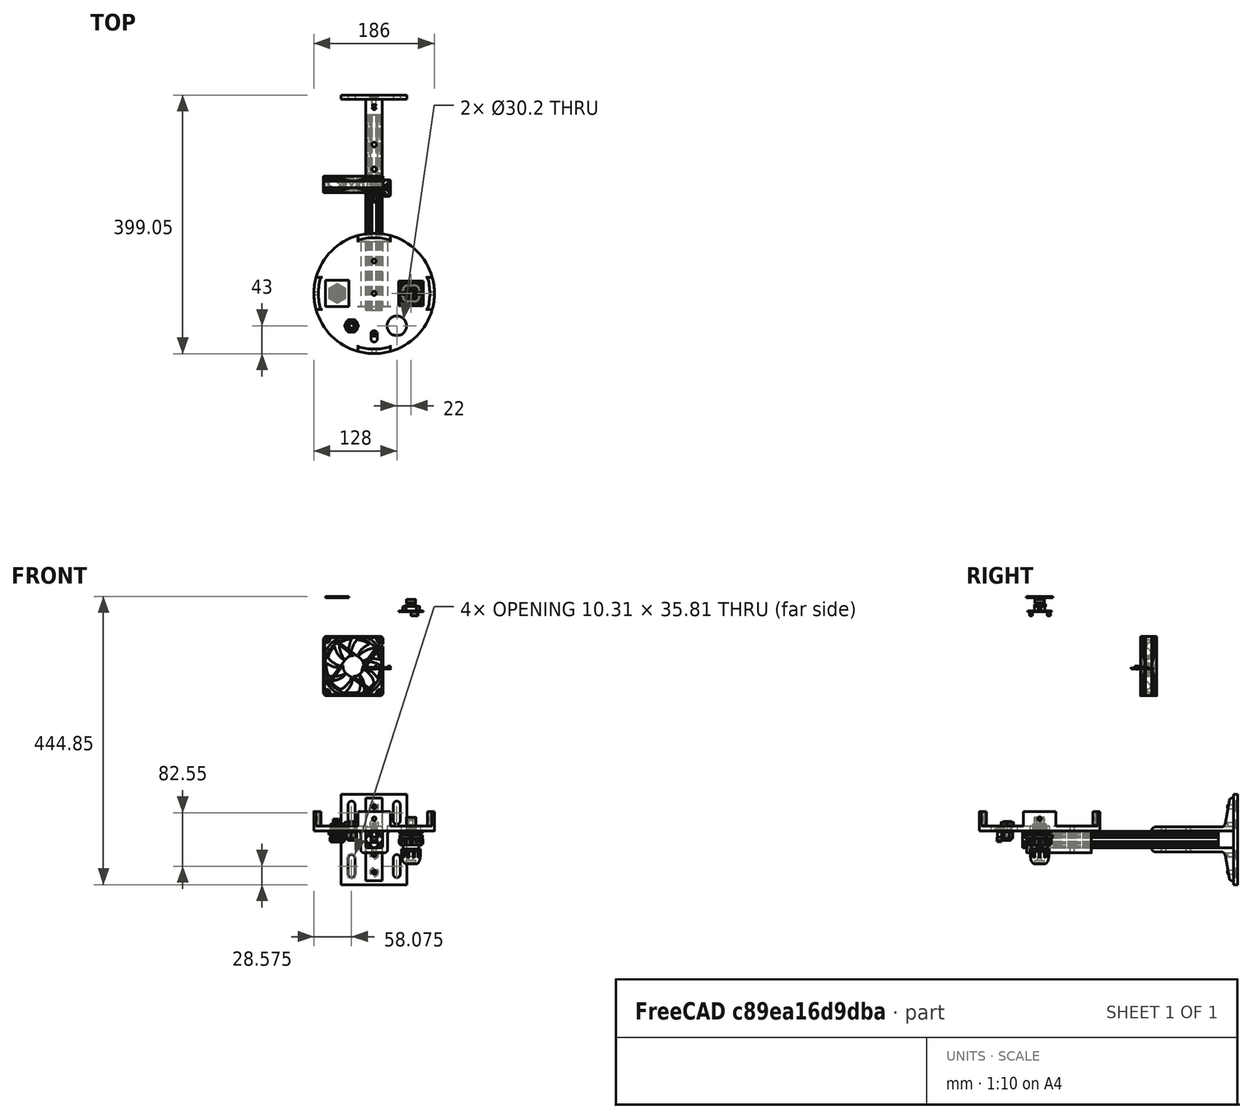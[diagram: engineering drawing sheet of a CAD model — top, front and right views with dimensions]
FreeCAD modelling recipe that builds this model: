
FCSTD DOCUMENT  (FreeCAD 0.20R29410 (Git))
Label: lightModuleV2_2023_08_31
License: All rights reserved
LicenseURL: http://en.wikipedia.org/wiki/All_rights_reserved
objects: Part::Cylinder×123, Part::Feature×114, Sketcher::SketchObject×101, Part::MultiFuse×93, Part::Cut×67, Part::Extrusion×37, Part::Loft×32, Part::Fillet×18, Part::Box×15, App::Part×14, Part::FeaturePython×10, Part::Sphere×4, Mesh::Feature×3, Part::Compound×1, Part::Cone×1, Part::Compound2×1, Part::MultiCommon×1
note: 617 computed .brp shape members not serialized (recipe doc carries the construction recipe); baked Part::Feature solids carry a one-line shape summary decoded from their .brp

FEATURE [Mesh::Feature] Odroid_H004  label="Odroid-H004"
  Placement = pos=(15,-110,-70) rot=(0.57735,-0.57735,0.57735;4.18879rad)
FEATURE [Sketcher::SketchObject] Sketch  label="top"
  FullyConstrained = true
  sketch-geometry (24):
    g0: Circle CenterX=0 CenterY=-150 CenterZ=0 NormalX=0 NormalY=0 NormalZ=1 AngleXU=0 Radius=98
    g1: Circle CenterX=-92 CenterY=-150 CenterZ=0 NormalX=0 NormalY=0 NormalZ=1 AngleXU=0 Radius=2
    g2: Circle CenterX=-57 CenterY=-115 CenterZ=0 NormalX=0 NormalY=0 NormalZ=1 AngleXU=0 Radius=2
    g3: Circle CenterX=-22 CenterY=-150 CenterZ=0 NormalX=0 NormalY=0 NormalZ=1 AngleXU=0 Radius=2
    g4: Circle CenterX=-57 CenterY=-185 CenterZ=0 NormalX=0 NormalY=0 NormalZ=1 AngleXU=0 Radius=2
    g5: Circle CenterX=0 CenterY=-172 CenterZ=0 NormalX=0 NormalY=0 NormalZ=1 AngleXU=0 Radius=2
    g6: Circle CenterX=0 CenterY=-242 CenterZ=0 NormalX=0 NormalY=0 NormalZ=1 AngleXU=0 Radius=2
    g7: Circle CenterX=-35 CenterY=-207 CenterZ=0 NormalX=0 NormalY=0 NormalZ=1 AngleXU=0 Radius=2
    g8: Circle CenterX=35 CenterY=-207 CenterZ=0 NormalX=0 NormalY=0 NormalZ=1 AngleXU=0 Radius=2
    g9: Circle CenterX=57 CenterY=-185 CenterZ=0 NormalX=0 NormalY=0 NormalZ=1 AngleXU=0 Radius=2
    g10: Circle CenterX=22 CenterY=-150 CenterZ=0 NormalX=0 NormalY=0 NormalZ=1 AngleXU=0 Radius=2
    g11: Circle CenterX=57 CenterY=-115 CenterZ=0 NormalX=0 NormalY=0 NormalZ=1 AngleXU=0 Radius=2
    g12: Circle CenterX=92 CenterY=-150 CenterZ=0 NormalX=0 NormalY=0 NormalZ=1 AngleXU=0 Radius=2
    g13: Circle CenterX=0 CenterY=-58 CenterZ=0 NormalX=0 NormalY=0 NormalZ=1 AngleXU=0 Radius=2
    g14: Circle CenterX=0 CenterY=-207 CenterZ=0 NormalX=0 NormalY=0 NormalZ=1 AngleXU=0 Radius=25
    g15: Circle CenterX=57 CenterY=-150 CenterZ=0 NormalX=0 NormalY=0 NormalZ=1 AngleXU=0 Radius=25
    g16: Circle CenterX=0 CenterY=-93 CenterZ=0 NormalX=0 NormalY=0 NormalZ=1 AngleXU=0 Radius=25
    g17: Circle CenterX=-35 CenterY=-93 CenterZ=0 NormalX=0 NormalY=0 NormalZ=1 AngleXU=0 Radius=2
    g18: Circle CenterX=35 CenterY=-93 CenterZ=0 NormalX=0 NormalY=0 NormalZ=1 AngleXU=0 Radius=2
    g19: Circle CenterX=0 CenterY=-128 CenterZ=0 NormalX=0 NormalY=0 NormalZ=1 AngleXU=0 Radius=2
    g20: LineSegment StartX=-75.25 StartY=-129.25 StartZ=0 EndX=-38.75 EndY=-129.25 EndZ=0
    g21: LineSegment StartX=-38.75 StartY=-129.25 StartZ=0 EndX=-38.75 EndY=-170.75 EndZ=0
    g22: LineSegment StartX=-38.75 StartY=-170.75 StartZ=0 EndX=-75.25 EndY=-170.75 EndZ=0
    g23: LineSegment StartX=-75.25 StartY=-170.75 StartZ=0 EndX=-75.25 EndY=-129.25 EndZ=0
  constraints (72):
    c: PointOnObject(g0,g-2)
    c: Radius(g0) = 98
    c: DistanceY(g0) = -150
    c: PointOnObject(g5,g-2)
    c: PointOnObject(g6,g-2)
    c: PointOnObject(g13,g-2)
    c: PointOnObject(g19,g-2)
    c: Equal(g6,g7)
    c: Equal(g6,g4)
    c: Equal(g6,g1)
    c: Equal(g6,g2)
    c: Equal(g6,g3)
    c: Equal(g6,g19)
    c: Equal(g6,g5)
    c: Equal(g6,g8)
    c: Equal(g6,g9)
    c: Equal(g6,g10)
    c: Equal(g6,g12)
    c: Equal(g6,g11)
    c: Equal(g6,g17)
    c: Equal(g6,g18)
    c: Equal(g6,g13)
    c: Radius(g6) = 2
    c: DistanceY(g12,g0) = 0
    c: DistanceY(g10,g0) = 0
    c: DistanceY(g0,g3) = 0
    c: DistanceY(g1,g3) = 0
    c: Equal(g15,g14)
    c: Equal(g15,g16)
    c: Radius(g15) = 25
    c: Coincident(g20,g21)
    c: Coincident(g21,g22)
    c: Coincident(g22,g23)
    c: Coincident(g23,g20)
    c: Horizontal(g20)
    c: Horizontal(g22)
    c: Vertical(g21)
    c: Vertical(g23)
    c: DistanceX(g20) = -38.75
    c: DistanceY(g0,g20) = 20.75
    c: DistanceY(g21,g0) = 20.75
    c: DistanceX(g22,g0) = 75.25
    c: DistanceX(g14,g0) = 0
    c: DistanceX(g0,g15) = 57
    c: DistanceY(g15,g0) = 0
    c: DistanceY(g0,g16) = 57
    c: DistanceX(g16,g0) = 0
    c: DistanceX(g0,g10) = 22
    c: DistanceX(g3,g0) = 22
    c: DistanceX(g1,g0) = 92
    c: DistanceX(g15,g12) = 35
    c: DistanceX(g16,g18) = 35
    c: DistanceX(g17,g16) = 35
    c: DistanceX(g7,g14) = 35
    c: DistanceX(g14,g8) = 35
    c: DistanceX(g9,g15) = 0
    c: DistanceX(g15,g11) = 0
    c: DistanceX(g2,g0) = 57
    c: DistanceY(g18,g16) = 0
    c: DistanceY(g16,g17) = 0
    c: DistanceY(g19,g16) = 35
    c: DistanceY(g16,g13) = 35
    c: DistanceY(g4,g0) = 35
    c: DistanceY(g0,g2) = 35
    c: DistanceY(g14,g5) = 35
    c: DistanceY(g6,g14) = 35
    c: DistanceY(g8,g14) = 0
    c: DistanceY(g14,g7) = 0
    c: DistanceY(g9,g15) = 35
    c: DistanceY(g15,g11) = 35
    c: DistanceX(g4,g2) = 0
    c: DistanceY(g14,g0) = 57
FEATURE [Part::Cylinder] Cylinder036
  Angle = 360
  AttacherType = Attacher::AttachEngine3D
  FirstAngle = 0
  Height = 10
  Placement = pos=(0,-21,0) rot=(0,0,1;0rad)
  Radius = 2
  SecondAngle = 0
FEATURE [Part::Cylinder] Cylinder037
  Angle = 360
  AttacherType = Attacher::AttachEngine3D
  FirstAngle = 0
  Height = 10
  Placement = pos=(20,-21,0) rot=(0,0,1;0rad)
  Radius = 2
  SecondAngle = 0
FEATURE [Part::Cylinder] Cylinder038
  Angle = 360
  AttacherType = Attacher::AttachEngine3D
  FirstAngle = 0
  Height = 10
  Placement = pos=(0,-21,0) rot=(0,0,1;0rad)
  Radius = 2
  SecondAngle = 0
FEATURE [Part::Cylinder] Cylinder039
  Angle = 360
  AttacherType = Attacher::AttachEngine3D
  FirstAngle = 0
  Height = 10
  Placement = pos=(20,-21,0) rot=(0,0,1;0rad)
  Radius = 2
  SecondAngle = 0
FEATURE [Part::Cylinder] Cylinder040  label="base002"
  Angle = 360
  AttacherType = Attacher::AttachEngine3D
  FirstAngle = 0
  Height = 5
  Placement = pos=(5,0,70) rot=(0,0,1;0rad)
  Radius = 40
  SecondAngle = 0
FEATURE [Part::Cylinder] Cylinder041  label="baseCut001"
  Angle = 360
  AttacherType = Attacher::AttachEngine3D
  FirstAngle = 0
  Height = 7
  Placement = pos=(5,0,74) rot=(0,0,1;0rad)
  Radius = 24
  SecondAngle = 0
FEATURE [Part::Cylinder] Cylinder042  label="wireCUt002"
  Angle = 360
  AttacherType = Attacher::AttachEngine3D
  FirstAngle = 0
  Height = 10
  Placement = pos=(-5,0,70) rot=(0,0,1;0rad)
  Radius = 2
  SecondAngle = 0
FEATURE [Part::Cylinder] Cylinder043  label="wireCUt003"
  Angle = 360
  AttacherType = Attacher::AttachEngine3D
  FirstAngle = 0
  Height = 10
  Placement = pos=(15,0,70) rot=(0,0,1;0rad)
  Radius = 2
  SecondAngle = 0
FEATURE [Part::Cylinder] Cylinder044  label="m3Cuts002"
  Angle = 360
  AttacherType = Attacher::AttachEngine3D
  FirstAngle = 0
  Height = 10
  Placement = pos=(5,-9,70) rot=(0,0,1;0rad)
  Radius = 1.75
  SecondAngle = 0
FEATURE [Part::Cylinder] Cylinder045  label="m3Cuts003"
  Angle = 360
  AttacherType = Attacher::AttachEngine3D
  FirstAngle = 0
  Height = 10
  Placement = pos=(5,9,70) rot=(0,0,1;0rad)
  Radius = 1.75
  SecondAngle = 0
FEATURE [Part::Cylinder] Cylinder046  label="m2HeatSetInsets004"
  Angle = 360
  AttacherType = Attacher::AttachEngine3D
  FirstAngle = 0
  Height = 10
  Placement = pos=(-30,0,65) rot=(0,0,1;0rad)
  Radius = 1.6
  SecondAngle = 0
FEATURE [Part::Cylinder] Cylinder047  label="m2HeatSetInsets005"
  Angle = 360
  AttacherType = Attacher::AttachEngine3D
  FirstAngle = 0
  Height = 10
  Placement = pos=(40,0,65) rot=(0,0,1;0rad)
  Radius = 1.6
  SecondAngle = 0
FEATURE [Part::Cylinder] Cylinder048  label="m2HeatSetInsets006"
  Angle = 360
  AttacherType = Attacher::AttachEngine3D
  FirstAngle = 0
  Height = 10
  Placement = pos=(5,35,65) rot=(0,0,1;0rad)
  Radius = 1.6
  SecondAngle = 0
FEATURE [Part::Cylinder] Cylinder049  label="m2HeatSetInsets007"
  Angle = 360
  AttacherType = Attacher::AttachEngine3D
  FirstAngle = 0
  Height = 10
  Placement = pos=(5,-35,65) rot=(0,0,1;0rad)
  Radius = 1.6
  SecondAngle = 0
FEATURE [Part::MultiFuse] Fusion014  label="m3HeatSetCuts003"
  Placement = pos=(-5,38.5,70) rot=(0,0,1;0rad)
  Shapes = -> [Cylinder037,Cylinder036]
FEATURE [Part::MultiFuse] Fusion015  label="m3HeatSetCuts004"
  Placement = pos=(-5,3.5,70) rot=(0,0,1;0rad)
  Shapes = -> [Cylinder039,Cylinder038]
FEATURE [Part::MultiFuse] Fusion016  label="m3HeatSetCuts005"
  Shapes = -> [Fusion015,Fusion014]
FEATURE [Part::MultiFuse] Fusion017  label="wireCuts001"
  Shapes = -> [Cylinder042,Cylinder043]
FEATURE [Part::MultiFuse] Fusion018  label="m3Cute001"
  Shapes = -> [Cylinder044,Cylinder045]
FEATURE [Part::MultiFuse] Fusion019  label="baseCUts001"
  Shapes = -> [Fusion016,Fusion017,Fusion018]
FEATURE [Part::MultiFuse] Fusion021
  Shapes = -> [Cylinder046,Cylinder047,Cylinder048,Cylinder049]
FEATURE [Part::Sphere] Sphere002  label="SphereBase001"
  Angle1 = 0
  Angle2 = 12
  Angle3 = 360
  AttacherType = Attacher::AttachEngine3D
  Placement = pos=(5,0,74) rot=(0,0,1;0rad)
  Radius = 29
FEATURE [Part::Cut] Cut006
  Base = -> Sphere002
  Tool = -> Cylinder041
FEATURE [Part::MultiFuse] Fusion020  label="base003"
  Shapes = -> [Cylinder040,Cut006]
FEATURE [Part::Cut] Cut007
  Base = -> Fusion020
  Tool = -> Fusion019
FEATURE [Part::Cut] Cut008  label="lightModule001"
  Base = -> Cut007
  Placement = pos=(-5,-207,0) rot=(0,1,0;0rad)
  Tool = -> Fusion021
FEATURE [Part::Box] Box005  label="as7265x"
  AttacherType = Attacher::AttachEngine3D
  Height = 2
  Length = 36
  Placement = pos=(-75,-170.5,110) rot=(0,0,1;0rad)
  Width = 41
FEATURE [Part::Cylinder] Cylinder050
  Angle = 360
  AttacherType = Attacher::AttachEngine3D
  FirstAngle = 0
  Height = 10
  Placement = pos=(0,-21,0) rot=(0,0,1;0rad)
  Radius = 2
  SecondAngle = 0
FEATURE [Part::Cylinder] Cylinder051
  Angle = 360
  AttacherType = Attacher::AttachEngine3D
  FirstAngle = 0
  Height = 10
  Placement = pos=(20,-21,0) rot=(0,0,1;0rad)
  Radius = 2
  SecondAngle = 0
FEATURE [Part::Cylinder] Cylinder052
  Angle = 360
  AttacherType = Attacher::AttachEngine3D
  FirstAngle = 0
  Height = 10
  Placement = pos=(0,-21,0) rot=(0,0,1;0rad)
  Radius = 2
  SecondAngle = 0
FEATURE [Part::Cylinder] Cylinder053
  Angle = 360
  AttacherType = Attacher::AttachEngine3D
  FirstAngle = 0
  Height = 10
  Placement = pos=(20,-21,0) rot=(0,0,1;0rad)
  Radius = 2
  SecondAngle = 0
FEATURE [Part::Cylinder] Cylinder054  label="base004"
  Angle = 360
  AttacherType = Attacher::AttachEngine3D
  FirstAngle = 0
  Height = 5
  Placement = pos=(5,0,70) rot=(0,0,1;0rad)
  Radius = 40
  SecondAngle = 0
FEATURE [Part::Cylinder] Cylinder055  label="baseCut002"
  Angle = 360
  AttacherType = Attacher::AttachEngine3D
  FirstAngle = 0
  Height = 7
  Placement = pos=(5,0,74) rot=(0,0,1;0rad)
  Radius = 24
  SecondAngle = 0
FEATURE [Part::Cylinder] Cylinder056  label="wireCUt004"
  Angle = 360
  AttacherType = Attacher::AttachEngine3D
  FirstAngle = 0
  Height = 10
  Placement = pos=(-5,0,70) rot=(0,0,1;0rad)
  Radius = 2
  SecondAngle = 0
FEATURE [Part::Cylinder] Cylinder057  label="wireCUt005"
  Angle = 360
  AttacherType = Attacher::AttachEngine3D
  FirstAngle = 0
  Height = 10
  Placement = pos=(15,0,70) rot=(0,0,1;0rad)
  Radius = 2
  SecondAngle = 0
FEATURE [Part::Cylinder] Cylinder058  label="m3Cuts004"
  Angle = 360
  AttacherType = Attacher::AttachEngine3D
  FirstAngle = 0
  Height = 10
  Placement = pos=(5,-9,70) rot=(0,0,1;0rad)
  Radius = 1.75
  SecondAngle = 0
FEATURE [Part::Cylinder] Cylinder059  label="m3Cuts005"
  Angle = 360
  AttacherType = Attacher::AttachEngine3D
  FirstAngle = 0
  Height = 10
  Placement = pos=(5,9,70) rot=(0,0,1;0rad)
  Radius = 1.75
  SecondAngle = 0
FEATURE [Part::Cylinder] Cylinder060  label="m2HeatSetInsets008"
  Angle = 360
  AttacherType = Attacher::AttachEngine3D
  FirstAngle = 0
  Height = 10
  Placement = pos=(-30,0,65) rot=(0,0,1;0rad)
  Radius = 1.6
  SecondAngle = 0
FEATURE [Part::Cylinder] Cylinder061  label="m2HeatSetInsets009"
  Angle = 360
  AttacherType = Attacher::AttachEngine3D
  FirstAngle = 0
  Height = 10
  Placement = pos=(40,0,65) rot=(0,0,1;0rad)
  Radius = 1.6
  SecondAngle = 0
FEATURE [Part::Cylinder] Cylinder062  label="m2HeatSetInsets010"
  Angle = 360
  AttacherType = Attacher::AttachEngine3D
  FirstAngle = 0
  Height = 10
  Placement = pos=(5,35,65) rot=(0,0,1;0rad)
  Radius = 1.6
  SecondAngle = 0
FEATURE [Part::Cylinder] Cylinder063  label="m2HeatSetInsets011"
  Angle = 360
  AttacherType = Attacher::AttachEngine3D
  FirstAngle = 0
  Height = 10
  Placement = pos=(5,-35,65) rot=(0,0,1;0rad)
  Radius = 1.6
  SecondAngle = 0
FEATURE [Part::MultiFuse] Fusion022  label="m3HeatSetCuts006"
  Placement = pos=(-5,38.5,70) rot=(0,0,1;0rad)
  Shapes = -> [Cylinder051,Cylinder050]
FEATURE [Part::MultiFuse] Fusion023  label="m3HeatSetCuts007"
  Placement = pos=(-5,3.5,70) rot=(0,0,1;0rad)
  Shapes = -> [Cylinder053,Cylinder052]
FEATURE [Part::MultiFuse] Fusion024  label="m3HeatSetCuts008"
  Shapes = -> [Fusion023,Fusion022]
FEATURE [Part::MultiFuse] Fusion025  label="wireCuts002"
  Shapes = -> [Cylinder056,Cylinder057]
FEATURE [Part::MultiFuse] Fusion026  label="m3Cute002"
  Shapes = -> [Cylinder058,Cylinder059]
FEATURE [Part::MultiFuse] Fusion027  label="baseCUts002"
  Shapes = -> [Fusion024,Fusion025,Fusion026]
FEATURE [Part::MultiFuse] Fusion029
  Shapes = -> [Cylinder060,Cylinder061,Cylinder062,Cylinder063]
FEATURE [Part::Sphere] Sphere003  label="SphereBase002"
  Angle1 = 0
  Angle2 = 12
  Angle3 = 360
  AttacherType = Attacher::AttachEngine3D
  Placement = pos=(5,0,74) rot=(0,0,1;0rad)
  Radius = 29
FEATURE [Part::Cut] Cut009
  Base = -> Sphere003
  Tool = -> Cylinder055
FEATURE [Part::MultiFuse] Fusion028  label="base005"
  Shapes = -> [Cylinder054,Cut009]
FEATURE [Part::Cut] Cut010
  Base = -> Fusion028
  Tool = -> Fusion027
FEATURE [Part::Cut] Cut011  label="lightModule002"
  Base = -> Cut010
  Placement = pos=(-62,-150,0) rot=(0,1,0;0rad)
  Tool = -> Fusion029
FEATURE [Part::Cylinder] Cylinder064
  Angle = 360
  AttacherType = Attacher::AttachEngine3D
  FirstAngle = 0
  Height = 10
  Placement = pos=(0,-21,0) rot=(0,0,1;0rad)
  Radius = 2
  SecondAngle = 0
FEATURE [Part::Cylinder] Cylinder065
  Angle = 360
  AttacherType = Attacher::AttachEngine3D
  FirstAngle = 0
  Height = 10
  Placement = pos=(20,-21,0) rot=(0,0,1;0rad)
  Radius = 2
  SecondAngle = 0
FEATURE [Part::Cylinder] Cylinder066
  Angle = 360
  AttacherType = Attacher::AttachEngine3D
  FirstAngle = 0
  Height = 10
  Placement = pos=(0,-21,0) rot=(0,0,1;0rad)
  Radius = 2
  SecondAngle = 0
FEATURE [Part::Cylinder] Cylinder067
  Angle = 360
  AttacherType = Attacher::AttachEngine3D
  FirstAngle = 0
  Height = 10
  Placement = pos=(20,-21,0) rot=(0,0,1;0rad)
  Radius = 2
  SecondAngle = 0
FEATURE [Part::Cylinder] Cylinder068  label="base006"
  Angle = 360
  AttacherType = Attacher::AttachEngine3D
  FirstAngle = 0
  Height = 5
  Placement = pos=(5,0,70) rot=(0,0,1;0rad)
  Radius = 40
  SecondAngle = 0
FEATURE [Part::Cylinder] Cylinder069  label="baseCut003"
  Angle = 360
  AttacherType = Attacher::AttachEngine3D
  FirstAngle = 0
  Height = 7
  Placement = pos=(5,0,74) rot=(0,0,1;0rad)
  Radius = 24
  SecondAngle = 0
FEATURE [Part::Cylinder] Cylinder070  label="wireCUt006"
  Angle = 360
  AttacherType = Attacher::AttachEngine3D
  FirstAngle = 0
  Height = 10
  Placement = pos=(-5,0,70) rot=(0,0,1;0rad)
  Radius = 2
  SecondAngle = 0
FEATURE [Part::Cylinder] Cylinder071  label="wireCUt007"
  Angle = 360
  AttacherType = Attacher::AttachEngine3D
  FirstAngle = 0
  Height = 10
  Placement = pos=(15,0,70) rot=(0,0,1;0rad)
  Radius = 2
  SecondAngle = 0
FEATURE [Part::Cylinder] Cylinder072  label="m3Cuts006"
  Angle = 360
  AttacherType = Attacher::AttachEngine3D
  FirstAngle = 0
  Height = 10
  Placement = pos=(5,-9,70) rot=(0,0,1;0rad)
  Radius = 1.75
  SecondAngle = 0
FEATURE [Part::Cylinder] Cylinder073  label="m3Cuts007"
  Angle = 360
  AttacherType = Attacher::AttachEngine3D
  FirstAngle = 0
  Height = 10
  Placement = pos=(5,9,70) rot=(0,0,1;0rad)
  Radius = 1.75
  SecondAngle = 0
FEATURE [Part::Cylinder] Cylinder074  label="m2HeatSetInsets012"
  Angle = 360
  AttacherType = Attacher::AttachEngine3D
  FirstAngle = 0
  Height = 10
  Placement = pos=(-30,0,65) rot=(0,0,1;0rad)
  Radius = 1.6
  SecondAngle = 0
FEATURE [Part::Cylinder] Cylinder075  label="m2HeatSetInsets013"
  Angle = 360
  AttacherType = Attacher::AttachEngine3D
  FirstAngle = 0
  Height = 10
  Placement = pos=(40,0,65) rot=(0,0,1;0rad)
  Radius = 1.6
  SecondAngle = 0
FEATURE [Part::Cylinder] Cylinder076  label="m2HeatSetInsets014"
  Angle = 360
  AttacherType = Attacher::AttachEngine3D
  FirstAngle = 0
  Height = 10
  Placement = pos=(5,35,65) rot=(0,0,1;0rad)
  Radius = 1.6
  SecondAngle = 0
FEATURE [Part::Cylinder] Cylinder077  label="m2HeatSetInsets015"
  Angle = 360
  AttacherType = Attacher::AttachEngine3D
  FirstAngle = 0
  Height = 10
  Placement = pos=(5,-35,65) rot=(0,0,1;0rad)
  Radius = 1.6
  SecondAngle = 0
FEATURE [Part::MultiFuse] Fusion030  label="m3HeatSetCuts009"
  Placement = pos=(-5,38.5,70) rot=(0,0,1;0rad)
  Shapes = -> [Cylinder065,Cylinder064]
FEATURE [Part::MultiFuse] Fusion031  label="m3HeatSetCuts010"
  Placement = pos=(-5,3.5,70) rot=(0,0,1;0rad)
  Shapes = -> [Cylinder067,Cylinder066]
FEATURE [Part::MultiFuse] Fusion032  label="m3HeatSetCuts011"
  Shapes = -> [Fusion031,Fusion030]
FEATURE [Part::MultiFuse] Fusion033  label="wireCuts003"
  Shapes = -> [Cylinder070,Cylinder071]
FEATURE [Part::MultiFuse] Fusion034  label="m3Cute003"
  Shapes = -> [Cylinder072,Cylinder073]
FEATURE [Part::MultiFuse] Fusion035  label="baseCUts003"
  Shapes = -> [Fusion032,Fusion033,Fusion034]
FEATURE [Part::MultiFuse] Fusion037
  Shapes = -> [Cylinder074,Cylinder075,Cylinder076,Cylinder077]
FEATURE [Part::Sphere] Sphere004  label="SphereBase003"
  Angle1 = 0
  Angle2 = 12
  Angle3 = 360
  AttacherType = Attacher::AttachEngine3D
  Placement = pos=(5,0,74) rot=(0,0,1;0rad)
  Radius = 29
FEATURE [Part::Cut] Cut012
  Base = -> Sphere004
  Tool = -> Cylinder069
FEATURE [Part::MultiFuse] Fusion036  label="base007"
  Shapes = -> [Cylinder068,Cut012]
FEATURE [Part::Cut] Cut013
  Base = -> Fusion036
  Tool = -> Fusion035
FEATURE [Part::Cut] Cut014  label="lightModule003"
  Base = -> Cut013
  Placement = pos=(52,-150,0) rot=(0,1,0;0rad)
  Tool = -> Fusion037
FEATURE [Part::Cylinder] Cylinder078
  Angle = 360
  AttacherType = Attacher::AttachEngine3D
  FirstAngle = 0
  Height = 10
  Placement = pos=(0,-21,0) rot=(0,0,1;0rad)
  Radius = 2
  SecondAngle = 0
FEATURE [Part::Cylinder] Cylinder079
  Angle = 360
  AttacherType = Attacher::AttachEngine3D
  FirstAngle = 0
  Height = 10
  Placement = pos=(20,-21,0) rot=(0,0,1;0rad)
  Radius = 2
  SecondAngle = 0
FEATURE [Part::Cylinder] Cylinder080
  Angle = 360
  AttacherType = Attacher::AttachEngine3D
  FirstAngle = 0
  Height = 10
  Placement = pos=(0,-21,0) rot=(0,0,1;0rad)
  Radius = 2
  SecondAngle = 0
FEATURE [Part::Cylinder] Cylinder081
  Angle = 360
  AttacherType = Attacher::AttachEngine3D
  FirstAngle = 0
  Height = 10
  Placement = pos=(20,-21,0) rot=(0,0,1;0rad)
  Radius = 2
  SecondAngle = 0
FEATURE [Part::Cylinder] Cylinder082  label="base008"
  Angle = 360
  AttacherType = Attacher::AttachEngine3D
  FirstAngle = 0
  Height = 5
  Placement = pos=(5,0,70) rot=(0,0,1;0rad)
  Radius = 40
  SecondAngle = 0
FEATURE [Part::Cylinder] Cylinder083  label="baseCut004"
  Angle = 360
  AttacherType = Attacher::AttachEngine3D
  FirstAngle = 0
  Height = 7
  Placement = pos=(5,0,74) rot=(0,0,1;0rad)
  Radius = 24
  SecondAngle = 0
FEATURE [Part::Cylinder] Cylinder084  label="wireCUt008"
  Angle = 360
  AttacherType = Attacher::AttachEngine3D
  FirstAngle = 0
  Height = 10
  Placement = pos=(-5,0,70) rot=(0,0,1;0rad)
  Radius = 2
  SecondAngle = 0
FEATURE [Part::Cylinder] Cylinder085  label="wireCUt009"
  Angle = 360
  AttacherType = Attacher::AttachEngine3D
  FirstAngle = 0
  Height = 10
  Placement = pos=(15,0,70) rot=(0,0,1;0rad)
  Radius = 2
  SecondAngle = 0
FEATURE [Part::Cylinder] Cylinder086  label="m3Cuts008"
  Angle = 360
  AttacherType = Attacher::AttachEngine3D
  FirstAngle = 0
  Height = 10
  Placement = pos=(5,-9,70) rot=(0,0,1;0rad)
  Radius = 1.75
  SecondAngle = 0
FEATURE [Part::Cylinder] Cylinder087  label="m3Cuts009"
  Angle = 360
  AttacherType = Attacher::AttachEngine3D
  FirstAngle = 0
  Height = 10
  Placement = pos=(5,9,70) rot=(0,0,1;0rad)
  Radius = 1.75
  SecondAngle = 0
FEATURE [Part::Cylinder] Cylinder088  label="m2HeatSetInsets016"
  Angle = 360
  AttacherType = Attacher::AttachEngine3D
  FirstAngle = 0
  Height = 10
  Placement = pos=(-30,0,65) rot=(0,0,1;0rad)
  Radius = 1.6
  SecondAngle = 0
FEATURE [Part::Cylinder] Cylinder089  label="m2HeatSetInsets017"
  Angle = 360
  AttacherType = Attacher::AttachEngine3D
  FirstAngle = 0
  Height = 10
  Placement = pos=(40,0,65) rot=(0,0,1;0rad)
  Radius = 1.6
  SecondAngle = 0
FEATURE [Part::Cylinder] Cylinder090  label="m2HeatSetInsets018"
  Angle = 360
  AttacherType = Attacher::AttachEngine3D
  FirstAngle = 0
  Height = 10
  Placement = pos=(5,35,65) rot=(0,0,1;0rad)
  Radius = 1.6
  SecondAngle = 0
FEATURE [Part::Cylinder] Cylinder091  label="m2HeatSetInsets019"
  Angle = 360
  AttacherType = Attacher::AttachEngine3D
  FirstAngle = 0
  Height = 10
  Placement = pos=(5,-35,65) rot=(0,0,1;0rad)
  Radius = 1.6
  SecondAngle = 0
FEATURE [Part::MultiFuse] Fusion038  label="m3HeatSetCuts012"
  Placement = pos=(-5,38.5,70) rot=(0,0,1;0rad)
  Shapes = -> [Cylinder079,Cylinder078]
FEATURE [Part::MultiFuse] Fusion039  label="m3HeatSetCuts013"
  Placement = pos=(-5,3.5,70) rot=(0,0,1;0rad)
  Shapes = -> [Cylinder081,Cylinder080]
FEATURE [Part::MultiFuse] Fusion040  label="m3HeatSetCuts014"
  Shapes = -> [Fusion039,Fusion038]
FEATURE [Part::MultiFuse] Fusion041  label="wireCuts004"
  Shapes = -> [Cylinder084,Cylinder085]
FEATURE [Part::MultiFuse] Fusion042  label="m3Cute004"
  Shapes = -> [Cylinder086,Cylinder087]
FEATURE [Part::MultiFuse] Fusion043  label="baseCUts004"
  Shapes = -> [Fusion040,Fusion041,Fusion042]
FEATURE [Part::MultiFuse] Fusion045
  Shapes = -> [Cylinder088,Cylinder089,Cylinder090,Cylinder091]
FEATURE [Part::Sphere] Sphere005  label="SphereBase004"
  Angle1 = 0
  Angle2 = 12
  Angle3 = 360
  AttacherType = Attacher::AttachEngine3D
  Placement = pos=(5,0,74) rot=(0,0,1;0rad)
  Radius = 29
FEATURE [Part::Cut] Cut015
  Base = -> Sphere005
  Tool = -> Cylinder083
FEATURE [Part::MultiFuse] Fusion044  label="base009"
  Shapes = -> [Cylinder082,Cut015]
FEATURE [Part::Cut] Cut016
  Base = -> Fusion044
  Tool = -> Fusion043
FEATURE [Part::Cut] Cut017  label="lightModule004"
  Base = -> Cut016
  Placement = pos=(-5,-93,0) rot=(0,1,0;0rad)
  Tool = -> Fusion045
FEATURE [Part::MultiFuse] Fusion  label="lightModules"
  Placement = pos=(0,0,30) rot=(0,0,1;0rad)
  Shapes = -> [Cut008,Cut011,Cut014,Cut017]
FEATURE [Part::Extrusion] Extrude  label="top001"
  Base = -> Sketch
  Dir = (0,0,1)
  DirMode = 2
  FaceMakerClass = Part::FaceMakerBullseye
  LengthFwd = 5
  LengthRev = 0
  Placement = pos=(0,0,100) rot=(0,0,1;0rad)
  Solid = true
  Symmetric = false
FEATURE [Part::Feature] Part__Feature  label="elpCamera"
  Placement = pos=(57,-150,90) rot=(0,0,1;0rad)
  shape: bbox 38 x 38 x 25.12 mm, 164 faces (baked)
FEATURE [Part::FeaturePython] Tube  label="tube001"  # WARN: FeaturePython — macro-defined, semantics opaque (R4)
  AttacherType = Attacher::AttachEngine3D
  Height = 20
  InnerRadius = 94
  OuterRadius = 98
  Placement = pos=(0,-150,80) rot=(0,0,1;0rad)
FEATURE [Part::Feature] Part__Feature010  label="veml6075_sensor"
  Placement = pos=(0,-92,105) rot=(0,0,1;0rad)
  shape: bbox 15.31 x 17.01 x 46.02 mm, 450 faces (baked)
FEATURE [Sketcher::SketchObject] Sketch001
  FullyConstrained = true
  Placement = pos=(0,0,105) rot=(0,0,1;0rad)
  sketch-geometry (14):
    g0: Circle CenterX=0 CenterY=-93 CenterZ=0 NormalX=0 NormalY=0 NormalZ=1 AngleXU=0 Radius=25
    g1: Circle CenterX=0 CenterY=-93 CenterZ=0 NormalX=0 NormalY=0 NormalZ=1 AngleXU=0 Radius=26.5
    g2: Circle CenterX=57 CenterY=-150 CenterZ=0 NormalX=0 NormalY=0 NormalZ=1 AngleXU=0 Radius=25
    g3: Circle CenterX=57 CenterY=-150 CenterZ=0 NormalX=0 NormalY=0 NormalZ=1 AngleXU=0 Radius=26.5
    g4: Circle CenterX=0 CenterY=-207 CenterZ=0 NormalX=0 NormalY=0 NormalZ=1 AngleXU=0 Radius=25
    g5: Circle CenterX=0 CenterY=-207 CenterZ=0 NormalX=0 NormalY=0 NormalZ=1 AngleXU=0 Radius=26.5
    g6: LineSegment StartX=-75.25 StartY=-129.25 StartZ=0 EndX=-38.75 EndY=-129.25 EndZ=0
    g7: LineSegment StartX=-38.75 StartY=-129.25 StartZ=0 EndX=-38.75 EndY=-170.75 EndZ=0
    g8: LineSegment StartX=-38.75 StartY=-170.75 StartZ=0 EndX=-75.25 EndY=-170.75 EndZ=0
    g9: LineSegment StartX=-75.25 StartY=-170.75 StartZ=0 EndX=-75.25 EndY=-129.25 EndZ=0
    g10: LineSegment StartX=-75.7 StartY=-128.8 StartZ=0 EndX=-38.3 EndY=-128.8 EndZ=0
    g11: LineSegment StartX=-38.3 StartY=-128.8 StartZ=0 EndX=-38.3 EndY=-171.2 EndZ=0
    g12: LineSegment StartX=-38.3 StartY=-171.2 StartZ=0 EndX=-75.7 EndY=-171.2 EndZ=0
    g13: LineSegment StartX=-75.7 StartY=-171.2 StartZ=0 EndX=-75.7 EndY=-128.8 EndZ=0
  constraints (39):
    c: PointOnObject(g0,g-2)
    c: Coincident(g1,g0)
    c: Coincident(g3,g2)
    c: PointOnObject(g4,g-2)
    c: Coincident(g5,g4)
    c: Coincident(g6,g7)
    c: Coincident(g7,g8)
    c: Coincident(g8,g9)
    c: Coincident(g9,g6)
    c: Horizontal(g6)
    c: Horizontal(g8)
    c: Vertical(g7)
    c: Vertical(g9)
    c: DistanceY(g0) = -93
    c: DistanceY(g2) = -150
    c: DistanceX(g2) = 57
    c: Equal(g0,g2)
    c: Equal(g0,g4)
    c: Radius(g0) = 25
    c: Equal(g3,g1)
    c: Equal(g3,g5)
    c: Radius(g3) = 26.5
    c: DistanceY(g4) = -207
    c: DistanceY(g7) = -170.75
    c: DistanceX(g7) = -38.75
    c: DistanceX(g6) = -75.25
    c: DistanceY(g6) = -129.25
    c: Coincident(g10,g11)
    c: Coincident(g11,g12)
    c: Coincident(g12,g13)
    c: Coincident(g13,g10)
    c: Horizontal(g10)
    c: Horizontal(g12)
    c: Vertical(g11)
    c: Vertical(g13)
    c: DistanceY(g11,g7) = 0.45
    c: DistanceX(g7,g11) = 0.45
    c: DistanceX(g10,g6) = 0.45
    c: DistanceY(g6,g10) = 0.45
FEATURE [Part::Extrusion] Extrude001
  Base = -> Sketch001
  Dir = (0,0,1)
  DirMode = 2
  FaceMakerClass = Part::FaceMakerBullseye
  LengthFwd = 1
  LengthRev = 0
  Solid = true
  Symmetric = false
FEATURE [Part::MultiFuse] Fusion046  label="top002"
  Shapes = -> [Extrude001,Extrude]
FEATURE [Part::Cylinder] Cylinder
  Angle = 360
  AttacherType = Attacher::AttachEngine3D
  FirstAngle = 0
  Height = 300
  Placement = pos=(0,0,90) rot=(1,0,0;1.5708rad)
  Radius = 2.2
  SecondAngle = 0
FEATURE [Part::Cylinder] Cylinder092
  Angle = 360
  AttacherType = Attacher::AttachEngine3D
  FirstAngle = 0
  Height = 300
  Placement = pos=(-150,-150,90) rot=(0.57735,0.57735,0.57735;2.0944rad)
  Radius = 2.2
  SecondAngle = 0
FEATURE [Part::MultiFuse] Fusion047  label="m4Cuts"
  Shapes = -> [Cylinder092,Cylinder]
FEATURE [Part::Fillet] Fillet  label="top003"
  Base = -> Fusion046
  Edges = 1 edges r=2: [Edge3]
FEATURE [Part::Fillet] Fillet001  label="tube"
  Base = -> Tube
  Edges = 1 edges r=2: [Edge5]
FEATURE [Part::MultiFuse] Fusion048  label="top004"
  Shapes = -> [Fillet,Fillet001]
FEATURE [Part::Cut] Cut  label="top005"
  Base = -> Fusion048
  Tool = -> Fusion047
FEATURE [Part::Cylinder] Cylinder094  label="refModules"
  Angle = 360
  AttacherType = Attacher::AttachEngine3D
  FirstAngle = 0
  Height = 75
  Placement = pos=(0,-207,37) rot=(0,0,1;0rad)
  Radius = 3.75
  SecondAngle = 0
FEATURE [Part::Cylinder] Cylinder095  label="refModulesCoverCut"
  Angle = 360
  AttacherType = Attacher::AttachEngine3D
  FirstAngle = 0
  Height = 60
  Placement = pos=(0,-207,37) rot=(0,0,1;0rad)
  Radius = 4.5
  SecondAngle = 0
FEATURE [Sketcher::SketchObject] Sketch002
  FullyConstrained = true
  sketch-geometry (16):
    g0: Circle CenterX=-67 CenterY=-167.5 CenterZ=0 NormalX=0 NormalY=0 NormalZ=1 AngleXU=0 Radius=1.625
    g1: Circle CenterX=-47 CenterY=-167.5 CenterZ=0 NormalX=0 NormalY=0 NormalZ=1 AngleXU=0 Radius=1.625
    g2: Circle CenterX=-67 CenterY=-132.5 CenterZ=0 NormalX=0 NormalY=0 NormalZ=1 AngleXU=0 Radius=1.625
    g3: Circle CenterX=-47 CenterY=-132.5 CenterZ=0 NormalX=0 NormalY=0 NormalZ=1 AngleXU=0 Radius=1.625
    g4: LineSegment StartX=-62 StartY=-129.75 StartZ=0 EndX=-72 EndY=-129.75 EndZ=0
    g5: LineSegment StartX=-52 StartY=-129.75 StartZ=0 EndX=-42 EndY=-129.75 EndZ=0
    g6: LineSegment StartX=-72 StartY=-129.75 StartZ=0 EndX=-72 EndY=-170.25 EndZ=0
    g7: LineSegment StartX=-72 StartY=-170.25 StartZ=0 EndX=-62 EndY=-170.25 EndZ=0
    g8: LineSegment StartX=-62 StartY=-170.25 StartZ=0 EndX=-62 EndY=-155 EndZ=0
    g9: LineSegment StartX=-52 StartY=-155 StartZ=0 EndX=-52 EndY=-170.25 EndZ=0
    g10: LineSegment StartX=-52 StartY=-170.25 StartZ=0 EndX=-42 EndY=-170.25 EndZ=0
    g11: LineSegment StartX=-42 StartY=-170.25 StartZ=0 EndX=-42 EndY=-129.75 EndZ=0
    g12: LineSegment StartX=-62 StartY=-155 StartZ=0 EndX=-52 EndY=-155 EndZ=0
    g13: LineSegment StartX=-62 StartY=-129.75 StartZ=0 EndX=-62 EndY=-145 EndZ=0
    g14: LineSegment StartX=-62 StartY=-145 StartZ=0 EndX=-52 EndY=-145 EndZ=0
    g15: LineSegment StartX=-52 StartY=-145 StartZ=0 EndX=-52 EndY=-129.75 EndZ=0
  constraints (48):
    c: DistanceY(g2,g3) = 0
    c: DistanceX(g0,g2) = 0
    c: DistanceX(g1,g3) = 0
    c: DistanceX(g1) = -47
    c: DistanceY(g1) = -167.5
    c: DistanceX(g0,g1) = 20
    c: Horizontal(g4)
    c: Horizontal(g5)
    c: Vertical(g6)
    c: Coincident(g7,g6)
    c: Horizontal(g7)
    c: Coincident(g8,g7)
    c: Vertical(g9)
    c: Coincident(g10,g9)
    c: Horizontal(g10)
    c: Coincident(g11,g10)
    c: Vertical(g8)
    c: DistanceX(g4,g4) = 10
    c: DistanceX(g5,g5) = 10
    c: DistanceX(g6,g7) = 10
    c: DistanceX(g9,g10) = 10
    c: Vertical(g11)
    c: DistanceY(g7,g9) = 0
    c: DistanceY(g4,g5) = 0
    c: DistanceX(g6,g0) = 5
    c: DistanceX(g9,g1) = 5
    c: DistanceY(g2,g4) = 2.75
    c: Coincident(g4,g6)
    c: Coincident(g12,g8)
    c: Horizontal(g12)
    c: Coincident(g9,g12)
    c: Coincident(g13,g4)
    c: Vertical(g13)
    c: Coincident(g14,g13)
    c: Horizontal(g14)
    c: Coincident(g15,g14)
    c: Coincident(g15,g5)
    c: Vertical(g15)
    c: Coincident(g5,g11)
    c: DistanceY(g8,g13) = 10
    c: DistanceY(g13) = -145
    c: DistanceY(g7,g0) = 2.75
    c: Equal(g1,g0)
    c: Equal(g1,g2)
    c: Equal(g1,g3)
    c: Diameter(g1) = 3.25
    c: DistanceY(g1,g0) = 0
    c: DistanceY(g2) = -132.5
FEATURE [Sketcher::SketchObject] Sketch003
  FullyConstrained = true
  sketch-geometry (6):
    g0: Circle CenterX=74 CenterY=-167 CenterZ=0 NormalX=0 NormalY=0 NormalZ=1 AngleXU=0 Radius=1.65
    g1: Circle CenterX=40 CenterY=-167 CenterZ=0 NormalX=0 NormalY=0 NormalZ=1 AngleXU=0 Radius=1.65
    g2: Circle CenterX=40 CenterY=-133 CenterZ=0 NormalX=0 NormalY=0 NormalZ=1 AngleXU=0 Radius=1.65
    g3: Circle CenterX=74 CenterY=-133 CenterZ=0 NormalX=0 NormalY=0 NormalZ=1 AngleXU=0 Radius=1.65
    g4: Circle CenterX=57 CenterY=-150 CenterZ=0 NormalX=0 NormalY=0 NormalZ=1 AngleXU=0 Radius=27.5
    g5: Circle CenterX=57 CenterY=-150 CenterZ=0 NormalX=0 NormalY=0 NormalZ=1 AngleXU=0 Radius=21
  constraints (17):
    c: Equal(g3,g0)
    c: Equal(g3,g1)
    c: Equal(g3,g2)
    c: Diameter(g3) = 3.3
    c: DistanceX(g1) = 40
    c: DistanceY(g1) = -167
    c: DistanceY(g1,g0) = 0
    c: DistanceX(g2,g1) = 0
    c: DistanceY(g1,g2) = 34
    c: DistanceY(g2,g3) = 0
    c: DistanceX(g2,g3) = 34
    c: DistanceX(g0,g3) = 0
    c: Coincident(g5,g4)
    c: DistanceX(g4) = 57
    c: DistanceY(g4) = -150
    c: Diameter(g5) = 42
    c: Diameter(g4) = 55
FEATURE [Part::Feature] Part__Feature105  label="Printed Circuit Board"
  shape: bbox 25.4 x 17.78 x 1.6 mm, 42 faces (baked)
FEATURE [Part::Feature] Part__Feature106  label="EAHC2835WD6"
  shape: bbox 3.513 x 2.813 x 0.7485 mm, 108 faces, 4 solids (baked)
FEATURE [Part::Feature] Part__Feature107  label="AS7341 v2"
  Placement = pos=(0,-0.339822,1.6) rot=(0,0,1;0rad)
  shape: bbox 2 x 3.1 x 1.1 mm, 267 faces, 26 solids (baked)
FEATURE [Part::Feature] Part__Feature108  label="CAPC-0805-T0.95-BN v1"
  Placement = pos=(-5.01759,-3.15294,1.6) rot=(0,0,1;0rad)
  shape: bbox 2.1 x 1.35 x 0.95 mm, 42 faces (baked)
FEATURE [Part::Feature] Part__Feature109  label="CAPC-0805-T0.95-BN v002"
  Placement = pos=(-5.48627,2.66154,1.6) rot=(0,0,-1;1.5708rad)
  shape: bbox 1.35 x 2.1 x 0.95 mm, 42 faces (baked)
FEATURE [Part::Feature] Part__Feature110  label="CAPC-0805-T0.95-BN v003"
  Placement = pos=(-3.43627,2.66154,1.6) rot=(0,0,-1;1.5708rad)
  shape: bbox 1.35 x 2.1 x 0.95 mm, 42 faces (baked)
FEATURE [Part::Feature] Part__Feature111  label="CAPC-0603-T0.9-BN v1"
  Placement = pos=(-1.69987,-3.28475,1.6) rot=(0,0,1;0rad)
  shape: bbox 1.7 x 0.9 x 0.9 mm, 42 faces (baked)
FEATURE [Part::Feature] Part__Feature112  label="BODY_MF06A"
  Placement = pos=(0,0,0.762) rot=(0.57735,-0.57735,-0.57735;2.0944rad)
  shape: bbox 1.601 x 2.921 x 1.016 mm, 42 faces (baked)
FEATURE [Part::Feature] Part__Feature113  label="LEAD_MF06A"
  Placement = pos=(-0.9652,-0.9525,0.1016) rot=(0.57735,-0.57735,-0.57735;2.0944rad)
  shape: bbox 0.6223 x 0.3749 x 0.8636 mm, 14 faces (baked)
FEATURE [Part::Feature] Part__Feature114  label="LEAD_MF06A001"
  Placement = pos=(-0.9652,0,0.1016) rot=(0.57735,-0.57735,-0.57735;2.0944rad)
  shape: bbox 0.6223 x 0.3749 x 0.8636 mm, 14 faces (baked)
FEATURE [Part::Feature] Part__Feature115  label="LEAD_MF06A002"
  Placement = pos=(-0.9652,0.9525,0.1016) rot=(0.57735,-0.57735,-0.57735;2.0944rad)
  shape: bbox 0.6223 x 0.3749 x 0.8636 mm, 14 faces (baked)
FEATURE [Part::Feature] Part__Feature116  label="LEAD_MF06A003"
  Placement = pos=(0.9652,-0.9525,0.1016) rot=(0.57735,0.57735,0.57735;2.0944rad)
  shape: bbox 0.6223 x 0.3749 x 0.8636 mm, 14 faces (baked)
FEATURE [Part::Feature] Part__Feature117  label="LEAD_MF06A004"
  Placement = pos=(0.9652,0,0.1016) rot=(0.57735,0.57735,0.57735;2.0944rad)
  shape: bbox 0.6223 x 0.3749 x 0.8636 mm, 14 faces (baked)
FEATURE [Part::Feature] Part__Feature118  label="LEAD_MF06A005"
  Placement = pos=(0.9652,0.9525,0.1016) rot=(0.57735,0.57735,0.57735;2.0944rad)
  shape: bbox 0.6223 x 0.3749 x 0.8636 mm, 14 faces (baked)
FEATURE [Part::Feature] Part__Feature119  label="SOT363 v2"
  Placement = pos=(4.97054,-0.645171,1.675) rot=(0,0,1;3.14159rad)
  shape: bbox 2.1 x 2 x 1.1 mm, 94 faces, 7 solids (baked)
FEATURE [Part::Feature] Part__Feature120  label="LED 0603 single color v1"
  Placement = pos=(-9.18406,3.72778,1.60762) rot=(0,0,1;1.5708rad)
  shape: bbox 1.961 x 0.7932 x 0.7145 mm, 63 faces, 5 solids (baked)
FEATURE [Part::Feature] Part__Feature121  label="RESC-0603 v1"
  Placement = pos=(4.83432,-3.67461,1.6) rot=(0,0,1;0rad)
  shape: bbox 1.7 x 0.9 x 0.55 mm, 52 faces, 3 solids (baked)
FEATURE [Part::Feature] Part__Feature122  label="RESC-0603 v002"
  Placement = pos=(-7.14949,3.61248,1.6) rot=(0,0,-1;1.5708rad)
  shape: bbox 0.9 x 1.7 x 0.55 mm, 52 faces, 3 solids (baked)
FEATURE [Part::Feature] Part__Feature123  label="YC164_RESPACK v1"
  Placement = pos=(2.99591,1.52916,1.6) rot=(0,0,1;0rad)
  shape: bbox 3.2 x 1.6 x 0.61 mm, 172 faces (baked)
FEATURE [Part::Feature] Part__Feature124  label="qwicc v2"
  Placement = pos=(-10.8364,0.0607456,1.65) rot=(0,0,-1;1.5708rad)
  shape: bbox 4.95 x 6 x 2.96 mm, 229 faces, 7 solids (baked)
FEATURE [Part::Feature] Part__Feature125  label="qwicc v003"
  Placement = pos=(10.8256,0.00556102,1.65) rot=(0,0,1;1.5708rad)
  shape: bbox 4.95 x 6 x 2.96 mm, 229 faces, 7 solids (baked)
FEATURE [App::Part] sot_23_6_v2  label="sot-23-6 v2"
  Group = -> [Part__Feature112,Part__Feature113,Part__Feature114,Part__Feature115,Part__Feature116,Part__Feature117,Part__Feature118]
  Origin = -> Origin008
  Placement = pos=(-4.47945,-0.603742,1.69152) rot=(0,0,1;0rad)
FEATURE [App::Part] Adafruit_AS7341_STEMMA_QT_v2  label="ltr390"
  Group = -> [Part__Feature105,Part__Feature106,Part__Feature107,Part__Feature108,Part__Feature109,Part__Feature110,Part__Feature111,sot_23_6_v2,Part__Feature119,Part__Feature120,Part__Feature121,Part__Feature122,Part__Feature123,Part__Feature124,Part__Feature125]
  Origin = -> Origin009
  Placement = pos=(0,-98,110) rot=(0,0,1;0rad)
FEATURE [Part::Box] Box  label="guva"
  AttacherType = Attacher::AttachEngine3D
  Height = 2
  Length = 19
  Placement = pos=(-9.5,-88,0) rot=(0,0,1;0rad)
  Width = 10
FEATURE [Part::Cylinder] Cylinder098
  Angle = 360
  AttacherType = Attacher::AttachEngine3D
  FirstAngle = 0
  Height = 10
  Placement = pos=(6.5,-83,0) rot=(0,0,1;0rad)
  Radius = 1.13
  SecondAngle = 0
FEATURE [Part::Cut] Cut018  label="guva001"
  Base = -> Box
  Placement = pos=(0,0,110) rot=(0,0,1;0rad)
  Tool = -> Cylinder098
FEATURE [Sketcher::SketchObject] Sketch004
  FullyConstrained = true
  sketch-geometry (11):
    g0: Circle CenterX=6.5 CenterY=-83 CenterZ=0 NormalX=0 NormalY=0 NormalZ=1 AngleXU=0 Radius=1.125
    g1: Circle CenterX=10.15 CenterY=-91.65 CenterZ=0 NormalX=0 NormalY=0 NormalZ=1 AngleXU=0 Radius=1.125
    g2: Circle CenterX=10.15 CenterY=-104.35 CenterZ=0 NormalX=0 NormalY=0 NormalZ=1 AngleXU=0 Radius=1.125
    g3: Circle CenterX=-10.15 CenterY=-104.35 CenterZ=0 NormalX=0 NormalY=0 NormalZ=1 AngleXU=0 Radius=1.125
    g4: Circle CenterX=-10.15 CenterY=-91.65 CenterZ=0 NormalX=0 NormalY=0 NormalZ=1 AngleXU=0 Radius=1.125
    g5: ArcOfCircle CenterX=-9.5 CenterY=-78 CenterZ=0 NormalX=0 NormalY=0 NormalZ=1 AngleXU=0 Radius=9.5 StartAngle=4.71239 EndAngle=6.28319
    g6: LineSegment StartX=-9.5 StartY=-87.5 StartZ=0 EndX=-15.15 EndY=-87.5 EndZ=0
    g7: LineSegment StartX=-15.15 StartY=-87.5 StartZ=0 EndX=-15.15 EndY=-109.35 EndZ=0
    g8: LineSegment StartX=-15.15 StartY=-109.35 StartZ=0 EndX=15.15 EndY=-109.35 EndZ=0
    g9: LineSegment StartX=15.15 StartY=-109.35 StartZ=0 EndX=15.15 EndY=-78 EndZ=0
    g10: LineSegment StartX=15.15 StartY=-78 StartZ=0 EndX=0 EndY=-78 EndZ=0
  constraints (34):
    c: DistanceX(g4,g3) = 0
    c: DistanceX(g2,g1) = 0
    c: Equal(g2,g3)
    c: Equal(g2,g4)
    c: Equal(g2,g1)
    c: Equal(g2,g0)
    c: Diameter(g2) = 2.25
    c: DistanceX(g2) = 10.15
    c: DistanceY(g2) = -104.35
    c: DistanceY(g2,g1) = 12.7
    c: DistanceY(g3,g2) = 0
    c: DistanceX(g3,g2) = 20.3
    c: DistanceY(g4,g1) = 0
    c: DistanceY(g0) = -83
    c: DistanceX(g0) = 6.5
    c: PointOnObject(g5,g-2)
    c: Coincident(g6,g5)
    c: Horizontal(g6)
    c: Coincident(g7,g6)
    c: Vertical(g7)
    c: Coincident(g8,g7)
    c: Horizontal(g8)
    c: Coincident(g9,g8)
    c: Vertical(g9)
    c: Coincident(g10,g9)
    c: Coincident(g10,g5)
    c: Horizontal(g10)
    c: DistanceY(g5) = -78
    c: DistanceY(g5,g5) = 0
    c: DistanceX(g5,g5) = 9.5
    c: DistanceX(g5,g5) = 0
    c: DistanceX(g1,g9) = 5
    c: DistanceX(g7,g3) = 5
    c: DistanceY(g7,g3) = 5
FEATURE [Part::Extrusion] Extrude002  label="as7265Holder"
  Base = -> Sketch002
  Dir = (0,0,1)
  DirMode = 2
  FaceMakerClass = Part::FaceMakerBullseye
  LengthFwd = 10
  LengthRev = 0
  Placement = pos=(0,0,100) rot=(0,0,1;0rad)
  Solid = true
  Symmetric = false
FEATURE [Part::Extrusion] Extrude003  label="cameraHolder"
  Base = -> Sketch003
  Dir = (0,0,1)
  DirMode = 2
  FaceMakerClass = Part::FaceMakerBullseye
  LengthFwd = 8.25
  LengthRev = 0
  Placement = pos=(0,0,80) rot=(0,0,1;0rad)
  Solid = true
  Symmetric = false
FEATURE [Part::Extrusion] Extrude004  label="uvHolder"
  Base = -> Sketch004
  Dir = (0,0,1)
  DirMode = 2
  FaceMakerClass = Part::FaceMakerBullseye
  LengthFwd = 10
  LengthRev = 0
  Placement = pos=(0,0,100) rot=(0,0,1;0rad)
  Solid = true
  Symmetric = false
FEATURE [Part::Feature] Part__Feature040  label="CeramicBody (1)"
  shape: bbox 1.8 x 1.23 x 1.23 mm, 10 faces (baked)
FEATURE [Part::Feature] Part__Feature104  label="ips7100"
  Placement = pos=(-24,0,222) rot=(0.999993,-0.003655,0;3.14159rad)
  shape: bbox 48.14 x 14.05 x 44.14 mm, 1935 faces (baked)
FEATURE [Part::Compound] Compound  label="ips7100s"
  Links = -> [Part__Feature104]
  Placement = pos=(24,-180,25) rot=(0,0,1;0.006109rad)
FEATURE [Part::Feature] Part__Feature126  label="scd30"
  Placement = pos=(-1e-15,-110,40) rot=(1,0,0;3.14159rad)
  shape: bbox 35.11 x 7.027 x 23.02 mm, 2292 faces, 25 solids (baked)
FEATURE [Part::Feature] Part__Feature127  label="Board"
  shape: bbox 25.4 x 25.4 x 1.57 mm, 211 faces (baked)
FEATURE [Part::Feature] Part__Feature128  label="QFN24_4MM"
  Placement = pos=(12.1412,14.4526,1.57) rot=(0,0,1;3.92699rad)
  shape: bbox 5.657 x 5.657 x 0.9 mm, 172 faces (baked)
FEATURE [Part::Feature] Part__Feature129  label="Part 5"
  shape: bbox 0.48 x 0.6603 x 0.6 mm, 14 faces (baked)
FEATURE [Part::Feature] Part__Feature130  label="Part 6"
  shape: bbox 0.48 x 0.6603 x 0.6 mm, 14 faces (baked)
FEATURE [Part::Feature] Part__Feature131  label="Part 4"
  shape: bbox 0.48 x 0.6603 x 0.6 mm, 14 faces (baked)
FEATURE [Part::Feature] Part__Feature132  label="Part 3"
  shape: bbox 0.48 x 0.6603 x 0.6 mm, 14 faces (baked)
FEATURE [Part::Feature] Part__Feature133  label="Part 010"
  shape: bbox 0.48 x 0.6603 x 0.6 mm, 14 faces (baked)
FEATURE [Part::Feature] Part__Feature134  label="Part 011"
  shape: bbox 3 x 1.4 x 1 mm, 10 faces (baked)
FEATURE [Part::Feature] Part__Feature135  label="Pin1"
  shape: bbox 0.6224 x 1.252 x 1.252 mm, 37 faces (baked)
FEATURE [Part::Feature] Part__Feature136  label="Pin2"
  shape: bbox 0.6224 x 1.252 x 1.252 mm, 37 faces (baked)
FEATURE [Part::Feature] Part__Feature137  label="CeramicBody"
  shape: bbox 1.8 x 1.23 x 1.23 mm, 10 faces (baked)
FEATURE [Part::Feature] Part__Feature138  label="0603-NO (1)"
  Placement = pos=(23.241,6.223,1.57) rot=(0,0,1;0rad)
  shape: bbox 1.7 x 0.9 x 0.55 mm, 52 faces, 3 solids (baked)
FEATURE [Part::Feature] Part__Feature139  label="0603-NO (2)"
  Placement = pos=(13.3858,8.4328,1.57) rot=(0,0,1;0rad)
  shape: bbox 1.7 x 0.9 x 0.55 mm, 52 faces, 3 solids (baked)
FEATURE [Part::Feature] Part__Feature140  label="0603-NO (3)"
  Placement = pos=(1.905,18.923,1.57) rot=(0,0,1;3.14159rad)
  shape: bbox 1.7 x 0.9 x 0.55 mm, 52 faces, 3 solids (baked)
FEATURE [Part::Feature] Part__Feature141  label="Pin1 (1)"
  shape: bbox 0.6224 x 1.252 x 1.252 mm, 37 faces (baked)
FEATURE [Part::Feature] Part__Feature142  label="Pin2 (1)"
  shape: bbox 0.6224 x 1.252 x 1.252 mm, 37 faces (baked)
FEATURE [Part::Feature] Part__Feature143  label="Pin1 (2)"
  shape: bbox 0.6224 x 1.252 x 1.252 mm, 37 faces (baked)
FEATURE [Part::Feature] Part__Feature144  label="Pin2 (2)"
  shape: bbox 0.6224 x 1.252 x 1.252 mm, 37 faces (baked)
FEATURE [Part::Feature] Part__Feature145  label="CeramicBody (2)"
  shape: bbox 1.8 x 1.23 x 1.23 mm, 10 faces (baked)
FEATURE [Part::Feature] Part__Feature146  label="CHIPLED_0603_NOOUTLINE"
  Placement = pos=(23.368,8.509,1.57) rot=(0,0,1;1.5708rad)
  shape: bbox 1.616 x 0.8 x 0.4 mm, 133 faces (baked)
FEATURE [Part::Feature] Part__Feature147  label="CHIPLED_0603_NOOUTLINE (1)"
  Placement = pos=(1.905,16.764,1.57) rot=(0,0,-1;1.5708rad)
  shape: bbox 1.616 x 0.8 x 0.4 mm, 133 faces (baked)
FEATURE [Part::Feature] Part__Feature148  label="JST_SH4"
  Placement = pos=(22.86,12.7,1.57) rot=(0,0,1;1.5708rad)
  shape: bbox 4.95 x 6 x 2.96 mm, 229 faces, 7 solids (baked)
FEATURE [Part::Feature] Part__Feature149  label="JST_SH4 (1)"
  Placement = pos=(2.54,12.7,1.57) rot=(0,0,-1;1.5708rad)
  shape: bbox 4.95 x 6 x 2.96 mm, 229 faces, 7 solids (baked)
FEATURE [Part::Feature] Part__Feature150  label="NEO3535_REVERSE"
  Placement = pos=(12.7,23.114,0) rot=(0,1,0;3.14159rad)
  shape: bbox 5.88 x 2.8 x 1.78 mm, 41 faces, 5 solids (baked)
FEATURE [Part::Feature] Part__Feature151  label="RESPACK_4X0603"
  Placement = pos=(22.86,18.415,1.57) rot=(0,0,1;3.14159rad)
  shape: bbox 3.2 x 1.6 x 0.61 mm, 172 faces (baked)
FEATURE [Part::Feature] Part__Feature152  label="SOT363"
  Placement = pos=(17.399,12.192,1.57) rot=(0,0,-1;1.5708rad)
  shape: bbox 2.208 x 2.208 x 1.121 mm, 178 faces, 4 solids (baked)
FEATURE [App::Part] _603_NO  label="0603-NO"
  Group = -> [Part__Feature135,Part__Feature136,Part__Feature137]
  Origin = -> Origin012
  Placement = pos=(16.51,8.382,1.57) rot=(0,0,1;0rad)
FEATURE [App::Part] _6700497  label="36700497"
  Group = -> [Part__Feature129,Part__Feature130,Part__Feature131,Part__Feature132,Part__Feature133,Part__Feature134]
  Origin = -> Origin010
  Placement = pos=(0,0,0) rot=(0,0,1;3.14159rad)
FEATURE [App::Part] SOT23_5  label="SOT23-5"
  Group = -> [_6700497]
  Origin = -> Origin011
  Placement = pos=(2.54,6.985,1.57) rot=(0,0,1;3.14159rad)
FEATURE [App::Part] _805_NO  label="0805-NO"
  Group = -> [Part__Feature141,Part__Feature142,Part__Feature040]
  Origin = -> Origin013
  Placement = pos=(7.874,13.589,1.57) rot=(0,0,1;1.5708rad)
FEATURE [App::Part] _805_NO__1_  label="0805-NO (1)"
  Group = -> [Part__Feature143,Part__Feature144,Part__Feature145]
  Origin = -> Origin014
  Placement = pos=(12.827,6.223,1.57) rot=(0,0,1;3.14159rad)
FEATURE [App::Part] Packages
  Group = -> [Part__Feature128,SOT23_5,_603_NO,Part__Feature138,Part__Feature139,Part__Feature140,_805_NO,_805_NO__1_,Part__Feature146,Part__Feature147,Part__Feature148,Part__Feature149,Part__Feature150,Part__Feature151,Part__Feature152]
  Origin = -> Origin015
FEATURE [App::Part] Adafruit_I2C_QT_Rotary_Encoder_v2  label="gps"
  Group = -> [Part__Feature127,Packages]
  Origin = -> Origin016
  Placement = pos=(-12.7,-163,95) rot=(0,0,1;0rad)
FEATURE [Sketcher::SketchObject] Sketch005  label="top007"
  FullyConstrained = true
  sketch-geometry (15):
    g0: Circle CenterX=0 CenterY=-150 CenterZ=0 NormalX=0 NormalY=0 NormalZ=1 AngleXU=0 Radius=85
    g1: Circle CenterX=-57 CenterY=-115 CenterZ=0 NormalX=0 NormalY=0 NormalZ=1 AngleXU=0 Radius=2.13
    g2: Circle CenterX=-22 CenterY=-150 CenterZ=0 NormalX=0 NormalY=0 NormalZ=1 AngleXU=0 Radius=4
    g3: Circle CenterX=-57 CenterY=-185 CenterZ=0 NormalX=0 NormalY=0 NormalZ=1 AngleXU=0 Radius=2.13
    g4: Circle CenterX=0 CenterY=-172 CenterZ=0 NormalX=0 NormalY=0 NormalZ=1 AngleXU=0 Radius=4
    g5: Circle CenterX=-35 CenterY=-207 CenterZ=0 NormalX=0 NormalY=0 NormalZ=1 AngleXU=0 Radius=2.13
    g6: Circle CenterX=35 CenterY=-207 CenterZ=0 NormalX=0 NormalY=0 NormalZ=1 AngleXU=0 Radius=2.13
    g7: Circle CenterX=57 CenterY=-185 CenterZ=0 NormalX=0 NormalY=0 NormalZ=1 AngleXU=0 Radius=2.13
    g8: Circle CenterX=22 CenterY=-150 CenterZ=0 NormalX=0 NormalY=0 NormalZ=1 AngleXU=0 Radius=4
    g9: Circle CenterX=57 CenterY=-115 CenterZ=0 NormalX=0 NormalY=0 NormalZ=1 AngleXU=0 Radius=2.13
    g10: Circle CenterX=0 CenterY=-207 CenterZ=0 NormalX=0 NormalY=0 NormalZ=1 AngleXU=0 Radius=4.5
    g11: Circle CenterX=57 CenterY=-150 CenterZ=0 NormalX=0 NormalY=0 NormalZ=1 AngleXU=0 Radius=21
    g12: Circle CenterX=-35 CenterY=-93 CenterZ=0 NormalX=0 NormalY=0 NormalZ=1 AngleXU=0 Radius=2.13
    g13: Circle CenterX=35 CenterY=-93 CenterZ=0 NormalX=0 NormalY=0 NormalZ=1 AngleXU=0 Radius=2.13
    g14: Circle CenterX=0 CenterY=-128 CenterZ=0 NormalX=0 NormalY=0 NormalZ=1 AngleXU=0 Radius=4
  constraints (45):
    c: Radius(g0) = 85
    c: DistanceY(g0) = -150
    c: DistanceY(g8,g0) = 0
    c: DistanceY(g0,g2) = 0
    c: Radius(g11) = 21
    c: DistanceX(g10,g0) = 0
    c: DistanceX(g0,g11) = 57
    c: DistanceY(g11,g0) = 0
    c: DistanceX(g0,g8) = 22
    c: DistanceX(g2,g0) = 22
    c: DistanceX(g5,g10) = 35
    c: DistanceX(g10,g6) = 35
    c: DistanceX(g7,g11) = 0
    c: DistanceX(g11,g9) = 0
    c: DistanceX(g1,g0) = 57
    c: DistanceY(g3,g0) = 35
    c: DistanceY(g0,g1) = 35
    c: DistanceY(g10,g4) = 35
    c: DistanceY(g6,g10) = 0
    c: DistanceY(g10,g5) = 0
    c: DistanceY(g7,g11) = 35
    c: DistanceY(g11,g9) = 35
    c: DistanceX(g3,g1) = 0
    c: DistanceY(g10,g0) = 57
    c: Diameter(g10) = 9
    c: DistanceX(g12) = -35
    c: DistanceX(g13) = 35
    c: DistanceY(g0,g14) = 22
    c: DistanceX(g0) = 0
    c: DistanceX(g4) = 0
    c: DistanceX(g14) = 0
    c: DistanceY(g0,g13) = 57
    c: DistanceY(g0,g12) = 57
    c: Equal(g5,g6)
    c: Equal(g5,g7)
    c: Equal(g5,g9)
    c: Equal(g5,g13)
    c: Equal(g5,g12)
    c: Equal(g5,g1)
    c: Equal(g5,g3)
    c: Radius(g5) = 2.13
    c: Equal(g4,g8)
    c: Equal(g4,g14)
    c: Equal(g4,g2)
    c: Diameter(g4) = 8
FEATURE [Part::Extrusion] Extrude005  label="level1"
  Base = -> Sketch005
  Dir = (0,0,1)
  DirMode = 2
  FaceMakerClass = Part::FaceMakerBullseye
  LengthFwd = 5
  LengthRev = 0
  Placement = pos=(0,0,75) rot=(0,0,1;0rad)
  Solid = true
  Symmetric = false
FEATURE [Part::Box] Box007  label="Cube001"
  AttacherType = Attacher::AttachEngine3D
  Height = 20
  Length = 30
  Placement = pos=(-72,-155,80) rot=(0,0,1;0rad)
  Width = 10
FEATURE [Part::MultiFuse] Fusion049  label="as7265Holder001"
  Shapes = -> [Box007,Extrude002]
FEATURE [Sketcher::SketchObject] Sketch006
  FullyConstrained = true
  sketch-geometry (6):
    g0: Circle CenterX=0 CenterY=-150 CenterZ=0 NormalX=0 NormalY=0 NormalZ=1 AngleXU=0 Radius=17.5
    g1: Circle CenterX=-10.15 CenterY=-140.15 CenterZ=0 NormalX=0 NormalY=0 NormalZ=1 AngleXU=0 Radius=1.65
    g2: Circle CenterX=10.15 CenterY=-140.15 CenterZ=0 NormalX=0 NormalY=0 NormalZ=1 AngleXU=0 Radius=1.65
    g3: Circle CenterX=10.15 CenterY=-160.45 CenterZ=0 NormalX=0 NormalY=0 NormalZ=1 AngleXU=0 Radius=1.65
    g4: Circle CenterX=-10.15 CenterY=-160.45 CenterZ=0 NormalX=0 NormalY=0 NormalZ=1 AngleXU=0 Radius=1.65
    g5: Circle CenterX=0 CenterY=-150 CenterZ=0 NormalX=0 NormalY=0 NormalZ=1 AngleXU=0 Radius=11
  constraints (17):
    c: DistanceY(g0) = -150
    c: DistanceX(g0) = 0
    c: Radius(g0) = 17.5
    c: Equal(g4,g3)
    c: Equal(g4,g2)
    c: Equal(g4,g1)
    c: Diameter(g4) = 3.3
    c: DistanceX(g1,g4) = 0
    c: DistanceY(g2,g1) = 0
    c: DistanceY(g3,g4) = 0
    c: DistanceX(g2,g3) = 0
    c: DistanceY(g4,g0) = 10.45
    c: DistanceY(g0,g1) = 9.85
    c: DistanceX(g3) = 10.15
    c: DistanceX(g4) = -10.15
    c: Coincident(g5,g0)
    c: Diameter(g5) = 22
FEATURE [Part::Extrusion] Extrude006  label="gpsHolder"
  Base = -> Sketch006
  Dir = (0,0,1)
  DirMode = 2
  FaceMakerClass = Part::FaceMakerBullseye
  LengthFwd = 15
  LengthRev = 0
  Placement = pos=(0,0,80) rot=(0,0,1;0rad)
  Solid = true
  Symmetric = false
FEATURE [Part::Box] Box008  label="Cube"
  AttacherType = Attacher::AttachEngine3D
  Height = 25
  Length = 10
  Placement = pos=(-5,-109.35,75) rot=(0,0,1;0rad)
  Width = 20
FEATURE [Part::MultiFuse] Fusion050  label="uvHolder001"
  Shapes = -> [Box008,Extrude004]
FEATURE [Part::Cylinder] Cylinder099  label="refModuleHold001"
  Angle = 360
  AttacherType = Attacher::AttachEngine3D
  FirstAngle = 0
  Height = 32
  Placement = pos=(0,-207,80) rot=(0,0,1;0rad)
  Radius = 12
  SecondAngle = 0
FEATURE [Part::MultiFuse] Fusion051  label="refModule"
  Shapes = -> [Cylinder095,Cylinder094]
FEATURE [Part::Cylinder] Cylinder100  label="refModules001"
  Angle = 360
  AttacherType = Attacher::AttachEngine3D
  FirstAngle = 0
  Height = 75
  Placement = pos=(0,-207,37) rot=(0,0,1;0rad)
  Radius = 3.75
  SecondAngle = 0
FEATURE [Part::Cylinder] Cylinder101  label="refModulesCoverCut002"
  Angle = 360
  AttacherType = Attacher::AttachEngine3D
  FirstAngle = 0
  Height = 60
  Placement = pos=(0,-207,37) rot=(0,0,1;0rad)
  Radius = 4.5
  SecondAngle = 0
FEATURE [Part::MultiFuse] Fusion052  label="refModule001Cut"
  Shapes = -> [Cylinder101,Cylinder100]
FEATURE [Part::Cut] Cut019  label="refModuleHold002"
  Base = -> Cylinder099
  Tool = -> Fusion052
FEATURE [Sketcher::SketchObject] Sketch007
  FullyConstrained = true
  Placement = pos=(0,0,0) rot=(1,0,0;1.5708rad)
  sketch-geometry (1):
    g0: Circle CenterX=0 CenterY=102.5 CenterZ=0 NormalX=0 NormalY=0 NormalZ=1 AngleXU=0 Radius=2
  constraints (3):
    c: PointOnObject(g0,g-2)
    c: DistanceY(g0) = 102.5
    c: Diameter(g0) = 4
FEATURE [Part::Extrusion] Extrude007  label="m3HeatSetInsertCut"
  Base = -> Sketch007
  Dir = (0,-1,-3e-16)
  DirMode = 2
  FaceMakerClass = Part::FaceMakerBullseye
  LengthFwd = 50
  LengthRev = 0
  Placement = pos=(0,-183.25,0) rot=(0,0,1;0rad)
  Solid = true
  Symmetric = false
FEATURE [Part::Cut] Cut020  label="refSensorHoldLev1"
  Base = -> Cut019
  Tool = -> Extrude007
FEATURE [Part::MultiFuse] Fusion053  label="level1SensorHolds"
  Shapes = -> [Fusion050,Cut020,Extrude006,Fusion049,Extrude003]
FEATURE [Part::MultiFuse] Fusion054  label="level001x"
  Shapes = -> [Fusion053,Extrude005]
FEATURE [Part::Feature] Part__Feature153  label="Printed Circuit Board001"
  shape: bbox 25.4 x 17.78 x 1.6 mm, 42 faces (baked)
FEATURE [Part::Feature] Part__Feature154  label="EAHC2835WD007"
  shape: bbox 3.513 x 2.813 x 0.7485 mm, 108 faces, 4 solids (baked)
FEATURE [Part::Feature] Part__Feature155  label="AS7341 v003"
  Placement = pos=(0,-0.339822,1.6) rot=(0,0,1;0rad)
  shape: bbox 2 x 3.1 x 1.1 mm, 267 faces, 26 solids (baked)
FEATURE [Part::Feature] Part__Feature156  label="CAPC-0805-T0.95-BN v004"
  Placement = pos=(-5.01759,-3.15294,1.6) rot=(0,0,1;0rad)
  shape: bbox 2.1 x 1.35 x 0.95 mm, 42 faces (baked)
FEATURE [Part::Feature] Part__Feature157  label="CAPC-0805-T0.95-BN v005"
  Placement = pos=(-5.48627,2.66154,1.6) rot=(0,0,-1;1.5708rad)
  shape: bbox 1.35 x 2.1 x 0.95 mm, 42 faces (baked)
FEATURE [Part::Feature] Part__Feature158  label="CAPC-0805-T0.95-BN v006"
  Placement = pos=(-3.43627,2.66154,1.6) rot=(0,0,-1;1.5708rad)
  shape: bbox 1.35 x 2.1 x 0.95 mm, 42 faces (baked)
FEATURE [Part::Feature] Part__Feature159  label="CAPC-0603-T0.9-BN v002"
  Placement = pos=(-1.69987,-3.28475,1.6) rot=(0,0,1;0rad)
  shape: bbox 1.7 x 0.9 x 0.9 mm, 42 faces (baked)
FEATURE [Part::Feature] Part__Feature160  label="BODY_MF06A001"
  Placement = pos=(0,0,0.762) rot=(0.57735,-0.57735,-0.57735;2.0944rad)
  shape: bbox 1.601 x 2.921 x 1.016 mm, 42 faces (baked)
FEATURE [Part::Feature] Part__Feature161  label="LEAD_MF06A006"
  Placement = pos=(-0.9652,-0.9525,0.1016) rot=(0.57735,-0.57735,-0.57735;2.0944rad)
  shape: bbox 0.6223 x 0.3749 x 0.8636 mm, 14 faces (baked)
FEATURE [Part::Feature] Part__Feature162  label="LEAD_MF06A007"
  Placement = pos=(-0.9652,0,0.1016) rot=(0.57735,-0.57735,-0.57735;2.0944rad)
  shape: bbox 0.6223 x 0.3749 x 0.8636 mm, 14 faces (baked)
FEATURE [Part::Feature] Part__Feature163  label="LEAD_MF06A008"
  Placement = pos=(-0.9652,0.9525,0.1016) rot=(0.57735,-0.57735,-0.57735;2.0944rad)
  shape: bbox 0.6223 x 0.3749 x 0.8636 mm, 14 faces (baked)
FEATURE [Part::Feature] Part__Feature164  label="LEAD_MF06A009"
  Placement = pos=(0.9652,-0.9525,0.1016) rot=(0.57735,0.57735,0.57735;2.0944rad)
  shape: bbox 0.6223 x 0.3749 x 0.8636 mm, 14 faces (baked)
FEATURE [Part::Feature] Part__Feature165  label="LEAD_MF06A010"
  Placement = pos=(0.9652,0,0.1016) rot=(0.57735,0.57735,0.57735;2.0944rad)
  shape: bbox 0.6223 x 0.3749 x 0.8636 mm, 14 faces (baked)
FEATURE [Part::Feature] Part__Feature166  label="LEAD_MF06A011"
  Placement = pos=(0.9652,0.9525,0.1016) rot=(0.57735,0.57735,0.57735;2.0944rad)
  shape: bbox 0.6223 x 0.3749 x 0.8636 mm, 14 faces (baked)
FEATURE [Part::Feature] Part__Feature167  label="SOT363 v003"
  Placement = pos=(4.97054,-0.645171,1.675) rot=(0,0,1;3.14159rad)
  shape: bbox 2.1 x 2 x 1.1 mm, 94 faces, 7 solids (baked)
FEATURE [Part::Feature] Part__Feature168  label="LED 0603 single color v002"
  Placement = pos=(-9.18406,3.72778,1.60762) rot=(0,0,1;1.5708rad)
  shape: bbox 1.961 x 0.7932 x 0.7145 mm, 63 faces, 5 solids (baked)
FEATURE [Part::Feature] Part__Feature169  label="RESC-0603 v003"
  Placement = pos=(4.83432,-3.67461,1.6) rot=(0,0,1;0rad)
  shape: bbox 1.7 x 0.9 x 0.55 mm, 52 faces, 3 solids (baked)
FEATURE [Part::Feature] Part__Feature170  label="RESC-0603 v004"
  Placement = pos=(-7.14949,3.61248,1.6) rot=(0,0,-1;1.5708rad)
  shape: bbox 0.9 x 1.7 x 0.55 mm, 52 faces, 3 solids (baked)
FEATURE [Part::Feature] Part__Feature171  label="YC164_RESPACK v002"
  Placement = pos=(2.99591,1.52916,1.6) rot=(0,0,1;0rad)
  shape: bbox 3.2 x 1.6 x 0.61 mm, 172 faces (baked)
FEATURE [Part::Feature] Part__Feature172  label="qwicc v004"
  Placement = pos=(-10.8364,0.0607456,1.65) rot=(0,0,-1;1.5708rad)
  shape: bbox 4.95 x 6 x 2.96 mm, 229 faces, 7 solids (baked)
FEATURE [Part::Feature] Part__Feature173  label="qwicc v005"
  Placement = pos=(10.8256,0.00556102,1.65) rot=(0,0,1;1.5708rad)
  shape: bbox 4.95 x 6 x 2.96 mm, 229 faces, 7 solids (baked)
FEATURE [App::Part] sot_23_6_v003  label="sot-23-6 v003"
  Group = -> [Part__Feature160,Part__Feature161,Part__Feature162,Part__Feature163,Part__Feature164,Part__Feature165,Part__Feature166]
  Origin = -> Origin017
  Placement = pos=(-4.47945,-0.603742,1.69152) rot=(0,0,1;0rad)
FEATURE [App::Part] Adafruit_AS7341_STEMMA_QT_v003  label="bme280"
  Group = -> [Part__Feature153,Part__Feature154,Part__Feature155,Part__Feature156,Part__Feature157,Part__Feature158,Part__Feature159,sot_23_6_v003,Part__Feature167,Part__Feature168,Part__Feature169,Part__Feature170,Part__Feature171,Part__Feature172,Part__Feature173]
  Origin = -> Origin018
  Placement = pos=(30,-149.75,45) rot=(0.57735,-0.57735,0.57735;4.18879rad)
FEATURE [Part::Cone] Cone
  Angle = 360
  AttacherType = Attacher::AttachEngine3D
  Height = 1.5
  Placement = pos=(0,0,25.5) rot=(0,0,1;0rad)
  Radius1 = 4
  Radius2 = 3.5
FEATURE [Part::Cylinder] Cylinder020
  Angle = 360
  AttacherType = Attacher::AttachEngine3D
  FirstAngle = 0
  Height = 22
  Placement = pos=(0,0,5) rot=(0,0,1;0rad)
  Radius = 3.2
  SecondAngle = 0
FEATURE [Part::Cylinder] Cylinder021
  Angle = 360
  AttacherType = Attacher::AttachEngine3D
  FirstAngle = 0
  Height = 2
  Placement = pos=(0,0,5) rot=(0,0,1;0rad)
  Radius = 3.55
  SecondAngle = 0
FEATURE [Part::Cylinder] Cylinder022
  Angle = 360
  AttacherType = Attacher::AttachEngine3D
  FirstAngle = 0
  Height = 1
  Placement = pos=(0,0,11) rot=(0,0,1;0rad)
  Radius = 3.55
  SecondAngle = 0
FEATURE [Part::Cylinder] Cylinder023
  Angle = 360
  AttacherType = Attacher::AttachEngine3D
  FirstAngle = 0
  Height = 8
  Placement = pos=(0,0,12) rot=(0,0,1;0rad)
  Radius = 3.25
  SecondAngle = 0
FEATURE [Part::Cylinder] Cylinder024
  Angle = 360
  AttacherType = Attacher::AttachEngine3D
  FirstAngle = 0
  Height = 5.5
  Placement = pos=(0,0,20) rot=(0,0,1;0rad)
  Radius = 4
  SecondAngle = 0
FEATURE [Part::Cylinder] Cylinder025
  Angle = 360
  AttacherType = Attacher::AttachEngine3D
  FirstAngle = 0
  Height = 2
  Placement = pos=(0,0,3) rot=(0,0,1;0rad)
  Radius = 1
  SecondAngle = 0
FEATURE [Part::MultiFuse] Fusion002
  Shapes = -> [Cone,Cylinder020,Cylinder021,Cylinder022,Cylinder023,Cylinder024]
FEATURE [Part::MultiFuse] Fusion055  label="mic"
  Placement = pos=(0,-212,-239.2) rot=(0,1,0;3.14159rad)
  Shapes = -> [Cylinder025,Fusion002]
FEATURE [Part::Feature] Part__Feature174  label="Printed Circuit Board002"
  shape: bbox 25.4 x 17.78 x 1.6 mm, 42 faces (baked)
FEATURE [Part::Feature] Part__Feature175  label="EAHC2835WD008"
  shape: bbox 3.513 x 2.813 x 0.7485 mm, 108 faces, 4 solids (baked)
FEATURE [Part::Feature] Part__Feature176  label="AS7341 v004"
  Placement = pos=(0,-0.339822,1.6) rot=(0,0,1;0rad)
  shape: bbox 2 x 3.1 x 1.1 mm, 267 faces, 26 solids (baked)
FEATURE [Part::Feature] Part__Feature177  label="CAPC-0805-T0.95-BN v007"
  Placement = pos=(-5.01759,-3.15294,1.6) rot=(0,0,1;0rad)
  shape: bbox 2.1 x 1.35 x 0.95 mm, 42 faces (baked)
FEATURE [Part::Feature] Part__Feature178  label="CAPC-0805-T0.95-BN v008"
  Placement = pos=(-5.48627,2.66154,1.6) rot=(0,0,-1;1.5708rad)
  shape: bbox 1.35 x 2.1 x 0.95 mm, 42 faces (baked)
FEATURE [Part::Feature] Part__Feature179  label="CAPC-0805-T0.95-BN v009"
  Placement = pos=(-3.43627,2.66154,1.6) rot=(0,0,-1;1.5708rad)
  shape: bbox 1.35 x 2.1 x 0.95 mm, 42 faces (baked)
FEATURE [Part::Feature] Part__Feature180  label="CAPC-0603-T0.9-BN v003"
  Placement = pos=(-1.69987,-3.28475,1.6) rot=(0,0,1;0rad)
  shape: bbox 1.7 x 0.9 x 0.9 mm, 42 faces (baked)
FEATURE [Part::Feature] Part__Feature181  label="BODY_MF06A002"
  Placement = pos=(0,0,0.762) rot=(0.57735,-0.57735,-0.57735;2.0944rad)
  shape: bbox 1.601 x 2.921 x 1.016 mm, 42 faces (baked)
FEATURE [Part::Feature] Part__Feature182  label="LEAD_MF06A012"
  Placement = pos=(-0.9652,-0.9525,0.1016) rot=(0.57735,-0.57735,-0.57735;2.0944rad)
  shape: bbox 0.6223 x 0.3749 x 0.8636 mm, 14 faces (baked)
FEATURE [Part::Feature] Part__Feature183  label="LEAD_MF06A013"
  Placement = pos=(-0.9652,0,0.1016) rot=(0.57735,-0.57735,-0.57735;2.0944rad)
  shape: bbox 0.6223 x 0.3749 x 0.8636 mm, 14 faces (baked)
FEATURE [Part::Feature] Part__Feature184  label="LEAD_MF06A014"
  Placement = pos=(-0.9652,0.9525,0.1016) rot=(0.57735,-0.57735,-0.57735;2.0944rad)
  shape: bbox 0.6223 x 0.3749 x 0.8636 mm, 14 faces (baked)
FEATURE [Part::Feature] Part__Feature185  label="LEAD_MF06A015"
  Placement = pos=(0.9652,-0.9525,0.1016) rot=(0.57735,0.57735,0.57735;2.0944rad)
  shape: bbox 0.6223 x 0.3749 x 0.8636 mm, 14 faces (baked)
FEATURE [Part::Feature] Part__Feature186  label="LEAD_MF06A016"
  Placement = pos=(0.9652,0,0.1016) rot=(0.57735,0.57735,0.57735;2.0944rad)
  shape: bbox 0.6223 x 0.3749 x 0.8636 mm, 14 faces (baked)
FEATURE [Part::Feature] Part__Feature187  label="LEAD_MF06A017"
  Placement = pos=(0.9652,0.9525,0.1016) rot=(0.57735,0.57735,0.57735;2.0944rad)
  shape: bbox 0.6223 x 0.3749 x 0.8636 mm, 14 faces (baked)
FEATURE [Part::Feature] Part__Feature188  label="SOT363 v004"
  Placement = pos=(4.97054,-0.645171,1.675) rot=(0,0,1;3.14159rad)
  shape: bbox 2.1 x 2 x 1.1 mm, 94 faces, 7 solids (baked)
FEATURE [Part::Feature] Part__Feature189  label="LED 0603 single color v003"
  Placement = pos=(-9.18406,3.72778,1.60762) rot=(0,0,1;1.5708rad)
  shape: bbox 1.961 x 0.7932 x 0.7145 mm, 63 faces, 5 solids (baked)
FEATURE [Part::Feature] Part__Feature190  label="RESC-0603 v005"
  Placement = pos=(4.83432,-3.67461,1.6) rot=(0,0,1;0rad)
  shape: bbox 1.7 x 0.9 x 0.55 mm, 52 faces, 3 solids (baked)
FEATURE [Part::Feature] Part__Feature191  label="RESC-0603 v006"
  Placement = pos=(-7.14949,3.61248,1.6) rot=(0,0,-1;1.5708rad)
  shape: bbox 0.9 x 1.7 x 0.55 mm, 52 faces, 3 solids (baked)
FEATURE [Part::Feature] Part__Feature192  label="YC164_RESPACK v003"
  Placement = pos=(2.99591,1.52916,1.6) rot=(0,0,1;0rad)
  shape: bbox 3.2 x 1.6 x 0.61 mm, 172 faces (baked)
FEATURE [Part::Feature] Part__Feature193  label="qwicc v006"
  Placement = pos=(-10.8364,0.0607456,1.65) rot=(0,0,-1;1.5708rad)
  shape: bbox 4.95 x 6 x 2.96 mm, 229 faces, 7 solids (baked)
FEATURE [Part::Feature] Part__Feature194  label="qwicc v007"
  Placement = pos=(10.8256,0.00556102,1.65) rot=(0,0,1;1.5708rad)
  shape: bbox 4.95 x 6 x 2.96 mm, 229 faces, 7 solids (baked)
FEATURE [App::Part] sot_23_6_v004  label="sot-23-6 v004"
  Group = -> [Part__Feature181,Part__Feature182,Part__Feature183,Part__Feature184,Part__Feature185,Part__Feature186,Part__Feature187]
  Origin = -> Origin019
  Placement = pos=(-4.47945,-0.603742,1.69152) rot=(0,0,1;0rad)
FEATURE [App::Part] Adafruit_AS7341_STEMMA_QT_v004  label="bme281"
  Group = -> [Part__Feature174,Part__Feature175,Part__Feature176,Part__Feature177,Part__Feature178,Part__Feature179,Part__Feature180,sot_23_6_v004,Part__Feature188,Part__Feature189,Part__Feature190,Part__Feature191,Part__Feature192,Part__Feature193,Part__Feature194]
  Origin = -> Origin020
  Placement = pos=(-30,-149.75,45) rot=(-0.57735,-0.57735,0.57735;2.0944rad)
FEATURE [Sketcher::SketchObject] Sketch008  label="top008"
  FullyConstrained = true
  sketch-geometry (15):
    g0: Circle CenterX=0 CenterY=-150 CenterZ=0 NormalX=0 NormalY=0 NormalZ=1 AngleXU=0 Radius=85
    g1: Circle CenterX=-57 CenterY=-115 CenterZ=0 NormalX=0 NormalY=0 NormalZ=1 AngleXU=0 Radius=2.125
    g2: Circle CenterX=-22 CenterY=-150 CenterZ=0 NormalX=0 NormalY=0 NormalZ=1 AngleXU=0 Radius=4
    g3: Circle CenterX=-57 CenterY=-185 CenterZ=0 NormalX=0 NormalY=0 NormalZ=1 AngleXU=0 Radius=2.125
    g4: Circle CenterX=0 CenterY=-172 CenterZ=0 NormalX=0 NormalY=0 NormalZ=1 AngleXU=0 Radius=4
    g5: Circle CenterX=-35 CenterY=-207 CenterZ=0 NormalX=0 NormalY=0 NormalZ=1 AngleXU=0 Radius=2.125
    g6: Circle CenterX=35 CenterY=-207 CenterZ=0 NormalX=0 NormalY=0 NormalZ=1 AngleXU=0 Radius=2.125
    g7: Circle CenterX=57 CenterY=-185 CenterZ=0 NormalX=0 NormalY=0 NormalZ=1 AngleXU=0 Radius=2.125
    g8: Circle CenterX=22 CenterY=-150 CenterZ=0 NormalX=0 NormalY=0 NormalZ=1 AngleXU=0 Radius=4
    g9: Circle CenterX=57 CenterY=-115 CenterZ=0 NormalX=0 NormalY=0 NormalZ=1 AngleXU=0 Radius=2.125
    g10: Circle CenterX=0 CenterY=-207 CenterZ=0 NormalX=0 NormalY=0 NormalZ=1 AngleXU=0 Radius=4.5
    g11: Circle CenterX=57 CenterY=-150 CenterZ=0 NormalX=0 NormalY=0 NormalZ=1 AngleXU=0 Radius=21
    g12: Circle CenterX=-35 CenterY=-93 CenterZ=0 NormalX=0 NormalY=0 NormalZ=1 AngleXU=0 Radius=2.125
    g13: Circle CenterX=35 CenterY=-93 CenterZ=0 NormalX=0 NormalY=0 NormalZ=1 AngleXU=0 Radius=2.125
    g14: Circle CenterX=0 CenterY=-128 CenterZ=0 NormalX=0 NormalY=0 NormalZ=1 AngleXU=0 Radius=4
  constraints (45):
    c: PointOnObject(g0,g-2)
    c: Radius(g0) = 85
    c: DistanceY(g0) = -150
    c: PointOnObject(g4,g-2)
    c: PointOnObject(g14,g-2)
    c: DistanceY(g8,g0) = 0
    c: DistanceY(g0,g2) = 0
    c: Radius(g11) = 21
    c: DistanceX(g10,g0) = 0
    c: DistanceX(g0,g11) = 57
    c: DistanceY(g11,g0) = 0
    c: DistanceX(g0,g8) = 22
    c: DistanceX(g2,g0) = 22
    c: DistanceX(g5,g10) = 35
    c: DistanceX(g10,g6) = 35
    c: DistanceX(g7,g11) = 0
    c: DistanceX(g11,g9) = 0
    c: DistanceX(g1,g0) = 57
    c: DistanceY(g3,g0) = 35
    c: DistanceY(g0,g1) = 35
    c: DistanceY(g10,g4) = 35
    c: DistanceY(g6,g10) = 0
    c: DistanceY(g10,g5) = 0
    c: DistanceY(g7,g11) = 35
    c: DistanceY(g11,g9) = 35
    c: DistanceX(g3,g1) = 0
    c: DistanceY(g10,g0) = 57
    c: Diameter(g10) = 9
    c: DistanceX(g12,g0) = 35
    c: DistanceY(g0,g13) = 57
    c: DistanceX(g0,g13) = 35
    c: Equal(g1,g12)
    c: Equal(g1,g13)
    c: Equal(g1,g9)
    c: Equal(g1,g7)
    c: Equal(g1,g6)
    c: Equal(g1,g5)
    c: Equal(g1,g3)
    c: Diameter(g1) = 4.25
    c: Equal(g4,g8)
    c: Equal(g4,g14)
    c: Equal(g4,g2)
    c: Diameter(g4) = 8
    c: DistanceY(g0,g14) = 22
    c: DistanceY(g0,g12) = 57
FEATURE [Part::Extrusion] Extrude008  label="level002"
  Base = -> Sketch008
  Dir = (0,0,1)
  DirMode = 2
  FaceMakerClass = Part::FaceMakerBullseye
  LengthFwd = 5
  LengthRev = 0
  Placement = pos=(0,0,15) rot=(0,0,1;0rad)
  Solid = true
  Symmetric = false
FEATURE [Part::Box] Box009  label="Cube002"
  AttacherType = Attacher::AttachEngine3D
  Height = 15
  Length = 10
  Placement = pos=(-25,-180,20) rot=(0,0,1;0rad)
  Width = 10
FEATURE [Part::Box] Box010  label="Cube003"
  AttacherType = Attacher::AttachEngine3D
  Height = 50
  Length = 10
  Placement = pos=(15,-180,20) rot=(0,0,1;0rad)
  Width = 10
FEATURE [Part::Box] Box011  label="Cube004"
  AttacherType = Attacher::AttachEngine3D
  Height = 35
  Length = 10
  Placement = pos=(20,-165,20) rot=(0,0,1;0rad)
  Width = 10
FEATURE [Part::Box] Box012  label="Cube005"
  AttacherType = Attacher::AttachEngine3D
  Height = 35
  Length = 10
  Placement = pos=(-30,-165,20) rot=(0,0,1;0rad)
  Width = 10
FEATURE [Part::Box] Box013  label="Cube006"
  AttacherType = Attacher::AttachEngine3D
  Height = 35
  Length = 10
  Placement = pos=(-30,-145,20) rot=(0,0,1;0rad)
  Width = 10
FEATURE [Part::Box] Box014  label="Cube007"
  AttacherType = Attacher::AttachEngine3D
  Height = 35
  Length = 10
  Placement = pos=(20,-145,20) rot=(0,0,1;0rad)
  Width = 10
FEATURE [Part::Box] Box015  label="Cube008"
  AttacherType = Attacher::AttachEngine3D
  Height = 35
  Length = 10
  Placement = pos=(-20,-130,20) rot=(0,0,1;0rad)
  Width = 10
FEATURE [Part::Box] Box016  label="Cube009"
  AttacherType = Attacher::AttachEngine3D
  Height = 17.5
  Length = 10
  Placement = pos=(12.5,-130,20) rot=(0,0,1;0rad)
  Width = 10
FEATURE [Part::MultiFuse] Fusion056  label="airSensorHolds"
  Shapes = -> [Box016,Box009,Box010,Box011,Box012,Box013,Box014,Box015]
FEATURE [Part::Cylinder] Cylinder102  label="m2Cuts"
  Angle = 360
  AttacherType = Attacher::AttachEngine3D
  FirstAngle = 0
  Height = 10
  Placement = pos=(-20.4,-170,28.6) rot=(1,0,0;1.5708rad)
  Radius = 1.13
  SecondAngle = 0
FEATURE [Part::Cylinder] Cylinder103  label="m2Cuts001"
  Angle = 360
  AttacherType = Attacher::AttachEngine3D
  FirstAngle = 0
  Height = 10
  Placement = pos=(20.4,-170,65.4) rot=(1,0,0;1.5708rad)
  Radius = 1.13
  SecondAngle = 0
FEATURE [Part::Cylinder] Cylinder104  label="m2Cuts002"
  Angle = 360
  AttacherType = Attacher::AttachEngine3D
  FirstAngle = 0
  Height = 10
  Placement = pos=(17.45,-120,33.2) rot=(1,0,0;1.5708rad)
  Radius = 1.13
  SecondAngle = 0
FEATURE [Part::Cylinder] Cylinder105  label="m2Cuts003"
  Angle = 360
  AttacherType = Attacher::AttachEngine3D
  FirstAngle = 0
  Height = 10
  Placement = pos=(-14.55,-120,49.4) rot=(1,0,0;1.5708rad)
  Radius = 1.1
  SecondAngle = 0
FEATURE [Part::Cylinder] Cylinder106  label="m2Cuts004"
  Angle = 360
  AttacherType = Attacher::AttachEngine3D
  FirstAngle = 0
  Height = 60
  Placement = pos=(-30,-159.9,38.65) rot=(0.57735,0.57735,0.57735;2.0944rad)
  Radius = 1.13
  SecondAngle = 0
FEATURE [Part::Cylinder] Cylinder107  label="m2Cuts005"
  Angle = 360
  AttacherType = Attacher::AttachEngine3D
  FirstAngle = 0
  Height = 60
  Placement = pos=(-30,-139.6,38.65) rot=(0.57735,0.57735,0.57735;2.0944rad)
  Radius = 1.13
  SecondAngle = 0
FEATURE [Part::Cylinder] Cylinder108  label="m2Cuts006"
  Angle = 360
  AttacherType = Attacher::AttachEngine3D
  FirstAngle = 0
  Height = 60
  Placement = pos=(-30,-159.9,51.35) rot=(0.57735,0.57735,0.57735;2.0944rad)
  Radius = 1.13
  SecondAngle = 0
FEATURE [Part::Cylinder] Cylinder109  label="m2Cuts007"
  Angle = 360
  AttacherType = Attacher::AttachEngine3D
  FirstAngle = 0
  Height = 60
  Placement = pos=(-30,-139.6,51.35) rot=(0.57735,0.57735,0.57735;2.0944rad)
  Radius = 1.13
  SecondAngle = 0
FEATURE [Part::MultiFuse] Fusion057  label="m2Cuts008"
  Shapes = -> [Cylinder109,Cylinder102,Cylinder103,Cylinder104,Cylinder105,Cylinder106,Cylinder107,Cylinder108]
FEATURE [Part::Cut] Cut021  label="airSesnorHolds"
  Base = -> Fusion056
  Tool = -> Fusion057
FEATURE [Sketcher::SketchObject] Sketch028
  FullyConstrained = true
  sketch-geometry (16):
    g0: ArcOfCircle CenterX=0 CenterY=-150 CenterZ=0 NormalX=0 NormalY=0 NormalZ=1 AngleXU=0 Radius=85 StartAngle=2.84306 EndAngle=3.44012
    g1: ArcOfCircle CenterX=0 CenterY=-150 CenterZ=0 NormalX=0 NormalY=0 NormalZ=1 AngleXU=0 Radius=85 StartAngle=1.27226 EndAngle=1.86933
    g2: ArcOfCircle CenterX=0 CenterY=-150 CenterZ=0 NormalX=0 NormalY=0 NormalZ=1 AngleXU=0 Radius=85 StartAngle=5.98465 EndAngle=6.58172
    g3: ArcOfCircle CenterX=0 CenterY=-150 CenterZ=0 NormalX=0 NormalY=0 NormalZ=1 AngleXU=0 Radius=85 StartAngle=4.41386 EndAngle=5.01092
    g4: ArcOfCircle CenterX=0 CenterY=-150 CenterZ=0 NormalX=0 NormalY=0 NormalZ=1 AngleXU=0 Radius=79 StartAngle=1.24881 EndAngle=1.89279
    g5: ArcOfCircle CenterX=0 CenterY=-150 CenterZ=0 NormalX=0 NormalY=0 NormalZ=1 AngleXU=0 Radius=79 StartAngle=5.96119 EndAngle=6.60518
    g6: ArcOfCircle CenterX=0 CenterY=-150 CenterZ=0 NormalX=0 NormalY=0 NormalZ=1 AngleXU=0 Radius=79 StartAngle=2.8196 EndAngle=3.46358
    g7: ArcOfCircle CenterX=0 CenterY=-150 CenterZ=0 NormalX=0 NormalY=0 NormalZ=1 AngleXU=0 Radius=79 StartAngle=4.3904 EndAngle=5.03438
    g8: LineSegment StartX=25 StartY=-68.7596 StartZ=0 EndX=25 EndY=-75.06 EndZ=0
    g9: LineSegment StartX=-25 StartY=-68.7596 StartZ=0 EndX=-25 EndY=-75.06 EndZ=0
    g10: LineSegment StartX=-81.2404 StartY=-125 StartZ=0 EndX=-74.94 EndY=-125 EndZ=0
    g11: LineSegment StartX=-81.2404 StartY=-175 StartZ=0 EndX=-74.94 EndY=-175 EndZ=0
    g12: LineSegment StartX=-25 StartY=-231.24 StartZ=0 EndX=-25 EndY=-224.94 EndZ=0
    g13: LineSegment StartX=25 StartY=-231.24 StartZ=0 EndX=25 EndY=-224.94 EndZ=0
    g14: LineSegment StartX=81.2404 StartY=-175 StartZ=0 EndX=74.94 EndY=-175 EndZ=0
    g15: LineSegment StartX=81.2404 StartY=-125 StartZ=0 EndX=74.94 EndY=-125 EndZ=0
  constraints (49):
    c: PointOnObject(g0,g-2)
    c: Coincident(g1,g0)
    c: Coincident(g2,g0)
    c: Coincident(g3,g0)
    c: DistanceY(g0) = -150
    c: Coincident(g4,g0)
    c: Coincident(g5,g0)
    c: Coincident(g6,g0)
    c: Coincident(g7,g0)
    c: DistanceX(g4,g0) = 25
    c: DistanceX(g1,g4) = 0
    c: DistanceX(g0,g4) = 25
    c: DistanceX(g4,g1) = 0
    c: DistanceY(g0,g5) = 25
    c: DistanceY(g5,g2) = 0
    c: DistanceY(g2,g0) = 25
    c: DistanceY(g2,g5) = 0
    c: DistanceY(g6,g0) = 25
    c: DistanceY(g0,g6) = 0
    c: DistanceY(g0,g6) = 25
    c: DistanceY(g6,g0) = 0
    c: Equal(g1,g2)
    c: Equal(g1,g3)
    c: Equal(g1,g0)
    c: Radius(g1) = 85  'outer'
    c: Equal(g6,g4)
    c: Equal(g6,g5)
    c: Equal(g6,g7)
    c: Radius(g6) = 79
    c: DistanceX(g0,g7) = 25
    c: DistanceX(g7,g3) = 0
    c: DistanceX(g3) = -25
    c: DistanceX(g3,g7) = 0
    c: Coincident(g8,g1)
    c: Coincident(g8,g4)
    c: Coincident(g9,g1)
    c: Coincident(g9,g4)
    c: Coincident(g10,g0)
    c: Coincident(g10,g6)
    c: Coincident(g11,g0)
    c: Coincident(g11,g6)
    c: Coincident(g12,g3)
    c: Coincident(g12,g7)
    c: Coincident(g13,g3)
    c: Coincident(g13,g7)
    c: Coincident(g14,g2)
    c: Coincident(g14,g5)
    c: Coincident(g15,g2)
    c: Coincident(g15,g5)
FEATURE [Part::Extrusion] Extrude010  label="srsHolds"
  Base = -> Sketch028
  Dir = (0,0,1)
  DirMode = 2
  FaceMakerClass = Part::FaceMakerBullseye
  LengthFwd = 20
  LengthRev = 0
  Placement = pos=(0,0,75) rot=(0,0,1;0rad)
  Solid = true
  Symmetric = false
FEATURE [Part::MultiFuse] Fusion063  label="level2"
  Shapes = -> [Cut021,Extrude008]
FEATURE [Sketcher::SketchObject] Sketch030  label="top011"
  FullyConstrained = true
  sketch-geometry (10):
    g0: Circle CenterX=-57 CenterY=-115 CenterZ=0 NormalX=0 NormalY=0 NormalZ=1 AngleXU=0 Radius=2.125
    g1: Circle CenterX=-57 CenterY=-185 CenterZ=0 NormalX=0 NormalY=0 NormalZ=1 AngleXU=0 Radius=2.125
    g2: Circle CenterX=-35 CenterY=-207 CenterZ=0 NormalX=0 NormalY=0 NormalZ=1 AngleXU=0 Radius=2.125
    g3: Circle CenterX=-35 CenterY=-93 CenterZ=0 NormalX=0 NormalY=0 NormalZ=1 AngleXU=0 Radius=2.125
    g4: Circle CenterX=-4.2 CenterY=-109.55 CenterZ=0 NormalX=0 NormalY=0 NormalZ=1 AngleXU=0 Radius=1.5
    g5: Circle CenterX=-58.33 CenterY=-148.9 CenterZ=0 NormalX=0 NormalY=0 NormalZ=1 AngleXU=0 Radius=1.5
    g6: Circle CenterX=-4.2 CenterY=-180.9 CenterZ=0 NormalX=0 NormalY=0 NormalZ=1 AngleXU=0 Radius=1.5
    g7: Circle CenterX=0 CenterY=-150 CenterZ=0 NormalX=0 NormalY=0 NormalZ=1 AngleXU=0 Radius=92.5
    g8: ArcOfCircle CenterX=0 CenterY=-150 CenterZ=0 NormalX=0 NormalY=0 NormalZ=1 AngleXU=0 Radius=78 StartAngle=4.71239 EndAngle=7.85398
    g9: LineSegment StartX=2.39e-14 StartY=-72 StartZ=0 EndX=-1.43e-14 EndY=-228 EndZ=0
  constraints (30):
    c: DistanceX(g1,g0) = 0
    c: Equal(g0,g3)
    c: Equal(g0,g2)
    c: Equal(g0,g1)
    c: Diameter(g0) = 4.25
    c: DistanceY(g6) = -180.9
    c: DistanceX(g4,g6) = 0
    c: DistanceY(g6,g4) = 71.35
    c: DistanceX(g5,g6) = 54.13
    c: DistanceY(g6,g5) = 32
    c: Equal(g5,g6)
    c: Equal(g5,g4)
    c: Diameter(g5) = 3
    c: PointOnObject(g7,g-2)
    c: Diameter(g7) = 185
    c: DistanceY(g7) = -150
    c: DistanceX(g1,g7) = 57
    c: DistanceY(g1,g7) = 35
    c: DistanceY(g7,g0) = 35
    c: DistanceX(g3,g7) = 35
    c: DistanceY(g7,g3) = 57
    c: DistanceX(g4) = -4.2
    c: Coincident(g8,g7)
    c: PointOnObject(g8,g-2)
    c: DistanceX(g7,g8) = 0
    c: Coincident(g9,g8)
    c: Coincident(g9,g8)
    c: Diameter(g8) = 156
    c: DistanceX(g2) = -35
    c: DistanceY(g2,g7) = 57
FEATURE [Part::Extrusion] Extrude012  label="level003"
  Base = -> Sketch030
  Dir = (0,0,1)
  DirMode = 2
  FaceMakerClass = Part::FaceMakerBullseye
  LengthFwd = 5
  LengthRev = 0
  Placement = pos=(0,0,-60) rot=(0,0,1;0rad)
  Solid = true
  Symmetric = false
FEATURE [Part::Feature] Part__Feature195  label="srsRefLightModuke"
  Placement = pos=(-15,-170,-30) rot=(0.57735,-0.57735,0.57735;4.18879rad)
  shape: bbox 63.5 x 88.9 x 31.45 mm, 876 faces (baked)
FEATURE [Part::Cylinder] Cylinder114
  Angle = 270
  AttacherType = Attacher::AttachEngine3D
  FirstAngle = 0
  Height = 30
  Placement = pos=(0,-150,0) rot=(0,0,1;1.5708rad)
  Radius = 82
  SecondAngle = 0
FEATURE [Part::Cylinder] Cylinder115
  Angle = 270
  AttacherType = Attacher::AttachEngine3D
  FirstAngle = 0
  Height = 30
  Placement = pos=(0,-150,0) rot=(0,0,1;1.5708rad)
  Radius = 78
  SecondAngle = 0
FEATURE [Part::Cut] Cut028
  Base = -> Cylinder114
  Placement = pos=(0,0,-55) rot=(0,0,1;0rad)
  Tool = -> Cylinder115
FEATURE [Part::FeaturePython] Tube002  label="tube3to2"  # WARN: FeaturePython — macro-defined, semantics opaque (R4)
  AttacherType = Attacher::AttachEngine3D
  Height = 80
  InnerRadius = 94
  OuterRadius = 98
  Placement = pos=(0,-150,-60) rot=(0,0,1;0rad)
FEATURE [Part::MultiFuse] Fusion067  label="level3"
  Shapes = -> [Extrude012,Cut028]
FEATURE [Part::Cylinder] Cylinder121
  Angle = 360
  AttacherType = Attacher::AttachEngine3D
  FirstAngle = 0
  Height = 300
  Placement = pos=(0,0,90) rot=(1,0,0;1.5708rad)
  Radius = 2.8
  SecondAngle = 0
FEATURE [Part::Cylinder] Cylinder122
  Angle = 360
  AttacherType = Attacher::AttachEngine3D
  FirstAngle = 0
  Height = 300
  Placement = pos=(-150,-150,90) rot=(0.57735,0.57735,0.57735;2.0944rad)
  Radius = 2.8
  SecondAngle = 0
FEATURE [Part::MultiFuse] Fusion068  label="m4Cuts002"
  Shapes = -> [Cylinder122,Cylinder121]
FEATURE [Part::Cut] Cut032  label="srsHold"
  Base = -> Extrude010
  Tool = -> Fusion068
FEATURE [Part::MultiFuse] Fusion069  label="level001"
  Shapes = -> [Cut032,Fusion054]
FEATURE [Sketcher::SketchObject] Sketch032
  FullyConstrained = true
  sketch-geometry (16):
    g0: ArcOfCircle CenterX=0 CenterY=-150 CenterZ=0 NormalX=0 NormalY=0 NormalZ=1 AngleXU=0 Radius=92.5 StartAngle=3.68087 EndAngle=4.17311
    g1: ArcOfCircle CenterX=0 CenterY=-150 CenterZ=0 NormalX=0 NormalY=0 NormalZ=1 AngleXU=0 Radius=92.5 StartAngle=2.11007 EndAngle=2.60232
    g2: ArcOfCircle CenterX=0 CenterY=-150 CenterZ=0 NormalX=0 NormalY=0 NormalZ=1 AngleXU=0 Radius=92.5 StartAngle=0.539274 EndAngle=1.03152
    g3: ArcOfCircle CenterX=0 CenterY=-150 CenterZ=0 NormalX=0 NormalY=0 NormalZ=1 AngleXU=0 Radius=92.5 StartAngle=5.25166 EndAngle=5.74391
    g4: ArcOfCircle CenterX=0 CenterY=-150 CenterZ=0 NormalX=0 NormalY=0 NormalZ=1 AngleXU=0 Radius=85 StartAngle=2.1287 EndAngle=2.58369
    g5: ArcOfCircle CenterX=0 CenterY=-150 CenterZ=0 NormalX=0 NormalY=0 NormalZ=1 AngleXU=0 Radius=85 StartAngle=0.557907 EndAngle=1.01289
    g6: ArcOfCircle CenterX=0 CenterY=-150 CenterZ=0 NormalX=0 NormalY=0 NormalZ=1 AngleXU=0 Radius=85 StartAngle=3.6995 EndAngle=4.15448
    g7: ArcOfCircle CenterX=0 CenterY=-150 CenterZ=0 NormalX=0 NormalY=0 NormalZ=1 AngleXU=0 Radius=85 StartAngle=5.2703 EndAngle=5.72528
    g8: LineSegment StartX=-47.5 StartY=-70.6275 StartZ=0 EndX=-45 EndY=-77.889 EndZ=0
    g9: LineSegment StartX=-79.3725 StartY=-102.5 StartZ=0 EndX=-72.111 EndY=-105 EndZ=0
    g10: LineSegment StartX=-79.3725 StartY=-197.5 StartZ=0 EndX=-72.111 EndY=-195 EndZ=0
    g11: LineSegment StartX=-47.5 StartY=-229.373 StartZ=0 EndX=-45 EndY=-222.111 EndZ=0
    g12: LineSegment StartX=47.5 StartY=-229.373 StartZ=0 EndX=45 EndY=-222.111 EndZ=0
    g13: LineSegment StartX=79.3725 StartY=-102.5 StartZ=0 EndX=72.111 EndY=-105 EndZ=0
    g14: LineSegment StartX=47.5 StartY=-70.6275 StartZ=0 EndX=45 EndY=-77.889 EndZ=0
    g15: LineSegment StartX=72.111 StartY=-195 StartZ=0 EndX=79.3725 EndY=-197.5 EndZ=0
  constraints (49):
    c: Coincident(g1,g0)
    c: Coincident(g2,g0)
    c: DistanceY(g0) = -150
    c: Coincident(g4,g0)
    c: Coincident(g5,g0)
    c: Coincident(g6,g0)
    c: Coincident(g8,g1)
    c: Coincident(g8,g4)
    c: Coincident(g9,g1)
    c: Coincident(g10,g0)
    c: Coincident(g10,g6)
    c: Coincident(g11,g0)
    c: Coincident(g11,g6)
    c: Coincident(g12,g7)
    c: Coincident(g13,g2)
    c: Coincident(g13,g5)
    c: Coincident(g14,g2)
    c: Coincident(g14,g5)
    c: Coincident(g3,g12)
    c: Coincident(g9,g4)
    c: Coincident(g3,g15)
    c: Coincident(g15,g7)
    c: Coincident(g3,g0)
    c: Coincident(g7,g0)
    c: Equal(g7,g6)
    c: Equal(g7,g4)
    c: Equal(g7,g5)
    c: Diameter(g7) = 170
    c: DistanceX(g0) = 0
    c: Equal(g3,g0)
    c: Equal(g3,g2)
    c: Equal(g3,g1)
    c: Diameter(g3) = 185
    c: DistanceY(g0,g4) = 45
    c: DistanceX(g4,g0) = 45
    c: DistanceX(g4,g6) = 0
    c: DistanceX(g6,g4) = 0
    c: DistanceY(g5,g4) = 0
    c: DistanceY(g5,g4) = 0
    c: DistanceX(g7,g5) = 0
    c: DistanceY(g6,g7) = 0
    c: DistanceY(g5,g2) = 2.5
    c: DistanceX(g5,g2) = 2.5
    c: DistanceY(g1,g2) = 0
    c: DistanceY(g2,g1) = 0
    c: DistanceX(g1,g0) = 0
    c: DistanceX(g0,g1) = 0
    c: DistanceX(g2,g3) = 0
    c: DistanceY(g3,g0) = 0
FEATURE [Part::Extrusion] Extrude014
  Base = -> Sketch032
  Dir = (0,0,1)
  DirMode = 2
  FaceMakerClass = Part::FaceMakerBullseye
  LengthFwd = 20
  LengthRev = 0
  Solid = true
  Symmetric = false
FEATURE [Part::MultiFuse] Fusion070  label="level02"
  Shapes = -> [Fusion063,Extrude014]
FEATURE [Part::Cylinder] Cylinder127
  Angle = 360
  AttacherType = Attacher::AttachEngine3D
  FirstAngle = 0
  Height = 300
  Placement = pos=(0,0,90) rot=(1,0,0;1.5708rad)
  Radius = 2.8
  SecondAngle = 0
FEATURE [Part::Cylinder] Cylinder128
  Angle = 360
  AttacherType = Attacher::AttachEngine3D
  FirstAngle = 0
  Height = 300
  Placement = pos=(-150,-150,90) rot=(0.57735,0.57735,0.57735;2.0944rad)
  Radius = 2.8
  SecondAngle = 0
FEATURE [Part::Cylinder] Cylinder129
  Angle = 360
  AttacherType = Attacher::AttachEngine3D
  FirstAngle = 0
  Height = 300
  Placement = pos=(106.066,-43.934,90) rot=(0.862856,-0.357407,-0.357407;1.71777rad)
  Radius = 2.8
  SecondAngle = 0
FEATURE [Part::Cylinder] Cylinder130
  Angle = 360
  AttacherType = Attacher::AttachEngine3D
  FirstAngle = 0
  Height = 300
  Placement = pos=(-106.066,-43.934,90) rot=(0.862856,0.357407,0.357407;1.71777rad)
  Radius = 2.8
  SecondAngle = 0
FEATURE [Part::MultiFuse] Fusion074  label="m4Cuts006"
  Placement = pos=(0,0,-82) rot=(0,0,1;0rad)
  Shapes = -> [Cylinder128,Cylinder127]
FEATURE [Part::MultiFuse] Fusion075  label="m4Cuts007"
  Placement = pos=(0,0,-82) rot=(0,0,1;0rad)
  Shapes = -> [Cylinder129,Cylinder130]
FEATURE [Part::MultiFuse] Fusion076  label="m4Cuts008"
  Shapes = -> [Fusion074,Fusion075]
FEATURE [Part::Cut] Cut034  label="level002s"
  Base = -> Fusion070
  Tool = -> Fusion076
FEATURE [Part::Feature] Part__Feature197  label="CUI_VGS-75C-15"
  Placement = pos=(-32,-169,-130) rot=(0.57735,-0.57735,-0.57735;4.18879rad)
  shape: bbox 30.06 x 99.03 x 97.03 mm, 2447 faces, 17 solids (baked)
FEATURE [Part::Feature] Part__Feature198  label="F9 body"
  Placement = pos=(-78.1983,5.70939,50.7544) rot=(0,0,1;0rad)
  shape: bbox 118.8 x 26.53 x 118.8 mm, 173 faces (baked)
FEATURE [Part::Feature] Part__Feature199  label="F9 fan"
  Placement = pos=(-74.2115,10.4094,-44.9134) rot=(0,-1,0;1.65409rad)
  shape: bbox 98.04 x 20 x 97.21 mm, 60 faces (baked)
FEATURE [App::Part] F9  label="fan"
  Group = -> [Part__Feature198,Part__Feature199]
  Origin = -> Origin
  Placement = pos=(32.25,-101,-138.5) rot=(0,0,1;0rad)
FEATURE [Sketcher::SketchObject] Sketch033  label="top012"
  FullyConstrained = true
  sketch-geometry (6):
    g0: Circle CenterX=0 CenterY=-150 CenterZ=0 NormalX=0 NormalY=0 NormalZ=1 AngleXU=0 Radius=93
    g1: Circle CenterX=-57 CenterY=-150 CenterZ=0 NormalX=0 NormalY=0 NormalZ=1 AngleXU=0 Radius=21
    g2: Circle CenterX=-41.75 CenterY=-126 CenterZ=0 NormalX=0 NormalY=0 NormalZ=1 AngleXU=0 Radius=2
    g3: Circle CenterX=-30.75 CenterY=-129.1 CenterZ=0 NormalX=0 NormalY=0 NormalZ=1 AngleXU=0 Radius=1.625
    g4: Circle CenterX=-30.75 CenterY=-203.5 CenterZ=0 NormalX=0 NormalY=0 NormalZ=1 AngleXU=0 Radius=1.625
    g5: Circle CenterX=57 CenterY=-150 CenterZ=0 NormalX=0 NormalY=0 NormalZ=1 AngleXU=0 Radius=21
  constraints (18):
    c: PointOnObject(g0,g-2)
    c: Radius(g0) = 93
    c: DistanceY(g0) = -150
    c: Radius(g1) = 21
    c: DistanceX(g0,g1) = -57
    c: DistanceY(g1,g0) = 0
    c: DistanceY(g1,g5) = 0
    c: DistanceX(g0,g5) = 57
    c: Radius(g5) = 21
    c: DistanceY(g4,g0) = 53.5
    c: Equal(g3,g4)
    c: Radius(g3) = 1.625
    c: DistanceX(g2,g4) = 11
    c: DistanceY(g4,g2) = 77.5
    c: Radius(g2) = 2
    c: DistanceX(g4,g0) = 30.75
    c: DistanceX(g4,g3) = 0
    c: DistanceY(g4,g3) = 74.4
FEATURE [Sketcher::SketchObject] Sketch034
  FullyConstrained = true
  Placement = pos=(0,0,0) rot=(1,0,0;1.5708rad)
  sketch-geometry (12):
    g0: LineSegment StartX=-51 StartY=-85 StartZ=0 EndX=-31 EndY=-85 EndZ=0
    g1: LineSegment StartX=-31 StartY=-85 StartZ=0 EndX=-31 EndY=-180 EndZ=0
    g2: LineSegment StartX=-31 StartY=-180 StartZ=0 EndX=-51 EndY=-180 EndZ=0
    g3: LineSegment StartX=-51 StartY=-180 StartZ=0 EndX=-51 EndY=-85 EndZ=0
    g4: LineSegment StartX=31 StartY=-180 StartZ=0 EndX=51 EndY=-180 EndZ=0
    g5: LineSegment StartX=51 StartY=-180 StartZ=0 EndX=51 EndY=-85 EndZ=0
    g6: LineSegment StartX=51 StartY=-85 StartZ=0 EndX=31 EndY=-85 EndZ=0
    g7: LineSegment StartX=31 StartY=-85 StartZ=0 EndX=31 EndY=-180 EndZ=0
    g8: Circle CenterX=-41 CenterY=-92.75 CenterZ=0 NormalX=0 NormalY=0 NormalZ=1 AngleXU=0 Radius=2.8
    g9: Circle CenterX=41 CenterY=-92.75 CenterZ=0 NormalX=0 NormalY=0 NormalZ=1 AngleXU=0 Radius=2.8
    g10: Circle CenterX=41 CenterY=-174.75 CenterZ=0 NormalX=0 NormalY=0 NormalZ=1 AngleXU=0 Radius=2.8
    g11: Circle CenterX=-41 CenterY=-174.75 CenterZ=0 NormalX=0 NormalY=0 NormalZ=1 AngleXU=0 Radius=2.8
  constraints (36):
    c: Coincident(g0,g1)
    c: Coincident(g1,g2)
    c: Coincident(g2,g3)
    c: Coincident(g3,g0)
    c: Horizontal(g0)
    c: Horizontal(g2)
    c: Vertical(g1)
    c: Vertical(g3)
    c: DistanceX(g2,g1) = 20
    c: DistanceY(g2) = -180
    c: DistanceX(g1) = -31
    c: DistanceY(g2,g0) = 95
    c: Coincident(g4,g5)
    c: Coincident(g5,g6)
    c: Coincident(g6,g7)
    c: Coincident(g7,g4)
    c: Horizontal(g4)
    c: Horizontal(g6)
    c: Vertical(g5)
    c: Vertical(g7)
    c: DistanceY(g4,g1) = 0
    c: DistanceX(g4) = 31
    c: DistanceX(g4,g4) = 20
    c: DistanceY(g6,g0) = 0
    c: Equal(g9,g8)
    c: Equal(g9,g11)
    c: Equal(g9,g10)
    c: Radius(g9) = 2.8
    c: DistanceY(g11) = -174.75
    c: DistanceY(g10,g11) = 0
    c: DistanceX(g11) = -41
    c: DistanceX(g10) = 41
    c: DistanceX(g8,g11) = 0
    c: DistanceX(g9,g10) = 0
    c: DistanceY(g11,g8) = 82
    c: DistanceY(g9,g8) = 0
FEATURE [Part::Extrusion] Extrude015  label="level4"
  Base = -> Sketch033
  Dir = (0,0,1)
  DirMode = 2
  FaceMakerClass = Part::FaceMakerBullseye
  LengthFwd = 5
  LengthRev = 0
  Placement = pos=(0,0,-185) rot=(0,0,1;0rad)
  Solid = true
  Symmetric = false
FEATURE [Part::Extrusion] Extrude016  label="fanHolder"
  Base = -> Sketch034
  Dir = (0,-1,-3e-16)
  DirMode = 2
  FaceMakerClass = Part::FaceMakerBullseye
  LengthFwd = 10
  LengthRev = 0
  Placement = pos=(0,-98,0) rot=(0,0,1;0rad)
  Solid = true
  Symmetric = false
FEATURE [Sketcher::SketchObject] Sketch035
  FullyConstrained = true
  Placement = pos=(0,0,0) rot=(0.57735,0.57735,0.57735;2.0944rad)
  sketch-geometry (15):
    g0: LineSegment StartX=-222 StartY=-80 StartZ=0 EndX=-210 EndY=-80 EndZ=0
    g1: LineSegment StartX=-108 StartY=-180 StartZ=0 EndX=-222 EndY=-180 EndZ=0
    g2: LineSegment StartX=-222 StartY=-180 StartZ=0 EndX=-222 EndY=-80 EndZ=0
    g3: LineSegment StartX=-120 StartY=-80 StartZ=0 EndX=-108 EndY=-80 EndZ=0
    g4: LineSegment StartX=-108 StartY=-80 StartZ=0 EndX=-108 EndY=-180 EndZ=0
    g5: Circle CenterX=-216 CenterY=-94.75 CenterZ=0 NormalX=0 NormalY=0 NormalZ=1 AngleXU=0 Radius=2
    g6: Circle CenterX=-113.8 CenterY=-87.8 CenterZ=0 NormalX=0 NormalY=0 NormalZ=1 AngleXU=0 Radius=2
    g7: Circle CenterX=-113.8 CenterY=-176.2 CenterZ=0 NormalX=0 NormalY=0 NormalZ=1 AngleXU=0 Radius=2
    g8: Circle CenterX=-216 CenterY=-176.2 CenterZ=0 NormalX=0 NormalY=0 NormalZ=1 AngleXU=0 Radius=2
    g9: LineSegment StartX=-210 StartY=-80 StartZ=0 EndX=-210 EndY=-120 EndZ=0
    g10: LineSegment StartX=-210 StartY=-120 StartZ=0 EndX=-120 EndY=-120 EndZ=0
    g11: LineSegment StartX=-120 StartY=-120 StartZ=0 EndX=-120 EndY=-80 EndZ=0
    g12: Circle CenterX=-155.2 CenterY=-125.25 CenterZ=0 NormalX=0 NormalY=0 NormalZ=1 AngleXU=0 Radius=1.625
    g13: Circle CenterX=-140 CenterY=-134.25 CenterZ=0 NormalX=0 NormalY=0 NormalZ=1 AngleXU=0 Radius=1.625
    g14: Circle CenterX=-195 CenterY=-134.25 CenterZ=0 NormalX=0 NormalY=0 NormalZ=1 AngleXU=0 Radius=1.625
  constraints (45):
    c: Coincident(g1,g2)
    c: Coincident(g2,g0)
    c: Horizontal(g0)
    c: Horizontal(g1)
    c: Vertical(g2)
    c: Coincident(g3,g4)
    c: Horizontal(g3)
    c: Vertical(g4)
    c: DistanceY(g1) = -180
    c: DistanceY(g1,g0) = 100
    c: Coincident(g9,g0)
    c: Vertical(g9)
    c: Coincident(g10,g9)
    c: Horizontal(g10)
    c: Coincident(g11,g10)
    c: Coincident(g11,g3)
    c: DistanceX(g1) = -222
    c: DistanceX(g1,g4) = 114
    c: DistanceY(g1,g8) = 3.8
    c: DistanceY(g7,g8) = 0
    c: Vertical(g11)
    c: DistanceX(g0,g0) = 12
    c: DistanceX(g3,g3) = 12
    c: DistanceY(g0,g3) = 0
    c: DistanceY(g4,g10) = 60
    c: DistanceY(g1,g14) = 45.75
    c: DistanceY(g13,g14) = 0
    c: DistanceX(g14,g13) = 55
    c: DistanceY(g13,g12) = 9
    c: DistanceX(g12,g13) = 15.2
    c: Equal(g13,g12)
    c: Equal(g13,g14)
    c: Radius(g13) = 1.625
    c: DistanceX(g13) = -140
    c: Equal(g6,g7)
    c: Equal(g6,g8)
    c: Equal(g6,g5)
    c: Radius(g6) = 2
    c: DistanceX(g1,g8) = 6
    c: DistanceX(g8,g7) = 102.2
    c: DistanceX(g6,g7) = 0
    c: DistanceX(g5,g8) = 0
    c: DistanceY(g8,g5) = 81.45
    c: DistanceY(g7,g6) = 88.4
    c: Coincident(g1,g4)
FEATURE [Part::Extrusion] Extrude017  label="powerSBCHolder"
  Base = -> Sketch035
  Dir = (1,0,0)
  DirMode = 2
  FaceMakerClass = Part::FaceMakerBullseye
  LengthFwd = 10
  LengthRev = 0
  Placement = pos=(-15,0,0) rot=(0,0,1;0rad)
  Solid = true
  Symmetric = false
FEATURE [Part::MultiFuse] Fusion077  label="level004"
  Shapes = -> [Extrude015,Extrude016,Extrude017]
FEATURE [Part::Feature] Part__Feature028  label="DCP-RJ6ST-F"
  Placement = pos=(57,-150,-250) rot=(0,1,0;3.14159rad)
  shape: bbox 40.26 x 40.33 x 38.85 mm, 485 faces, 2 solids (baked)
FEATURE [Part::Feature] Part__Feature027  label="DCC-RJ6ST-310"
  Placement = pos=(57,-150,-259) rot=(0,0,1;0rad)
  shape: bbox 40.36 x 68.07 x 51.72 mm, 441 faces (baked)
FEATURE [Part::Feature] Part__Feature022  label="3136N138_T-Slotted Framing"
  Placement = pos=(0,200.3,0) rot=(0,0,1;0rad)
  shape: bbox 101.6 x 133.4 x 139.7 mm, 136 faces (baked)
FEATURE [Part::Feature] Part__Feature023  label="47065T801_T-Slotted Framing"
  Placement = pos=(0,300.5,0) rot=(-1,0,0;1.5708rad)
  shape: bbox 25.4 x 152.4 x 25.4 mm, 108 faces (baked)
FEATURE [Part::Feature] Part__Feature024  label="47065T801_T-Slotted Framing001"
  Placement = pos=(0,450,0) rot=(-1,0,0;1.5708rad)
  shape: bbox 25.4 x 152.4 x 25.4 mm, 108 faces (baked)
FEATURE [Part::MultiFuse] Fusion079  label="framingSupport"
  Placement = pos=(0,350,-263) rot=(0,0,1;3.14159rad)
  Shapes = -> [Part__Feature024,Part__Feature022,Part__Feature023]
FEATURE [Sketcher::SketchObject] Sketch037  label="top013"
  FullyConstrained = true
  sketch-geometry (9):
    g0: Circle CenterX=0 CenterY=-150 CenterZ=0 NormalX=0 NormalY=0 NormalZ=1 AngleXU=0 Radius=93
    g1: Circle CenterX=-57 CenterY=-150 CenterZ=0 NormalX=0 NormalY=0 NormalZ=1 AngleXU=0 Radius=11
    g2: Circle CenterX=57 CenterY=-150 CenterZ=0 NormalX=0 NormalY=0 NormalZ=1 AngleXU=0 Radius=15.1
    g3: Circle CenterX=35 CenterY=-200 CenterZ=0 NormalX=0 NormalY=0 NormalZ=1 AngleXU=0 Radius=15.1
    g4: Circle CenterX=-35 CenterY=-200 CenterZ=0 NormalX=0 NormalY=0 NormalZ=1 AngleXU=0 Radius=6.4
    g5: ArcOfCircle CenterX=0 CenterY=-220 CenterZ=0 NormalX=0 NormalY=0 NormalZ=1 AngleXU=0 Radius=5 StartAngle=2.26529 EndAngle=7.15948
    g6: ArcOfCircle CenterX=0 CenterY=-212.5 CenterZ=0 NormalX=0 NormalY=0 NormalZ=1 AngleXU=0 Radius=3.2 StartAngle=3e-15 EndAngle=3.14159
    g7: LineSegment StartX=-3.2 StartY=-212.5 StartZ=0 EndX=-3.2 EndY=-216.158 EndZ=0
    g8: LineSegment StartX=3.2 StartY=-216.158 StartZ=0 EndX=3.2 EndY=-212.5 EndZ=0
  constraints (29):
    c: PointOnObject(g0,g-2)
    c: Radius(g0) = 93
    c: DistanceY(g0) = -150
    c: Radius(g1) = 11
    c: DistanceX(g0,g1) = -57
    c: DistanceY(g1,g0) = 0
    c: DistanceY(g1,g2) = 0
    c: DistanceX(g0,g2) = 57
    c: DistanceX(g3) = 35
    c: DistanceY(g3,g0) = 50
    c: DistanceY(g3,g4) = 0
    c: DistanceX(g4,g0) = 35
    c: Radius(g4) = 6.4
    c: Equal(g2,g3)
    c: Radius(g2) = 15.1
    c: PointOnObject(g5,g-2)
    c: PointOnObject(g6,g-2)
    c: DistanceY(g5,g0) = 70
    c: DistanceX(g5,g6) = 0
    c: DistanceX(g6,g5) = 0
    c: Coincident(g7,g6)
    c: Coincident(g7,g5)
    c: Coincident(g8,g5)
    c: Coincident(g8,g6)
    c: DistanceX(g5,g5) = 6.4
    c: DistanceY(g5,g6) = 7.5
    c: DistanceY(g6,g6) = 0
    c: DistanceY(g6,g6) = 0
    c: Radius(g5) = 5
FEATURE [Part::Extrusion] Extrude019  label="level005"
  Base = -> Sketch037
  Dir = (0,0,1)
  DirMode = 2
  FaceMakerClass = Part::FaceMakerBullseye
  LengthFwd = 8
  LengthRev = 0
  Placement = pos=(0,0,-250) rot=(0,0,1;0rad)
  Solid = true
  Symmetric = false
FEATURE [Part::Feature] Feature001  label="PG7"
  Placement = pos=(-35,-200,-248) rot=(0,0,1;0rad)
  shape: bbox 21.32 x 20.97 x 29.79 mm, 246 faces, 3 solids (baked)
FEATURE [Part::Feature] Shell029
  shape: bbox 36.98 x 21.68 x 36.68 mm, 152 faces, 0 solids (baked)
FEATURE [Part::Feature] Shell030
  shape: bbox 22.66 x 11.43 x 22.66 mm, 6 faces, 0 solids (baked)
FEATURE [Part::Feature] Shell031
  shape: bbox 0.3612 x 0.889 x 0.6255 mm, 1 faces, 0 solids (baked)
FEATURE [Part::Feature] Shell032
  shape: bbox 35.58 x 29.16 x 35.58 mm, 49 faces, 0 solids (baked)
FEATURE [Part::Feature] Shell033
  shape: bbox 24.46 x 14.2 x 24.46 mm, 102 faces, 0 solids (baked)
FEATURE [Part::Feature] Shell034
  shape: bbox 0.3892 x 1.194 x 0.6742 mm, 1 faces, 0 solids (baked)
FEATURE [Part::Feature] Shell035
  shape: bbox 0.2703 x 0.381 x 0.4682 mm, 1 faces, 0 solids (baked)
FEATURE [Part::Feature] Shell036
  shape: bbox 0.2577 x 0.3048 x 0.4459 mm, 1 faces, 0 solids (baked)
FEATURE [Part::Feature] Shell037
  shape: bbox 36.98 x 18.12 x 36.6 mm, 205 faces, 0 solids (baked)
FEATURE [Part::Compound2] Compound003  label="M3222GBH_SW0002"
  Links = -> [Shell037,Shell029,Shell030,Shell033,Shell032,Shell036,Shell034,Shell031,Shell035]
  Placement = pos=(35,-200,-250) rot=(1,0,0;4.71239rad)
FEATURE [Part::Feature] Part__Feature200  label="powerInsert"
  Placement = pos=(-57,-150,-267) rot=(1,0,0;1.5708rad)
  shape: bbox 29.63 x 29.64 x 35.77 mm, 59 faces (baked)
FEATURE [Sketcher::SketchObject] Sketch038
  FullyConstrained = true
  sketch-geometry (4):
    g0: ArcOfCircle CenterX=0 CenterY=-220 CenterZ=0 NormalX=0 NormalY=0 NormalZ=1 AngleXU=0 Radius=5 StartAngle=3.14159 EndAngle=6.28319
    g1: ArcOfCircle CenterX=-1.2e-15 CenterY=-212.5 CenterZ=0 NormalX=0 NormalY=0 NormalZ=1 AngleXU=0 Radius=5 StartAngle=1.419e-13 EndAngle=3.14159
    g2: LineSegment StartX=5 StartY=-220 StartZ=0 EndX=5 EndY=-212.5 EndZ=0
    g3: LineSegment StartX=-5 StartY=-212.5 StartZ=0 EndX=-5 EndY=-220 EndZ=0
  constraints (10):
    c: Tangent(g0,g2) = -1.5708
    c: Tangent(g2,g1) = -1.5708
    c: Tangent(g1,g3) = -1.5708
    c: Tangent(g3,g0) = -1.5708
    c: Equal(g0,g1)
    c: Vertical(g2)
    c: DistanceX(g0) = 0
    c: DistanceY(g0) = -220
    c: Radius(g0) = 5
    c: DistanceY(g0,g1) = 7.5
FEATURE [Part::Extrusion] Extrude020  label="micCutLevel5"
  Base = -> Sketch038
  Dir = (0,0,1)
  DirMode = 2
  FaceMakerClass = Part::FaceMakerBullseye
  LengthFwd = 10
  LengthRev = 0
  Placement = pos=(0,0,-246.5) rot=(0,0,1;0rad)
  Solid = true
  Symmetric = false
FEATURE [Sketcher::SketchObject] Sketch039
  FullyConstrained = true
  sketch-geometry (16):
    g0: ArcOfCircle CenterX=0 CenterY=-150 CenterZ=0 NormalX=0 NormalY=0 NormalZ=1 AngleXU=0 Radius=93 StartAngle=2.86943 EndAngle=3.41376
    g1: ArcOfCircle CenterX=0 CenterY=-150 CenterZ=0 NormalX=0 NormalY=0 NormalZ=1 AngleXU=0 Radius=93 StartAngle=1.29863 EndAngle=1.84296
    g2: ArcOfCircle CenterX=0 CenterY=-150 CenterZ=0 NormalX=0 NormalY=0 NormalZ=1 AngleXU=0 Radius=93 StartAngle=6.01102 EndAngle=6.55535
    g3: ArcOfCircle CenterX=0 CenterY=-150 CenterZ=0 NormalX=0 NormalY=0 NormalZ=1 AngleXU=0 Radius=93 StartAngle=4.44022 EndAngle=4.98455
    g4: ArcOfCircle CenterX=0 CenterY=-150 CenterZ=0 NormalX=0 NormalY=0 NormalZ=1 AngleXU=0 Radius=86 StartAngle=1.27584 EndAngle=1.86575
    g5: ArcOfCircle CenterX=0 CenterY=-150 CenterZ=0 NormalX=0 NormalY=0 NormalZ=1 AngleXU=0 Radius=86 StartAngle=5.98823 EndAngle=6.57814
    g6: ArcOfCircle CenterX=0 CenterY=-150 CenterZ=0 NormalX=0 NormalY=0 NormalZ=1 AngleXU=0 Radius=86 StartAngle=2.84664 EndAngle=3.43655
    g7: ArcOfCircle CenterX=0 CenterY=-150 CenterZ=0 NormalX=0 NormalY=0 NormalZ=1 AngleXU=0 Radius=86 StartAngle=4.41743 EndAngle=5.00734
    g8: LineSegment StartX=25 StartY=-60.4232 StartZ=0 EndX=25 EndY=-67.7139 EndZ=0
    g9: LineSegment StartX=-25 StartY=-60.4232 StartZ=0 EndX=-25 EndY=-67.7139 EndZ=0
    g10: LineSegment StartX=-89.5768 StartY=-125 StartZ=0 EndX=-82.2861 EndY=-125 EndZ=0
    g11: LineSegment StartX=-89.5768 StartY=-175 StartZ=0 EndX=-82.2861 EndY=-175 EndZ=0
    g12: LineSegment StartX=-25 StartY=-239.577 StartZ=0 EndX=-25 EndY=-232.286 EndZ=0
    g13: LineSegment StartX=25 StartY=-239.577 StartZ=0 EndX=25 EndY=-232.286 EndZ=0
    g14: LineSegment StartX=89.5768 StartY=-175 StartZ=0 EndX=82.2861 EndY=-175 EndZ=0
    g15: LineSegment StartX=89.5768 StartY=-125 StartZ=0 EndX=82.2861 EndY=-125 EndZ=0
  constraints (49):
    c: PointOnObject(g0,g-2)
    c: Coincident(g1,g0)
    c: Coincident(g2,g0)
    c: Coincident(g3,g0)
    c: DistanceY(g0) = -150
    c: Coincident(g4,g0)
    c: Coincident(g5,g0)
    c: Coincident(g6,g0)
    c: Coincident(g7,g0)
    c: DistanceX(g4,g0) = 25
    c: DistanceX(g1,g4) = 0
    c: DistanceX(g0,g4) = 25
    c: DistanceX(g4,g1) = 0
    c: DistanceY(g0,g5) = 25
    c: DistanceY(g5,g2) = 0
    c: DistanceY(g2,g0) = 25
    c: DistanceY(g2,g5) = 0
    c: DistanceY(g6,g0) = 25
    c: DistanceY(g0,g6) = 0
    c: DistanceY(g0,g6) = 25
    c: DistanceY(g6,g0) = 0
    c: Equal(g1,g2)
    c: Equal(g1,g3)
    c: Equal(g1,g0)
    c: Radius(g1) = 93
    c: Equal(g6,g4)
    c: Equal(g6,g5)
    c: Equal(g6,g7)
    c: Radius(g6) = 86
    c: DistanceX(g0,g7) = 25
    c: DistanceX(g7,g3) = 0
    c: DistanceX(g3) = -25
    c: DistanceX(g3,g7) = 0
    c: Coincident(g8,g1)
    c: Coincident(g8,g4)
    c: Coincident(g9,g1)
    c: Coincident(g9,g4)
    c: Coincident(g10,g0)
    c: Coincident(g10,g6)
    c: Coincident(g11,g0)
    c: Coincident(g11,g6)
    c: Coincident(g12,g3)
    c: Coincident(g12,g7)
    c: Coincident(g13,g3)
    c: Coincident(g13,g7)
    c: Coincident(g14,g2)
    c: Coincident(g14,g5)
    c: Coincident(g15,g2)
    c: Coincident(g15,g5)
FEATURE [Part::Extrusion] Extrude021  label="srsHolds002"
  Base = -> Sketch039
  Dir = (0,0,1)
  DirMode = 2
  FaceMakerClass = Part::FaceMakerBullseye
  LengthFwd = 30
  LengthRev = 0
  Placement = pos=(0,0,-185) rot=(0,0,1;0rad)
  Solid = true
  Symmetric = false
FEATURE [Part::FeaturePython] Tube003  # WARN: FeaturePython — macro-defined, semantics opaque (R4)
  AttacherType = Attacher::AttachEngine3D
  Height = 125
  InnerRadius = 94
  OuterRadius = 98
  Placement = pos=(0,-150,-185) rot=(0,0,1;0rad)
FEATURE [Sketcher::SketchObject] Sketch040  label="top014"
  FullyConstrained = true
  sketch-geometry (2):
    g0: Circle CenterX=0 CenterY=-150 CenterZ=0 NormalX=0 NormalY=0 NormalZ=1 AngleXU=0 Radius=98
    g1: Circle CenterX=0 CenterY=-150 CenterZ=0 NormalX=0 NormalY=0 NormalZ=1 AngleXU=0 Radius=78
  constraints (5):
    c: PointOnObject(g0,g-2)
    c: Diameter(g0) = 196
    c: DistanceY(g0) = -150
    c: Coincident(g1,g0)
    c: Radius(g1) = 78
FEATURE [Part::Extrusion] Extrude022  label="TupeConnectLevel3"
  Base = -> Sketch040
  Dir = (0,0,1)
  DirMode = 2
  FaceMakerClass = Part::FaceMakerBullseye
  LengthFwd = 5
  LengthRev = 0
  Placement = pos=(0,0,-65) rot=(0,0,1;0rad)
  Solid = true
  Symmetric = false
FEATURE [Part::MultiFuse] Fusion080  label="tube4to3"
  Shapes = -> [Extrude022,Tube003]
FEATURE [Part::MultiFuse] Fusion081  label="level04"
  Shapes = -> [Fusion077,Extrude021]
FEATURE [Sketcher::SketchObject] Sketch041
  FullyConstrained = true
  sketch-geometry (16):
    g0: ArcOfCircle CenterX=0 CenterY=-150 CenterZ=0 NormalX=0 NormalY=0 NormalZ=1 AngleXU=0 Radius=93 StartAngle=2.86943 EndAngle=3.41376
    g1: ArcOfCircle CenterX=0 CenterY=-150 CenterZ=0 NormalX=0 NormalY=0 NormalZ=1 AngleXU=0 Radius=93 StartAngle=1.29863 EndAngle=1.84296
    g2: ArcOfCircle CenterX=0 CenterY=-150 CenterZ=0 NormalX=0 NormalY=0 NormalZ=1 AngleXU=0 Radius=93 StartAngle=6.01102 EndAngle=6.55535
    g3: ArcOfCircle CenterX=0 CenterY=-150 CenterZ=0 NormalX=0 NormalY=0 NormalZ=1 AngleXU=0 Radius=93 StartAngle=4.44022 EndAngle=4.98455
    g4: ArcOfCircle CenterX=0 CenterY=-150 CenterZ=0 NormalX=0 NormalY=0 NormalZ=1 AngleXU=0 Radius=86 StartAngle=1.27584 EndAngle=1.86575
    g5: ArcOfCircle CenterX=0 CenterY=-150 CenterZ=0 NormalX=0 NormalY=0 NormalZ=1 AngleXU=0 Radius=86 StartAngle=5.98823 EndAngle=6.57814
    g6: ArcOfCircle CenterX=0 CenterY=-150 CenterZ=0 NormalX=0 NormalY=0 NormalZ=1 AngleXU=0 Radius=86 StartAngle=2.84664 EndAngle=3.43655
    g7: ArcOfCircle CenterX=0 CenterY=-150 CenterZ=0 NormalX=0 NormalY=0 NormalZ=1 AngleXU=0 Radius=86 StartAngle=4.41743 EndAngle=5.00734
    g8: LineSegment StartX=25 StartY=-60.4232 StartZ=0 EndX=25 EndY=-67.7139 EndZ=0
    g9: LineSegment StartX=-25 StartY=-60.4232 StartZ=0 EndX=-25 EndY=-67.7139 EndZ=0
    g10: LineSegment StartX=-89.5768 StartY=-125 StartZ=0 EndX=-82.2861 EndY=-125 EndZ=0
    g11: LineSegment StartX=-89.5768 StartY=-175 StartZ=0 EndX=-82.2861 EndY=-175 EndZ=0
    g12: LineSegment StartX=-25 StartY=-239.577 StartZ=0 EndX=-25 EndY=-232.286 EndZ=0
    g13: LineSegment StartX=25 StartY=-239.577 StartZ=0 EndX=25 EndY=-232.286 EndZ=0
    g14: LineSegment StartX=89.5768 StartY=-175 StartZ=0 EndX=82.2861 EndY=-175 EndZ=0
    g15: LineSegment StartX=89.5768 StartY=-125 StartZ=0 EndX=82.2861 EndY=-125 EndZ=0
  constraints (49):
    c: PointOnObject(g0,g-2)
    c: Coincident(g1,g0)
    c: Coincident(g2,g0)
    c: Coincident(g3,g0)
    c: DistanceY(g0) = -150
    c: Coincident(g4,g0)
    c: Coincident(g5,g0)
    c: Coincident(g6,g0)
    c: Coincident(g7,g0)
    c: DistanceX(g4,g0) = 25
    c: DistanceX(g1,g4) = 0
    c: DistanceX(g0,g4) = 25
    c: DistanceX(g4,g1) = 0
    c: DistanceY(g0,g5) = 25
    c: DistanceY(g5,g2) = 0
    c: DistanceY(g2,g0) = 25
    c: DistanceY(g2,g5) = 0
    c: DistanceY(g6,g0) = 25
    c: DistanceY(g0,g6) = 0
    c: DistanceY(g0,g6) = 25
    c: DistanceY(g6,g0) = 0
    c: Equal(g1,g2)
    c: Equal(g1,g3)
    c: Equal(g1,g0)
    c: Radius(g1) = 93
    c: Equal(g6,g4)
    c: Equal(g6,g5)
    c: Equal(g6,g7)
    c: Radius(g6) = 86
    c: DistanceX(g0,g7) = 25
    c: DistanceX(g7,g3) = 0
    c: DistanceX(g3) = -25
    c: DistanceX(g3,g7) = 0
    c: Coincident(g8,g1)
    c: Coincident(g8,g4)
    c: Coincident(g9,g1)
    c: Coincident(g9,g4)
    c: Coincident(g10,g0)
    c: Coincident(g10,g6)
    c: Coincident(g11,g0)
    c: Coincident(g11,g6)
    c: Coincident(g12,g3)
    c: Coincident(g12,g7)
    c: Coincident(g13,g3)
    c: Coincident(g13,g7)
    c: Coincident(g14,g2)
    c: Coincident(g14,g5)
    c: Coincident(g15,g2)
    c: Coincident(g15,g5)
FEATURE [Part::Extrusion] Extrude023  label="srsHoldsLevel5"
  Base = -> Sketch041
  Dir = (0,0,1)
  DirMode = 2
  FaceMakerClass = Part::FaceMakerBullseye
  LengthFwd = 30
  LengthRev = 0
  Placement = pos=(0,0,-250) rot=(0,0,1;0rad)
  Solid = true
  Symmetric = false
FEATURE [Sketcher::SketchObject] Sketch042  label="top015"
  FullyConstrained = true
  sketch-geometry (2):
    g0: Circle CenterX=0 CenterY=-150 CenterZ=0 NormalX=0 NormalY=0 NormalZ=1 AngleXU=0 Radius=98
    g1: Circle CenterX=0 CenterY=-150 CenterZ=0 NormalX=0 NormalY=0 NormalZ=1 AngleXU=0 Radius=76
  constraints (5):
    c: PointOnObject(g0,g-2)
    c: Diameter(g0) = 196
    c: DistanceY(g0) = -150
    c: Coincident(g1,g0)
    c: Radius(g1) = 76
FEATURE [Part::Extrusion] Extrude024  label="TupeConnectLevel004"
  Base = -> Sketch042
  Dir = (0,0,1)
  DirMode = 2
  FaceMakerClass = Part::FaceMakerBullseye
  LengthFwd = 5
  LengthRev = 0
  Placement = pos=(0,0,-65) rot=(0,0,1;0rad)
  Solid = true
  Symmetric = false
FEATURE [Part::FeaturePython] Tube004  # WARN: FeaturePython — macro-defined, semantics opaque (R4)
  AttacherType = Attacher::AttachEngine3D
  Height = 65
  InnerRadius = 94
  OuterRadius = 98
  Placement = pos=(0,-150,-125) rot=(0,0,1;0rad)
FEATURE [Part::MultiFuse] Fusion082  label="tube5to004"
  Placement = pos=(0,0,-125) rot=(0,0,1;0rad)
  Shapes = -> [Extrude024,Tube004]
FEATURE [Part::MultiFuse] Fusion083  label="level5"
  Shapes = -> [Extrude019,Extrude023]
FEATURE [Part::Cylinder] Cylinder131
  Angle = 360
  AttacherType = Attacher::AttachEngine3D
  FirstAngle = 0
  Height = 300
  Placement = pos=(0,0,90) rot=(1,0,0;1.5708rad)
  Radius = 2.13
  SecondAngle = 0
FEATURE [Part::Cylinder] Cylinder132
  Angle = 360
  AttacherType = Attacher::AttachEngine3D
  FirstAngle = 0
  Height = 300
  Placement = pos=(-150,-150,90) rot=(0.57735,0.57735,0.57735;2.0944rad)
  Radius = 2.13
  SecondAngle = 0
FEATURE [Part::MultiFuse] Fusion084  label="m4Cuts009"
  Placement = pos=(0,0,-321) rot=(0,0,1;0rad)
  Shapes = -> [Cylinder132,Cylinder131]
FEATURE [Part::Cylinder] Cylinder133
  Angle = 360
  AttacherType = Attacher::AttachEngine3D
  FirstAngle = 0
  Height = 300
  Placement = pos=(0,0,90) rot=(1,0,0;1.5708rad)
  Radius = 2.8
  SecondAngle = 0
FEATURE [Part::Cylinder] Cylinder134
  Angle = 360
  AttacherType = Attacher::AttachEngine3D
  FirstAngle = 0
  Height = 300
  Placement = pos=(-150,-150,90) rot=(0.57735,0.57735,0.57735;2.0944rad)
  Radius = 2.8
  SecondAngle = 0
FEATURE [Part::MultiFuse] Fusion085  label="m4HeatSetCuts001"
  Placement = pos=(0,0,-321) rot=(0,0,1;0rad)
  Shapes = -> [Cylinder134,Cylinder133]
FEATURE [Sketcher::SketchObject] Sketch043
  FullyConstrained = true
  sketch-geometry (4):
    g0: Circle CenterX=0 CenterY=-68 CenterZ=0 NormalX=0 NormalY=0 NormalZ=1 AngleXU=0 Radius=2.125
    g1: Circle CenterX=82 CenterY=-150 CenterZ=0 NormalX=0 NormalY=0 NormalZ=1 AngleXU=0 Radius=2.125
    g2: Circle CenterX=0 CenterY=-232 CenterZ=0 NormalX=0 NormalY=0 NormalZ=1 AngleXU=0 Radius=2.125
    g3: Circle CenterX=-82 CenterY=-150 CenterZ=0 NormalX=0 NormalY=0 NormalZ=1 AngleXU=0 Radius=2.125
  constraints (12):
    c: PointOnObject(g0,g-2)
    c: DistanceY(g1) = -150
    c: DistanceY(g1,g3) = 0
    c: DistanceX(g2) = 0
    c: DistanceX(g1) = 82
    c: Equal(g1,g0)
    c: Equal(g1,g3)
    c: Equal(g1,g2)
    c: Diameter(g1) = 4.25
    c: DistanceX(g3) = -82
    c: DistanceY(g3,g0) = 82
    c: DistanceY(g2,g3) = 82
FEATURE [Part::Extrusion] Extrude025  label="m4VerCuts"
  Base = -> Sketch043
  Dir = (0,0,1)
  DirMode = 2
  FaceMakerClass = Part::FaceMakerBullseye
  LengthFwd = 20
  LengthRev = 0
  Placement = pos=(0,0,-194.5) rot=(0,0,1;0rad)
  Solid = true
  Symmetric = false
FEATURE [Sketcher::SketchObject] Sketch044
  FullyConstrained = true
  sketch-geometry (4):
    g0: Circle CenterX=0 CenterY=-68 CenterZ=0 NormalX=0 NormalY=0 NormalZ=1 AngleXU=0 Radius=2.8
    g1: Circle CenterX=82 CenterY=-150 CenterZ=0 NormalX=0 NormalY=0 NormalZ=1 AngleXU=0 Radius=2.8
    g2: Circle CenterX=0 CenterY=-232 CenterZ=0 NormalX=0 NormalY=0 NormalZ=1 AngleXU=0 Radius=2.8
    g3: Circle CenterX=-82 CenterY=-150 CenterZ=0 NormalX=0 NormalY=0 NormalZ=1 AngleXU=0 Radius=2.8
  constraints (12):
    c: PointOnObject(g0,g-2)
    c: DistanceY(g1) = -150
    c: DistanceY(g1,g3) = 0
    c: DistanceX(g2) = 0
    c: DistanceX(g1) = 82
    c: Equal(g1,g0)
    c: Equal(g1,g3)
    c: Equal(g1,g2)
    c: Diameter(g1) = 5.6
    c: DistanceX(g3) = -82
    c: DistanceY(g3,g0) = 82
    c: DistanceY(g2,g3) = 82
FEATURE [Part::Extrusion] Extrude026  label="m4HeatSetVerCuts001"
  Base = -> Sketch044
  Dir = (0,0,1)
  DirMode = 2
  FaceMakerClass = Part::FaceMakerBullseye
  LengthFwd = 20
  LengthRev = 0
  Placement = pos=(0,0,-193) rot=(0,0,1;0rad)
  Solid = true
  Symmetric = false
FEATURE [Part::Cut] Cut035  label="level05s"
  Base = -> Fusion083
  Tool = -> Fusion085
FEATURE [Part::Cut] Cut036  label="tube4to5"
  Base = -> Fusion082
  Tool = -> Fusion084
FEATURE [Part::Cut] Cut037  label="level4s"
  Base = -> Fusion081
  Tool = -> Extrude025
FEATURE [Part::Cut] Cut038  label="tube4to5s"
  Base = -> Cut036
  Tool = -> Extrude026
FEATURE [Part::Cylinder] Cylinder135
  Angle = 360
  AttacherType = Attacher::AttachEngine3D
  FirstAngle = 0
  Height = 300
  Placement = pos=(0,0,90) rot=(1,0,0;1.5708rad)
  Radius = 2.8
  SecondAngle = 0
FEATURE [Part::Cylinder] Cylinder136
  Angle = 360
  AttacherType = Attacher::AttachEngine3D
  FirstAngle = 0
  Height = 300
  Placement = pos=(-150,-150,90) rot=(0.57735,0.57735,0.57735;2.0944rad)
  Radius = 2.8
  SecondAngle = 0
FEATURE [Part::MultiFuse] Fusion086  label="m4HeatSetCuts002"
  Placement = pos=(0,0,-257) rot=(0,0,1;0rad)
  Shapes = -> [Cylinder136,Cylinder135]
FEATURE [Part::Cut] Cut039  label="level4s001"
  Base = -> Cut037
  Tool = -> Fusion086
FEATURE [Part::Cylinder] Cylinder137
  Angle = 360
  AttacherType = Attacher::AttachEngine3D
  FirstAngle = 0
  Height = 300
  Placement = pos=(0,0,90) rot=(1,0,0;1.5708rad)
  Radius = 2.13
  SecondAngle = 0
FEATURE [Part::Cylinder] Cylinder138
  Angle = 360
  AttacherType = Attacher::AttachEngine3D
  FirstAngle = 0
  Height = 300
  Placement = pos=(-150,-150,90) rot=(0.57735,0.57735,0.57735;2.0944rad)
  Radius = 2.13
  SecondAngle = 0
FEATURE [Part::MultiFuse] Fusion087  label="m4Cuts010"
  Placement = pos=(0,0,-257) rot=(0,0,1;0rad)
  Shapes = -> [Cylinder138,Cylinder137]
FEATURE [Part::Cut] Cut040  label="level3to4Tube"
  Base = -> Fusion080
  Tool = -> Fusion087
FEATURE [Part::Cut] Cut041  label="level5s"
  Base = -> Cut035
  Tool = -> Extrude020
FEATURE [Sketcher::SketchObject] Sketch046
  FullyConstrained = true
  sketch-geometry (4):
    g0: Circle CenterX=0 CenterY=-63 CenterZ=0 NormalX=0 NormalY=0 NormalZ=1 AngleXU=0 Radius=2.8
    g1: Circle CenterX=87 CenterY=-150 CenterZ=0 NormalX=0 NormalY=0 NormalZ=1 AngleXU=0 Radius=2.8
    g2: Circle CenterX=0 CenterY=-237 CenterZ=0 NormalX=0 NormalY=0 NormalZ=1 AngleXU=0 Radius=2.8
    g3: Circle CenterX=-87 CenterY=-150 CenterZ=0 NormalX=0 NormalY=0 NormalZ=1 AngleXU=0 Radius=2.8
  constraints (12):
    c: PointOnObject(g0,g-2)
    c: DistanceY(g1) = -150
    c: DistanceY(g1,g3) = 0
    c: DistanceX(g2) = 0
    c: DistanceX(g1) = 87
    c: Equal(g1,g0)
    c: Equal(g1,g3)
    c: Equal(g1,g2)
    c: Diameter(g1) = 5.6
    c: DistanceX(g3) = -87
    c: DistanceY(g3,g0) = 87
    c: DistanceY(g2,g3) = 87
FEATURE [Part::Extrusion] Extrude028  label="m4HeatSetVerCuts003"
  Base = -> Sketch046
  Dir = (0,0,1)
  DirMode = 2
  FaceMakerClass = Part::FaceMakerBullseye
  LengthFwd = 20
  LengthRev = 0
  Placement = pos=(0,0,-69.5) rot=(0,0,1;0rad)
  Solid = true
  Symmetric = false
FEATURE [Sketcher::SketchObject] Sketch047
  FullyConstrained = true
  sketch-geometry (4):
    g0: Circle CenterX=0 CenterY=-63 CenterZ=0 NormalX=0 NormalY=0 NormalZ=1 AngleXU=0 Radius=2.125
    g1: Circle CenterX=87 CenterY=-150 CenterZ=0 NormalX=0 NormalY=0 NormalZ=1 AngleXU=0 Radius=2.125
    g2: Circle CenterX=0 CenterY=-237 CenterZ=0 NormalX=0 NormalY=0 NormalZ=1 AngleXU=0 Radius=2.125
    g3: Circle CenterX=-87 CenterY=-150 CenterZ=0 NormalX=0 NormalY=0 NormalZ=1 AngleXU=0 Radius=2.125
  constraints (12):
    c: PointOnObject(g0,g-2)
    c: DistanceY(g1) = -150
    c: DistanceY(g1,g3) = 0
    c: DistanceX(g2) = 0
    c: DistanceX(g1) = 87
    c: Equal(g1,g0)
    c: Equal(g1,g3)
    c: Equal(g1,g2)
    c: Diameter(g1) = 4.25
    c: DistanceX(g3) = -87
    c: DistanceY(g3,g0) = 87
    c: DistanceY(g2,g3) = 87
FEATURE [Part::Extrusion] Extrude029  label="m4VerCuts001"
  Base = -> Sketch047
  Dir = (0,0,1)
  DirMode = 2
  FaceMakerClass = Part::FaceMakerBullseye
  LengthFwd = 20
  LengthRev = 0
  Placement = pos=(0,0,-65.5) rot=(0,0,1;0rad)
  Solid = true
  Symmetric = false
FEATURE [Part::Cut] Cut042  label="tube3to4s"
  Base = -> Cut040
  Tool = -> Extrude028
FEATURE [Part::Cut] Cut043  label="level03"
  Base = -> Fusion067
  Tool = -> Extrude029
FEATURE [Part::Cylinder] Cylinder139
  Angle = 360
  AttacherType = Attacher::AttachEngine3D
  FirstAngle = 0
  Height = 300
  Placement = pos=(0,0,90) rot=(1,0,0;1.5708rad)
  Radius = 2.13
  SecondAngle = 0
FEATURE [Part::Cylinder] Cylinder140
  Angle = 360
  AttacherType = Attacher::AttachEngine3D
  FirstAngle = 0
  Height = 300
  Placement = pos=(-150,-150,90) rot=(0.57735,0.57735,0.57735;2.0944rad)
  Radius = 2.13
  SecondAngle = 0
FEATURE [Part::MultiFuse] Fusion088  label="m4Cuts011"
  Placement = pos=(0,0,-130) rot=(0,0,1;0rad)
  Shapes = -> [Cylinder140,Cylinder139]
FEATURE [Part::Cut] Cut044  label="tube3to2s"
  Base = -> Tube002
  Tool = -> Fusion088
FEATURE [Part::Cylinder] Cylinder141
  Angle = 360
  AttacherType = Attacher::AttachEngine3D
  FirstAngle = 0
  Height = 300
  Placement = pos=(0,0,90) rot=(1,0,0;1.5708rad)
  Radius = 2.8
  SecondAngle = 0
FEATURE [Part::Cylinder] Cylinder142
  Angle = 360
  AttacherType = Attacher::AttachEngine3D
  FirstAngle = 0
  Height = 300
  Placement = pos=(-150,-150,90) rot=(0.57735,0.57735,0.57735;2.0944rad)
  Radius = 2.8
  SecondAngle = 0
FEATURE [Part::MultiFuse] Fusion089  label="m4HeatSetCuts003"
  Placement = pos=(0,0,-130) rot=(0,0,1;0rad)
  Shapes = -> [Cylinder142,Cylinder141]
FEATURE [Part::Cylinder] Cylinder143  label="heatSetHolds"
  Angle = 360
  AttacherType = Attacher::AttachEngine3D
  FirstAngle = 0
  Height = 10
  Placement = pos=(0,-78,-40) rot=(-1,0,0;1.5708rad)
  Radius = 8
  SecondAngle = 0
FEATURE [Part::Cylinder] Cylinder144  label="heatSetHolds001"
  Angle = 360
  AttacherType = Attacher::AttachEngine3D
  FirstAngle = 0
  Height = 10
  Placement = pos=(0,-221,-40) rot=(0,0.707107,-0.707107;3.14159rad)
  Radius = 8
  SecondAngle = 0
FEATURE [Part::Cylinder] Cylinder145  label="heatSetHolds002"
  Angle = 360
  AttacherType = Attacher::AttachEngine3D
  FirstAngle = 0
  Height = 10
  Placement = pos=(72,-150,-40) rot=(0.57735,-0.57735,0.57735;4.18879rad)
  Radius = 8
  SecondAngle = 0
FEATURE [Part::Cylinder] Cylinder146  label="heatSetHolds003"
  Angle = 360
  AttacherType = Attacher::AttachEngine3D
  FirstAngle = 0
  Height = 10
  Placement = pos=(-72,-150,-40) rot=(0.57735,0.57735,-0.57735;4.18879rad)
  Radius = 8
  SecondAngle = 0
FEATURE [Part::MultiFuse] Fusion090  label="m4HeatSetHolds"
  Shapes = -> [Cylinder143,Cylinder144,Cylinder145,Cylinder146]
FEATURE [Part::MultiFuse] Fusion091  label="level003s"
  Shapes = -> [Cut043,Fusion090]
FEATURE [Part::Cut] Cut045  label="level3s"
  Base = -> Fusion091
  Tool = -> Fusion089
FEATURE [Part::Cylinder] Cylinder147
  Angle = 360
  AttacherType = Attacher::AttachEngine3D
  FirstAngle = 0
  Height = 300
  Placement = pos=(0,0,90) rot=(1,0,0;1.5708rad)
  Radius = 2.13
  SecondAngle = 0
FEATURE [Part::Cylinder] Cylinder148
  Angle = 360
  AttacherType = Attacher::AttachEngine3D
  FirstAngle = 0
  Height = 300
  Placement = pos=(-150,-150,90) rot=(0.57735,0.57735,0.57735;2.0944rad)
  Radius = 2.13
  SecondAngle = 0
FEATURE [Part::Cylinder] Cylinder149
  Angle = 360
  AttacherType = Attacher::AttachEngine3D
  FirstAngle = 0
  Height = 300
  Placement = pos=(106.066,-43.934,90) rot=(0.862856,-0.357407,-0.357407;1.71777rad)
  Radius = 2.13
  SecondAngle = 0
FEATURE [Part::Cylinder] Cylinder150
  Angle = 360
  AttacherType = Attacher::AttachEngine3D
  FirstAngle = 0
  Height = 300
  Placement = pos=(-106.066,-43.934,90) rot=(0.862856,0.357407,0.357407;1.71777rad)
  Radius = 2.13
  SecondAngle = 0
FEATURE [Part::MultiFuse] Fusion092  label="m4Cuts012"
  Placement = pos=(0,0,-82) rot=(0,0,1;0rad)
  Shapes = -> [Cylinder148,Cylinder147]
FEATURE [Part::MultiFuse] Fusion093  label="m4Cuts013"
  Placement = pos=(0,0,-82) rot=(0,0,1;0rad)
  Shapes = -> [Cylinder149,Cylinder150]
FEATURE [Part::MultiFuse] Fusion094  label="m4Cuts014"
  Shapes = -> [Fusion092,Fusion093]
FEATURE [Part::Cut] Cut046  label="tubeLevel3to2s"
  Base = -> Cut044
  Tool = -> Fusion094
FEATURE [Part::Fillet] Fillet002  label="level4to5s"
  Base = -> Cut038
  Edges = 3 edges r=3: [Edge3,Edge7,Edge32]
FEATURE [Part::FeaturePython] Tube005  # WARN: FeaturePython — macro-defined, semantics opaque (R4)
  AttacherType = Attacher::AttachEngine3D
  Height = 3
  InnerRadius = 95
  OuterRadius = 98
  Placement = pos=(0,-150,-188) rot=(0,0,1;0rad)
FEATURE [Part::Cylinder] Cylinder151
  Angle = 360
  AttacherType = Attacher::AttachEngine3D
  FirstAngle = 0
  Height = 300
  Placement = pos=(0,0,90) rot=(1,0,0;1.5708rad)
  Radius = 2.13
  SecondAngle = 0
FEATURE [Part::Cylinder] Cylinder152
  Angle = 360
  AttacherType = Attacher::AttachEngine3D
  FirstAngle = 0
  Height = 300
  Placement = pos=(-150,-150,90) rot=(0.57735,0.57735,0.57735;2.0944rad)
  Radius = 2.13
  SecondAngle = 0
FEATURE [Part::MultiFuse] Fusion096  label="m4Cuts015"
  Placement = pos=(0,0,-321) rot=(0,0,1;0rad)
  Shapes = -> [Cylinder152,Cylinder151]
FEATURE [Sketcher::SketchObject] Sketch048  label="top016"
  FullyConstrained = true
  sketch-geometry (2):
    g0: Circle CenterX=0 CenterY=-150 CenterZ=0 NormalX=0 NormalY=0 NormalZ=1 AngleXU=0 Radius=98
    g1: Circle CenterX=0 CenterY=-150 CenterZ=0 NormalX=0 NormalY=0 NormalZ=1 AngleXU=0 Radius=76
  constraints (5):
    c: PointOnObject(g0,g-2)
    c: Diameter(g0) = 196
    c: DistanceY(g0) = -150
    c: Coincident(g1,g0)
    c: Radius(g1) = 76
FEATURE [Part::Extrusion] Extrude030  label="TupeConnectLevel005"
  Base = -> Sketch048
  Dir = (0,0,1)
  DirMode = 2
  FaceMakerClass = Part::FaceMakerBullseye
  LengthFwd = 5
  LengthRev = 0
  Placement = pos=(0,0,-65) rot=(0,0,1;0rad)
  Solid = true
  Symmetric = false
FEATURE [Sketcher::SketchObject] Sketch049
  FullyConstrained = true
  sketch-geometry (4):
    g0: Circle CenterX=0 CenterY=-68 CenterZ=0 NormalX=0 NormalY=0 NormalZ=1 AngleXU=0 Radius=2.8
    g1: Circle CenterX=82 CenterY=-150 CenterZ=0 NormalX=0 NormalY=0 NormalZ=1 AngleXU=0 Radius=2.8
    g2: Circle CenterX=0 CenterY=-232 CenterZ=0 NormalX=0 NormalY=0 NormalZ=1 AngleXU=0 Radius=2.8
    g3: Circle CenterX=-82 CenterY=-150 CenterZ=0 NormalX=0 NormalY=0 NormalZ=1 AngleXU=0 Radius=2.8
  constraints (12):
    c: PointOnObject(g0,g-2)
    c: DistanceY(g1) = -150
    c: DistanceY(g1,g3) = 0
    c: DistanceX(g2) = 0
    c: DistanceX(g1) = 82
    c: Equal(g1,g0)
    c: Equal(g1,g3)
    c: Equal(g1,g2)
    c: Diameter(g1) = 5.6
    c: DistanceX(g3) = -82
    c: DistanceY(g3,g0) = 82
    c: DistanceY(g2,g3) = 82
FEATURE [Part::Extrusion] Extrude031  label="m4HeatSetVerCuts004"
  Base = -> Sketch049
  Dir = (0,0,1)
  DirMode = 2
  FaceMakerClass = Part::FaceMakerBullseye
  LengthFwd = 20
  LengthRev = 0
  Placement = pos=(0,0,-193) rot=(0,0,1;0rad)
  Solid = true
  Symmetric = false
FEATURE [Part::FeaturePython] Tube006  # WARN: FeaturePython — macro-defined, semantics opaque (R4)
  AttacherType = Attacher::AttachEngine3D
  Height = 65
  InnerRadius = 94
  OuterRadius = 98
  Placement = pos=(0,-150,-125) rot=(0,0,1;0rad)
FEATURE [Part::MultiFuse] Fusion095  label="tube5to005"
  Placement = pos=(0,0,-125) rot=(0,0,1;0rad)
  Shapes = -> [Extrude030,Tube006]
FEATURE [Part::Cut] Cut047  label="tube4to006"
  Base = -> Fusion095
  Tool = -> Fusion096
FEATURE [Part::Cut] Cut048  label="tube4to5s001"
  Base = -> Cut047
  Tool = -> Extrude031
FEATURE [Part::Fillet] Fillet003  label="level5s002"
  Base = -> Cut048
  Edges = 3 edges r=3: [Edge3,Edge7,Edge32]
FEATURE [Part::Cut] Cut049  label="cutAddOn"
  Base = -> Tube005
  Placement = pos=(0,0,0.25) rot=(0,0,1;0rad)
  Tool = -> Fillet003
FEATURE [Part::MultiFuse] Fusion097  label="tube4to3S"
  Shapes = -> [Cut042,Cut049]
FEATURE [Part::Fillet] Fillet004  label="tube4to3s"
  Base = -> Fusion097
  Edges = 1 edges r=3: [Edge3]
FEATURE [Part::Cylinder] Cylinder153
  Angle = 360
  AttacherType = Attacher::AttachEngine3D
  FirstAngle = 0
  Height = 300
  Placement = pos=(0,0,90) rot=(1,0,0;1.5708rad)
  Radius = 2.13
  SecondAngle = 0
FEATURE [Part::Cylinder] Cylinder154
  Angle = 360
  AttacherType = Attacher::AttachEngine3D
  FirstAngle = 0
  Height = 300
  Placement = pos=(-150,-150,90) rot=(0.57735,0.57735,0.57735;2.0944rad)
  Radius = 2.13
  SecondAngle = 0
FEATURE [Part::MultiFuse] Fusion099  label="m4Cuts016"
  Placement = pos=(0,0,-321) rot=(0,0,1;0rad)
  Shapes = -> [Cylinder154,Cylinder153]
FEATURE [Sketcher::SketchObject] Sketch050  label="top017"
  FullyConstrained = true
  sketch-geometry (2):
    g0: Circle CenterX=0 CenterY=-150 CenterZ=0 NormalX=0 NormalY=0 NormalZ=1 AngleXU=0 Radius=98
    g1: Circle CenterX=0 CenterY=-150 CenterZ=0 NormalX=0 NormalY=0 NormalZ=1 AngleXU=0 Radius=76
  constraints (5):
    c: PointOnObject(g0,g-2)
    c: Diameter(g0) = 196
    c: DistanceY(g0) = -150
    c: Coincident(g1,g0)
    c: Radius(g1) = 76
FEATURE [Part::Extrusion] Extrude032  label="TupeConnectLevel006"
  Base = -> Sketch050
  Dir = (0,0,1)
  DirMode = 2
  FaceMakerClass = Part::FaceMakerBullseye
  LengthFwd = 5
  LengthRev = 0
  Placement = pos=(0,0,-65) rot=(0,0,1;0rad)
  Solid = true
  Symmetric = false
FEATURE [Sketcher::SketchObject] Sketch051
  FullyConstrained = true
  sketch-geometry (4):
    g0: Circle CenterX=0 CenterY=-68 CenterZ=0 NormalX=0 NormalY=0 NormalZ=1 AngleXU=0 Radius=2.8
    g1: Circle CenterX=82 CenterY=-150 CenterZ=0 NormalX=0 NormalY=0 NormalZ=1 AngleXU=0 Radius=2.8
    g2: Circle CenterX=0 CenterY=-232 CenterZ=0 NormalX=0 NormalY=0 NormalZ=1 AngleXU=0 Radius=2.8
    g3: Circle CenterX=-82 CenterY=-150 CenterZ=0 NormalX=0 NormalY=0 NormalZ=1 AngleXU=0 Radius=2.8
  constraints (12):
    c: PointOnObject(g0,g-2)
    c: DistanceY(g1) = -150
    c: DistanceY(g1,g3) = 0
    c: DistanceX(g2) = 0
    c: DistanceX(g1) = 82
    c: Equal(g1,g0)
    c: Equal(g1,g3)
    c: Equal(g1,g2)
    c: Diameter(g1) = 5.6
    c: DistanceX(g3) = -82
    c: DistanceY(g3,g0) = 82
    c: DistanceY(g2,g3) = 82
FEATURE [Part::Extrusion] Extrude033  label="m4HeatSetVerCuts005"
  Base = -> Sketch051
  Dir = (0,0,1)
  DirMode = 2
  FaceMakerClass = Part::FaceMakerBullseye
  LengthFwd = 20
  LengthRev = 0
  Placement = pos=(0,0,-193) rot=(0,0,1;0rad)
  Solid = true
  Symmetric = false
FEATURE [Part::FeaturePython] Tube007  # WARN: FeaturePython — macro-defined, semantics opaque (R4)
  AttacherType = Attacher::AttachEngine3D
  Height = 3
  InnerRadius = 95
  OuterRadius = 98
  Placement = pos=(0,-150,-188) rot=(0,0,1;0rad)
FEATURE [Part::FeaturePython] Tube008  # WARN: FeaturePython — macro-defined, semantics opaque (R4)
  AttacherType = Attacher::AttachEngine3D
  Height = 65
  InnerRadius = 94
  OuterRadius = 98
  Placement = pos=(0,-150,-125) rot=(0,0,1;0rad)
FEATURE [Part::MultiFuse] Fusion098  label="tube5to006"
  Placement = pos=(0,0,-125) rot=(0,0,1;0rad)
  Shapes = -> [Extrude032,Tube008]
FEATURE [Part::Cut] Cut050  label="tube4to007"
  Base = -> Fusion098
  Tool = -> Fusion099
FEATURE [Part::Cut] Cut051  label="tube4to5s002"
  Base = -> Cut050
  Tool = -> Extrude033
FEATURE [Part::Fillet] Fillet005  label="level5s003"
  Base = -> Cut051
  Edges = 3 edges r=3: [Edge3,Edge7,Edge32]
FEATURE [Part::Cut] Cut052  label="cutAddOn001"
  Base = -> Tube007
  Placement = pos=(0,0,125.25) rot=(0,0,1;0rad)
  Tool = -> Fillet005
FEATURE [Part::MultiFuse] Fusion100  label="level3to2"
  Shapes = -> [Cut046,Cut052]
FEATURE [Part::Fillet] Fillet006  label="level003to2s"
  Base = -> Fusion100
  Edges = 1 edges r=3: [Edge5]
FEATURE [Sketcher::SketchObject] Sketch054
  FullyConstrained = true
  Placement = pos=(0,0,0) rot=(1,0,0;1.5708rad)
  sketch-geometry (8):
    g0: LineSegment StartX=-20.75 StartY=-250 StartZ=0 EndX=-12.75 EndY=-250 EndZ=0
    g1: LineSegment StartX=-12.75 StartY=-250 StartZ=0 EndX=-12.75 EndY=-275.75 EndZ=0
    g2: LineSegment StartX=-12.75 StartY=-275.75 StartZ=0 EndX=12.75 EndY=-275.75 EndZ=0
    g3: LineSegment StartX=12.75 StartY=-275.75 StartZ=0 EndX=12.75 EndY=-250 EndZ=0
    g4: LineSegment StartX=12.75 StartY=-250 StartZ=0 EndX=20.75 EndY=-250 EndZ=0
    g5: LineSegment StartX=20.75 StartY=-250 StartZ=0 EndX=20.75 EndY=-283.75 EndZ=0
    g6: LineSegment StartX=20.75 StartY=-283.75 StartZ=0 EndX=-20.75 EndY=-283.75 EndZ=0
    g7: LineSegment StartX=-20.75 StartY=-283.75 StartZ=0 EndX=-20.75 EndY=-250 EndZ=0
  constraints (24):
    c: Horizontal(g0)
    c: Vertical(g1)
    c: Coincident(g2,g1)
    c: Horizontal(g2)
    c: Vertical(g3)
    c: Coincident(g4,g3)
    c: Horizontal(g4)
    c: Coincident(g5,g4)
    c: Vertical(g5)
    c: Coincident(g6,g5)
    c: Horizontal(g6)
    c: Coincident(g7,g6)
    c: Coincident(g7,g0)
    c: Vertical(g7)
    c: Coincident(g0,g1)
    c: DistanceY(g0) = -250
    c: DistanceX(g0) = -12.75
    c: DistanceX(g3) = 12.75
    c: DistanceY(g1) = -275.75
    c: Coincident(g3,g2)
    c: DistanceY(g3,g0) = 0
    c: DistanceX(g0,g0) = 8
    c: DistanceX(g3,g4) = 8
    c: DistanceY(g5,g2) = 8
FEATURE [Part::Extrusion] Extrude036
  Base = -> Sketch054
  Dir = (0,-1,-3e-16)
  DirMode = 2
  FaceMakerClass = Part::FaceMakerBullseye
  LengthFwd = 100
  LengthRev = 0
  Placement = pos=(0,-70,0) rot=(0,0,1;0rad)
  Solid = true
  Symmetric = false
FEATURE [Part::Fillet] Fillet008
  Base = -> Extrude036
  Edges = 2 edges r=5: [Edge17,Edge20]
FEATURE [Part::Fillet] Fillet009  label="framingSupportsHolders"
  Base = -> Fillet008
  Edges = 2 edges r=2: [Edge26,Edge28]
FEATURE [Part::MultiFuse] Fusion104
  Shapes = -> [Fillet009,Cut041]
FEATURE [Part::Fillet] Fillet010  label="level5s005"
  Base = -> Fusion104
  Edges = 2 edges r=5: [Edge40,Edge46]
FEATURE [Mesh::Feature] tinker
  Placement = pos=(3,-245,-135) rot=(1,0,0;1.5708rad)
FEATURE [Sketcher::SketchObject] Sketch055
  FullyConstrained = false
  Placement = pos=(0,0,0) rot=(1,0,0;1.5708rad)
  sketch-geometry (884):
    g0: LineSegment StartX=35.7189 StartY=14.4677 StartZ=0 EndX=35.5415 EndY=14.2824 EndZ=0
    g1: LineSegment StartX=35.5415 StartY=14.2079 StartZ=0 EndX=35.4533 EndY=14.1342 EndZ=0
    g2: LineSegment StartX=35.4533 StartY=14.1342 StartZ=0 EndX=35.4583 EndY=14.0618 EndZ=0
    g3: LineSegment StartX=35.4583 StartY=14.0618 StartZ=0 EndX=35.3195 EndY=13.9216 EndZ=0
    g4: LineSegment StartX=35.3195 StartY=13.9216 StartZ=0 EndX=35.3195 EndY=13.853 EndZ=0
    g5: LineSegment StartX=35.3195 StartY=13.853 StartZ=0 EndX=35.248 EndY=13.7975 EndZ=0
    g6: LineSegment StartX=35.248 StartY=13.7975 StartZ=0 EndX=35.248 EndY=13.6573 EndZ=0
    g7: LineSegment StartX=35.248 StartY=13.6573 StartZ=0 EndX=35.1825 EndY=13.5912 EndZ=0
    g8: LineSegment StartX=35.1825 StartY=13.5912 StartZ=0 EndX=35.1825 EndY=13.2647 EndZ=0
    g9: LineSegment StartX=35.1825 StartY=13.2647 StartZ=0 EndX=35.0994 EndY=13.159 EndZ=0
    g10: LineSegment StartX=35.0994 StartY=13.159 StartZ=0 EndX=35.0994 EndY=13.0459 EndZ=0
    g11: LineSegment StartX=35.0994 StartY=13.0459 StartZ=0 EndX=35.0336 EndY=12.9565 EndZ=0
    g12: LineSegment StartX=35.0336 StartY=12.9565 StartZ=0 EndX=35.0336 EndY=12.3489 EndZ=0
    g13: LineSegment StartX=35.0336 StartY=12.3489 StartZ=0 EndX=35.1008 EndY=12.3489 EndZ=0
    g14: LineSegment StartX=35.1008 StartY=12.3489 StartZ=0 EndX=35.1008 EndY=12.2102 EndZ=0
    g15: LineSegment StartX=35.1008 StartY=12.2102 StartZ=0 EndX=35.1709 EndY=12.2072 EndZ=0
    g16: LineSegment StartX=35.1709 StartY=12.2072 StartZ=0 EndX=35.1709 EndY=11.9948 EndZ=0
    g17: LineSegment StartX=35.1709 StartY=11.9948 StartZ=0 EndX=35.2359 EndY=11.9948 EndZ=0
    g18: LineSegment StartX=35.2359 StartY=11.9948 StartZ=0 EndX=35.2359 EndY=11.9181 EndZ=0
    g19: LineSegment StartX=35.2359 StartY=11.9181 StartZ=0 EndX=35.3001 EndY=11.9181 EndZ=0
    g20: LineSegment StartX=35.3001 StartY=11.9181 StartZ=0 EndX=35.3001 EndY=11.8402 EndZ=0
    g21: LineSegment StartX=35.3001 StartY=11.8402 StartZ=0 EndX=35.3675 EndY=11.8402 EndZ=0
    g22: LineSegment StartX=35.3675 StartY=11.8402 StartZ=0 EndX=35.3675 EndY=11.2433 EndZ=0
    g23: LineSegment StartX=35.3675 StartY=11.2433 StartZ=0 EndX=35.435 EndY=11.2433 EndZ=0
    g24: LineSegment StartX=35.435 StartY=11.2433 StartZ=0 EndX=35.435 EndY=11.1727 EndZ=0
    g25: LineSegment StartX=35.435 StartY=11.1727 StartZ=0 EndX=35.5098 EndY=11.1727 EndZ=0
    g26: LineSegment StartX=35.5098 StartY=11.1727 StartZ=0 EndX=35.5098 EndY=11.1026 EndZ=0
    g27: LineSegment StartX=35.5098 StartY=11.1026 StartZ=0 EndX=35.6558 EndY=11.1026 EndZ=0
    g28: LineSegment StartX=35.6558 StartY=11.1026 StartZ=0 EndX=35.6558 EndY=11.0252 EndZ=0
    g29: LineSegment StartX=35.6558 StartY=11.0252 StartZ=0 EndX=35.7128 EndY=11.0252 EndZ=0
    g30: LineSegment StartX=35.7128 StartY=11.0252 StartZ=0 EndX=35.7128 EndY=10.7682 EndZ=0
    g31: LineSegment StartX=35.7128 StartY=10.7682 StartZ=0 EndX=35.7756 EndY=10.7681 EndZ=0
    g32: LineSegment StartX=35.7756 StartY=10.7681 StartZ=0 EndX=35.7756 EndY=10.5644 EndZ=0
    g33: LineSegment StartX=35.7756 StartY=10.5644 StartZ=0 EndX=35.846 EndY=10.5644 EndZ=0
    g34: LineSegment StartX=35.846 StartY=10.5644 StartZ=0 EndX=35.846 EndY=10.4767 EndZ=0
    g35: LineSegment StartX=35.846 StartY=10.4767 StartZ=0 EndX=35.988 EndY=10.4767 EndZ=0
    g36: LineSegment StartX=35.988 StartY=10.4767 StartZ=0 EndX=35.988 EndY=10.4228 EndZ=0
    g37: LineSegment StartX=35.988 StartY=10.4228 StartZ=0 EndX=36.1201 EndY=10.4228 EndZ=0
    g38: LineSegment StartX=36.1201 StartY=10.4228 StartZ=0 EndX=36.1201 EndY=10.2907 EndZ=0
    g39: LineSegment StartX=36.1201 StartY=10.2907 StartZ=0 EndX=36.1926 EndY=10.2907 EndZ=0
    g40: LineSegment StartX=36.1926 StartY=10.2907 StartZ=0 EndX=36.1926 EndY=10.1585 EndZ=0
    g41: LineSegment StartX=36.1926 StartY=10.1585 StartZ=0 EndX=36.2533 EndY=10.1585 EndZ=0
    g42: LineSegment StartX=36.2533 StartY=10.1585 StartZ=0 EndX=36.2533 EndY=10.0897 EndZ=0
    g43: LineSegment StartX=36.2533 StartY=10.0897 StartZ=0 EndX=36.3179 EndY=10.0897 EndZ=0
    g44: LineSegment StartX=36.3179 StartY=10.0897 StartZ=0 EndX=36.3179 EndY=9.8871 EndZ=0
    g45: LineSegment StartX=36.3179 StartY=9.8871 StartZ=0 EndX=36.3888 EndY=9.8871 EndZ=0
    g46: LineSegment StartX=36.3888 StartY=9.8871 StartZ=0 EndX=36.3888 EndY=9.73503 EndZ=0
    g47: LineSegment StartX=36.3888 StartY=9.73503 StartZ=0 EndX=36.4516 EndY=9.73503 EndZ=0
    g48: LineSegment StartX=36.4516 StartY=9.73503 StartZ=0 EndX=36.4516 EndY=9.65617 EndZ=0
    g49: LineSegment StartX=36.4516 StartY=9.65617 StartZ=0 EndX=36.6707 EndY=9.65617 EndZ=0
    g50: LineSegment StartX=36.6707 StartY=9.65617 StartZ=0 EndX=36.6707 EndY=9.58899 EndZ=0
    g51: LineSegment StartX=36.6707 StartY=9.58899 StartZ=0 EndX=36.7335 EndY=9.58899 EndZ=0
    g52: LineSegment StartX=36.7335 StartY=9.58899 StartZ=0 EndX=36.7335 EndY=9.51158 EndZ=0
    g53: LineSegment StartX=36.7335 StartY=9.51158 StartZ=0 EndX=36.7948 EndY=9.51158 EndZ=0
    g54: LineSegment StartX=36.7948 StartY=9.51158 StartZ=0 EndX=36.7948 EndY=9.40351 EndZ=0
    g55: LineSegment StartX=36.7948 StartY=9.40351 StartZ=0 EndX=36.8664 EndY=9.40351 EndZ=0
    g56: LineSegment StartX=36.8664 StartY=9.40351 StartZ=0 EndX=36.8664 EndY=9.2487 EndZ=0
    g57: LineSegment StartX=36.8664 StartY=9.2487 StartZ=0 EndX=36.9292 EndY=9.2487 EndZ=0
    g58: LineSegment StartX=36.9292 StartY=9.2487 StartZ=0 EndX=36.9292 EndY=9.18298 EndZ=0
    g59: LineSegment StartX=36.9292 StartY=9.18298 StartZ=0 EndX=37.0036 EndY=9.18298 EndZ=0
    g60: LineSegment StartX=37.0036 StartY=9.18298 StartZ=0 EndX=37.0036 EndY=9.12121 EndZ=0
    g61: LineSegment StartX=37.0036 StartY=9.12121 StartZ=0 EndX=37.066 EndY=9.12121 EndZ=0
    g62: LineSegment StartX=37.066 StartY=9.12121 StartZ=0 EndX=37.066 EndY=8.98122 EndZ=0
    g63: LineSegment StartX=37.066 StartY=8.98122 StartZ=0 EndX=37.1365 EndY=8.98122 EndZ=0
    g64: LineSegment StartX=37.1365 StartY=8.98122 StartZ=0 EndX=37.1365 EndY=8.85617 EndZ=0
    g65: LineSegment StartX=37.1365 StartY=8.85617 StartZ=0 EndX=37.2117 EndY=8.85617 EndZ=0
    g66: LineSegment StartX=37.2117 StartY=8.85617 StartZ=0 EndX=37.2117 EndY=8.77808 EndZ=0
    g67: LineSegment StartX=37.2117 StartY=8.77808 StartZ=0 EndX=37.276 EndY=8.7779 EndZ=0
    g68: LineSegment StartX=37.276 StartY=8.7779 StartZ=0 EndX=37.276 EndY=8.70839 EndZ=0
    g69: LineSegment StartX=37.276 StartY=8.70839 StartZ=0 EndX=37.3475 EndY=8.70839 EndZ=0
    g70: LineSegment StartX=37.3475 StartY=8.70839 StartZ=0 EndX=37.3475 EndY=8.58602 EndZ=0
    g71: LineSegment StartX=37.3475 StartY=8.58602 StartZ=0 EndX=37.4111 EndY=8.58602 EndZ=0
    g72: LineSegment StartX=37.4111 StartY=8.58602 StartZ=0 EndX=37.4111 EndY=8.50272 EndZ=0
    g73: LineSegment StartX=37.4111 StartY=8.50272 StartZ=0 EndX=37.4778 EndY=8.50272 EndZ=0
    g74: LineSegment StartX=37.4778 StartY=8.50272 StartZ=0 EndX=37.4778 EndY=8.37852 EndZ=0
    g75: LineSegment StartX=37.4778 StartY=8.37852 StartZ=0 EndX=37.55 EndY=8.37852 EndZ=0
    g76: LineSegment StartX=37.55 StartY=8.37852 StartZ=0 EndX=37.55 EndY=8.29594 EndZ=0
    g77: LineSegment StartX=37.55 StartY=8.29594 StartZ=0 EndX=37.6238 EndY=8.29594 EndZ=0
    g78: LineSegment StartX=37.6238 StartY=8.29594 StartZ=0 EndX=37.6238 EndY=8.20831 EndZ=0
    g79: LineSegment StartX=37.6238 StartY=8.20831 StartZ=0 EndX=37.6953 EndY=8.21123 EndZ=0
    g80: LineSegment StartX=37.6953 StartY=8.21123 StartZ=0 EndX=37.6953 EndY=8.14022 EndZ=0
    g81: LineSegment StartX=37.6953 StartY=8.14022 StartZ=0 EndX=37.7536 EndY=8.14414 EndZ=0
    g82: LineSegment StartX=37.7536 StartY=8.14414 StartZ=0 EndX=37.7574 EndY=8.06459 EndZ=0
    g83: LineSegment StartX=37.7574 StartY=8.06459 StartZ=0 EndX=37.8181 EndY=8.06459 EndZ=0
    g84: LineSegment StartX=37.8181 StartY=8.06459 StartZ=0 EndX=37.8216 EndY=7.98967 EndZ=0
    g85: LineSegment StartX=37.8216 StartY=7.98967 StartZ=0 EndX=38.1025 EndY=7.98967 EndZ=0
    g86: LineSegment StartX=38.1025 StartY=7.98967 StartZ=0 EndX=38.1917 EndY=8.08042 EndZ=0
    g87: LineSegment StartX=38.1917 StartY=8.08042 StartZ=0 EndX=38.2417 EndY=8.08577 EndZ=0
    g88: LineSegment StartX=38.2417 StartY=8.08577 StartZ=0 EndX=38.4557 EndY=8.32302 EndZ=0
    g89: LineSegment StartX=38.4557 StartY=8.32302 StartZ=0 EndX=38.5235 EndY=8.32302 EndZ=0
    g90: LineSegment StartX=38.5235 StartY=8.32302 StartZ=0 EndX=38.5887 EndY=8.40314 EndZ=0
    g91: LineSegment StartX=38.5887 StartY=8.40314 StartZ=0 EndX=38.6773 EndY=8.40314 EndZ=0
    g92: LineSegment StartX=38.6773 StartY=8.40314 StartZ=0 EndX=39.0643 EndY=8.80818 EndZ=0
    g93: LineSegment StartX=39.0643 StartY=8.80818 StartZ=0 EndX=39.152 EndY=8.80818 EndZ=0
    g94: LineSegment StartX=39.152 StartY=8.80818 StartZ=0 EndX=39.5355 EndY=9.19803 EndZ=0
    g95: LineSegment StartX=39.5355 StartY=9.19803 StartZ=0 EndX=39.6318 EndY=9.19803 EndZ=0
    g96: LineSegment StartX=39.6318 StartY=9.19803 StartZ=0 EndX=39.792 EndY=9.38195 EndZ=0
    g97: LineSegment StartX=39.792 StartY=9.38195 StartZ=0 EndX=39.7884 EndY=9.45608 EndZ=0
    g98: LineSegment StartX=39.7884 StartY=9.45608 StartZ=0 EndX=39.9772 EndY=9.63446 EndZ=0
    g99: LineSegment StartX=39.9772 StartY=9.63446 StartZ=0 EndX=39.9772 EndY=9.72533 EndZ=0
    g100: LineSegment StartX=39.9772 StartY=9.72533 StartZ=0 EndX=40.1697 EndY=9.91904 EndZ=0
    g101: LineSegment StartX=40.1697 StartY=9.91904 StartZ=0 EndX=40.1746 EndY=9.99558 EndZ=0
    g102: LineSegment StartX=40.1746 StartY=9.99558 StartZ=0 EndX=40.2388 EndY=10.0603 EndZ=0
    g103: LineSegment StartX=40.2388 StartY=10.0603 StartZ=0 EndX=40.2423 EndY=10.1261 EndZ=0
    g104: LineSegment StartX=40.2423 StartY=10.1261 StartZ=0 EndX=40.5948 EndY=10.4793 EndZ=0
    g105: LineSegment StartX=40.5948 StartY=10.4793 StartZ=0 EndX=40.5948 EndY=10.5499 EndZ=0
    g106: LineSegment StartX=40.5948 StartY=10.5499 StartZ=0 EndX=40.6701 EndY=10.618 EndZ=0
    g107: LineSegment StartX=40.6701 StartY=10.618 StartZ=0 EndX=40.6581 EndY=10.6527 EndZ=0
    g108: LineSegment StartX=40.6581 StartY=10.6527 StartZ=0 EndX=40.6988 EndY=10.6527 EndZ=0
    g109: LineSegment StartX=40.6988 StartY=10.6527 StartZ=0 EndX=40.9317 EndY=10.8877 EndZ=0
    g110: LineSegment StartX=40.9317 StartY=10.8877 StartZ=0 EndX=40.9317 EndY=10.9592 EndZ=0
    g111: LineSegment StartX=40.9317 StartY=10.9592 StartZ=0 EndX=41.0136 EndY=11.0405 EndZ=0
    g112: LineSegment StartX=41.0136 StartY=11.0405 StartZ=0 EndX=41.0068 EndY=11.1648 EndZ=0
    g113: LineSegment StartX=41.0068 StartY=11.1648 StartZ=0 EndX=41.0763 EndY=11.2275 EndZ=0
    g114: LineSegment StartX=41.0763 StartY=11.2275 StartZ=0 EndX=41.0723 EndY=11.2979 EndZ=0
    g115: LineSegment StartX=41.0723 StartY=11.2979 StartZ=0 EndX=41.15 EndY=11.3821 EndZ=0
    g116: LineSegment StartX=41.15 StartY=11.3821 StartZ=0 EndX=41.15 EndY=11.5724 EndZ=0
    g117: LineSegment StartX=41.15 StartY=11.5724 StartZ=0 EndX=41.2317 EndY=11.6351 EndZ=0
    g118: LineSegment StartX=41.2317 StartY=11.6351 StartZ=0 EndX=41.2155 EndY=11.7717 EndZ=0
    g119: LineSegment StartX=41.2155 StartY=11.7717 StartZ=0 EndX=41.2837 EndY=11.8432 EndZ=0
    g120: LineSegment StartX=41.2837 StartY=11.8432 StartZ=0 EndX=41.2786 EndY=11.8698 EndZ=0
    g121: LineSegment StartX=41.2786 StartY=11.8698 StartZ=0 EndX=41.3138 EndY=11.8698 EndZ=0
    g122: LineSegment StartX=41.3138 StartY=11.8698 StartZ=0 EndX=41.5455 EndY=12.1045 EndZ=0
    g123: LineSegment StartX=41.5455 StartY=12.1045 StartZ=0 EndX=41.5618 EndY=12.4305 EndZ=0
    g124: LineSegment StartX=41.5618 StartY=12.4305 StartZ=0 EndX=41.6277 EndY=12.505 EndZ=0
    g125: LineSegment StartX=41.6277 StartY=12.505 StartZ=0 EndX=41.6277 EndY=12.6108 EndZ=0
    g126: LineSegment StartX=41.6277 StartY=12.6108 StartZ=0 EndX=41.692 EndY=12.5393 EndZ=0
    g127: LineSegment StartX=41.692 StartY=12.5393 StartZ=0 EndX=41.7679 EndY=12.5393 EndZ=0
    g128: LineSegment StartX=41.7679 StartY=12.5393 StartZ=0 EndX=41.7679 EndY=12.4516 EndZ=0
    g129: LineSegment StartX=41.7679 StartY=12.4516 StartZ=0 EndX=41.8336 EndY=12.4546 EndZ=0
    g130: LineSegment StartX=41.8336 StartY=12.4546 StartZ=0 EndX=41.8336 EndY=12.3903 EndZ=0
    g131: LineSegment StartX=41.8336 StartY=12.3903 StartZ=0 EndX=41.8935 EndY=12.3903 EndZ=0
    g132: LineSegment StartX=41.8935 StartY=12.3903 StartZ=0 EndX=41.8935 EndY=12.3173 EndZ=0
    g133: LineSegment StartX=41.8935 StartY=12.3173 StartZ=0 EndX=41.9592 EndY=12.3217 EndZ=0
    g134: LineSegment StartX=41.9592 StartY=12.3217 StartZ=0 EndX=41.9651 EndY=12.2501 EndZ=0
    g135: LineSegment StartX=41.9651 StartY=12.2501 StartZ=0 EndX=42.0235 EndY=12.2559 EndZ=0
    g136: LineSegment StartX=42.0235 StartY=12.2559 StartZ=0 EndX=42.0264 EndY=12.1829 EndZ=0
    g137: LineSegment StartX=42.0264 StartY=12.1829 StartZ=0 EndX=42.1067 EndY=12.1888 EndZ=0
    g138: LineSegment StartX=42.1067 StartY=12.1888 StartZ=0 EndX=42.1067 EndY=12.1143 EndZ=0
    g139: LineSegment StartX=42.1067 StartY=12.1143 StartZ=0 EndX=42.2426 EndY=12.1216 EndZ=0
    g140: LineSegment StartX=42.2426 StartY=12.1216 StartZ=0 EndX=42.2426 EndY=12.0413 EndZ=0
    g141: LineSegment StartX=42.2426 StartY=12.0413 StartZ=0 EndX=42.4427 EndY=12.0413 EndZ=0
    g142: LineSegment StartX=42.4427 StartY=12.0413 StartZ=0 EndX=42.45 EndY=11.9566 EndZ=0
    g143: LineSegment StartX=42.45 StartY=11.9566 StartZ=0 EndX=42.523 EndY=11.9639 EndZ=0
    g144: LineSegment StartX=42.523 StartY=11.9639 StartZ=0 EndX=42.5274 EndY=11.8952 EndZ=0
    g145: LineSegment StartX=42.5274 StartY=11.8952 StartZ=0 EndX=42.5931 EndY=11.9011 EndZ=0
    g146: LineSegment StartX=42.5931 StartY=11.9011 StartZ=0 EndX=42.5931 EndY=11.847 EndZ=0
    g147: LineSegment StartX=42.5931 StartY=11.847 StartZ=0 EndX=42.6457 EndY=11.8499 EndZ=0
    g148: LineSegment StartX=42.6457 StartY=11.8499 StartZ=0 EndX=42.6457 EndY=11.7886 EndZ=0
    g149: LineSegment StartX=42.6457 StartY=11.7886 StartZ=0 EndX=42.7844 EndY=11.7886 EndZ=0
    g150: LineSegment StartX=42.7844 StartY=11.7886 StartZ=0 EndX=42.7844 EndY=11.7131 EndZ=0
    g151: LineSegment StartX=42.7844 StartY=11.7131 StartZ=0 EndX=43.0642 EndY=11.7131 EndZ=0
    g152: LineSegment StartX=43.0642 StartY=11.7131 StartZ=0 EndX=43.0642 EndY=11.6357 EndZ=0
    g153: LineSegment StartX=43.0642 StartY=11.6357 StartZ=0 EndX=43.1985 EndY=11.6357 EndZ=0
    g154: LineSegment StartX=43.1985 StartY=11.6357 StartZ=0 EndX=43.1985 EndY=11.5714 EndZ=0
    g155: LineSegment StartX=43.1985 StartY=11.5714 StartZ=0 EndX=43.2613 EndY=11.5714 EndZ=0
    g156: LineSegment StartX=43.2613 StartY=11.5714 StartZ=0 EndX=43.2613 EndY=11.5086 EndZ=0
    g157: LineSegment StartX=43.2613 StartY=11.5086 StartZ=0 EndX=43.3285 EndY=11.5086 EndZ=0
    g158: LineSegment StartX=43.3285 StartY=11.5086 StartZ=0 EndX=43.3285 EndY=11.4327 EndZ=0
    g159: LineSegment StartX=43.3285 StartY=11.4327 StartZ=0 EndX=43.3913 EndY=11.4371 EndZ=0
    g160: LineSegment StartX=43.3913 StartY=11.4371 StartZ=0 EndX=43.3932 EndY=11.3717 EndZ=0
    g161: LineSegment StartX=43.3932 StartY=11.3717 StartZ=0 EndX=43.7436 EndY=11.3717 EndZ=0
    g162: LineSegment StartX=43.7436 StartY=11.3717 StartZ=0 EndX=43.7436 EndY=11.3021 EndZ=0
    g163: LineSegment StartX=43.7436 StartY=11.3021 StartZ=0 EndX=43.8098 EndY=11.3021 EndZ=0
    g164: LineSegment StartX=43.8098 StartY=11.3021 StartZ=0 EndX=43.8134 EndY=11.2285 EndZ=0
    g165: LineSegment StartX=43.8134 StartY=11.2285 StartZ=0 EndX=44.0238 EndY=11.2285 EndZ=0
    g166: LineSegment StartX=44.0238 StartY=11.2285 StartZ=0 EndX=44.0238 EndY=11.1603 EndZ=0
    g167: LineSegment StartX=44.0238 StartY=11.1603 StartZ=0 EndX=44.1542 EndY=11.1603 EndZ=0
    g168: LineSegment StartX=44.1542 StartY=11.1603 StartZ=0 EndX=44.1506 EndY=11.0922 EndZ=0
    g169: LineSegment StartX=44.1506 StartY=11.0922 StartZ=0 EndX=44.2845 EndY=11.1005 EndZ=0
    g170: LineSegment StartX=44.2845 StartY=11.1005 StartZ=0 EndX=44.2845 EndY=11.0276 EndZ=0
    g171: LineSegment StartX=44.2845 StartY=11.0276 StartZ=0 EndX=44.3538 EndY=11.0312 EndZ=0
    g172: LineSegment StartX=44.3538 StartY=11.0312 StartZ=0 EndX=44.3538 EndY=10.9534 EndZ=0
    g173: LineSegment StartX=44.3538 StartY=10.9534 StartZ=0 EndX=44.4925 EndY=10.9534 EndZ=0
    g174: LineSegment StartX=44.4925 StartY=10.9534 StartZ=0 EndX=44.4925 EndY=10.9066 EndZ=0
    g175: LineSegment StartX=44.4925 StartY=10.9066 StartZ=0 EndX=44.8405 EndY=10.9066 EndZ=0
    g176: LineSegment StartX=44.8405 StartY=10.9066 StartZ=0 EndX=44.8405 EndY=10.8227 EndZ=0
    g177: LineSegment StartX=44.8405 StartY=10.8227 StartZ=0 EndX=44.9671 EndY=10.8245 EndZ=0
    g178: LineSegment StartX=44.9671 StartY=10.8245 StartZ=0 EndX=44.9671 EndY=10.7496 EndZ=0
    g179: LineSegment StartX=44.9671 StartY=10.7496 StartZ=0 EndX=45.2382 EndY=10.7496 EndZ=0
    g180: LineSegment StartX=45.2382 StartY=10.7496 StartZ=0 EndX=45.2382 EndY=10.6783 EndZ=0
    g181: LineSegment StartX=45.2382 StartY=10.6783 StartZ=0 EndX=45.438 EndY=10.6783 EndZ=0
    g182: LineSegment StartX=45.438 StartY=10.6783 StartZ=0 EndX=45.438 EndY=10.6176 EndZ=0
    g183: LineSegment StartX=45.438 StartY=10.6176 StartZ=0 EndX=45.8572 EndY=10.6176 EndZ=0
    g184: LineSegment StartX=45.8572 StartY=10.6176 StartZ=0 EndX=45.8572 EndY=10.548 EndZ=0
    g185: LineSegment StartX=45.8572 StartY=10.548 StartZ=0 EndX=46.2711 EndY=10.548 EndZ=0
    g186: LineSegment StartX=46.2711 StartY=10.548 StartZ=0 EndX=46.5712 EndY=10.876 EndZ=0
    g187: LineSegment StartX=46.5712 StartY=10.876 StartZ=0 EndX=46.568 EndY=10.9537 EndZ=0
    g188: LineSegment StartX=46.568 StartY=10.9537 StartZ=0 EndX=46.6513 EndY=11.0387 EndZ=0
    g189: LineSegment StartX=46.6513 StartY=11.0387 StartZ=0 EndX=46.6513 EndY=11.2162 EndZ=0
    g190: LineSegment StartX=46.6513 StartY=11.2162 StartZ=0 EndX=46.7535 EndY=11.317 EndZ=0
    g191: LineSegment StartX=46.7535 StartY=11.317 StartZ=0 EndX=46.7462 EndY=11.4353 EndZ=0
    g192: LineSegment StartX=46.7462 StartY=11.4353 StartZ=0 EndX=46.8178 EndY=11.5141 EndZ=0
    g193: LineSegment StartX=46.8178 StartY=11.5141 StartZ=0 EndX=46.8081 EndY=11.636 EndZ=0
    g194: LineSegment StartX=46.8081 StartY=11.636 StartZ=0 EndX=46.8919 EndY=11.7287 EndZ=0
    g195: LineSegment StartX=46.8919 StartY=11.7287 StartZ=0 EndX=46.8919 EndY=11.9142 EndZ=0
    g196: LineSegment StartX=46.8919 StartY=11.9142 StartZ=0 EndX=46.9704 EndY=12.0106 EndZ=0
    g197: LineSegment StartX=46.9704 StartY=12.0106 StartZ=0 EndX=46.9704 EndY=13.0147 EndZ=0
    g198: LineSegment StartX=46.9704 StartY=13.0147 StartZ=0 EndX=47.1435 EndY=13.1957 EndZ=0
    g199: LineSegment StartX=47.1435 StartY=13.1957 StartZ=0 EndX=47.1435 EndY=13.5812 EndZ=0
    g200: LineSegment StartX=47.1435 StartY=13.5812 StartZ=0 EndX=47.0232 EndY=13.5812 EndZ=0
    g201: LineSegment StartX=47.0232 StartY=13.5812 StartZ=0 EndX=47.0232 EndY=13.968 EndZ=0
    g202: LineSegment StartX=47.0232 StartY=13.968 StartZ=0 EndX=46.9387 EndY=13.981 EndZ=0
    g203: LineSegment StartX=46.9387 StartY=13.981 StartZ=0 EndX=46.9387 EndY=14.1923 EndZ=0
    g204: LineSegment StartX=46.9387 StartY=14.1923 StartZ=0 EndX=46.8607 EndY=14.189 EndZ=0
    g205: LineSegment StartX=46.8607 StartY=14.189 StartZ=0 EndX=46.8607 EndY=14.2768 EndZ=0
    g206: LineSegment StartX=46.8607 StartY=14.2768 StartZ=0 EndX=46.9745 EndY=14.4003 EndZ=0
    g207: LineSegment StartX=46.9745 StartY=14.4003 StartZ=0 EndX=46.9842 EndY=14.6473 EndZ=0
    g208: LineSegment StartX=46.9842 StartY=14.6473 StartZ=0 EndX=46.8672 EndY=14.6603 EndZ=0
    g209: LineSegment StartX=46.8672 StartY=14.6603 StartZ=0 EndX=46.8672 EndY=14.8066 EndZ=0
    g210: LineSegment StartX=46.8672 StartY=14.8066 StartZ=0 EndX=46.799 EndY=14.8131 EndZ=0
    g211: LineSegment StartX=46.799 StartY=14.8131 StartZ=0 EndX=46.7957 EndY=14.8846 EndZ=0
    g212: LineSegment StartX=46.7957 StartY=14.8846 StartZ=0 EndX=46.7372 EndY=14.8911 EndZ=0
    g213: LineSegment StartX=46.7372 StartY=14.8911 StartZ=0 EndX=46.7502 EndY=15.0699 EndZ=0
    g214: LineSegment StartX=46.7502 StartY=15.0699 StartZ=0 EndX=46.6592 EndY=15.0764 EndZ=0
    g215: LineSegment StartX=46.6592 StartY=15.0764 StartZ=0 EndX=46.6592 EndY=15.2096 EndZ=0
    g216: LineSegment StartX=46.6592 StartY=15.2096 StartZ=0 EndX=46.7535 EndY=15.2811 EndZ=0
    g217: LineSegment StartX=46.7535 StartY=15.2811 StartZ=0 EndX=47.5498 EndY=15.2811 EndZ=0
    g218: LineSegment StartX=47.5498 StartY=15.2811 StartZ=0 EndX=47.5498 EndY=15.2015 EndZ=0
    g219: LineSegment StartX=47.5498 StartY=15.2015 StartZ=0 EndX=48.1326 EndY=15.2015 EndZ=0
    g220: LineSegment StartX=48.1326 StartY=15.2015 StartZ=0 EndX=48.1915 EndY=15.2887 EndZ=0
    g221: LineSegment StartX=48.1915 StartY=15.2887 StartZ=0 EndX=48.2811 EndY=15.2887 EndZ=0
    g222: LineSegment StartX=48.2811 StartY=15.2887 StartZ=0 EndX=48.4046 EndY=15.4194 EndZ=0
    g223: LineSegment StartX=48.4046 StartY=15.4194 StartZ=0 EndX=48.6512 EndY=15.4194 EndZ=0
    g224: LineSegment StartX=48.6512 StartY=15.4194 StartZ=0 EndX=48.6512 EndY=15.3322 EndZ=0
    g225: LineSegment StartX=48.6512 StartY=15.3322 StartZ=0 EndX=48.9084 EndY=15.3322 EndZ=0
    g226: LineSegment StartX=48.9084 StartY=15.3322 StartZ=0 EndX=48.9084 EndY=15.2647 EndZ=0
    g227: LineSegment StartX=48.9084 StartY=15.2647 StartZ=0 EndX=49.1131 EndY=15.2647 EndZ=0
    g228: LineSegment StartX=49.1131 StartY=15.2647 StartZ=0 EndX=49.1131 EndY=15.171 EndZ=0
    g229: LineSegment StartX=49.1131 StartY=15.171 StartZ=0 EndX=49.344 EndY=15.171 EndZ=0
    g230: LineSegment StartX=49.344 StartY=15.171 StartZ=0 EndX=49.4317 EndY=15.2779 EndZ=0
    g231: LineSegment StartX=49.4317 StartY=15.2779 StartZ=0 EndX=49.513 EndY=15.2714 EndZ=0
    g232: LineSegment StartX=49.513 StartY=15.2714 StartZ=0 EndX=49.6365 EndY=15.4177 EndZ=0
    g233: LineSegment StartX=49.6365 StartY=15.4177 StartZ=0 EndX=51.1609 EndY=15.4177 EndZ=0
    g234: LineSegment StartX=51.1609 StartY=15.4177 StartZ=0 EndX=51.2713 EndY=15.4747 EndZ=0
    g235: LineSegment StartX=51.2713 StartY=15.4747 StartZ=0 EndX=51.8707 EndY=15.4747 EndZ=0
    g236: LineSegment StartX=51.8707 StartY=15.4747 StartZ=0 EndX=51.9501 EndY=15.5501 EndZ=0
    g237: LineSegment StartX=51.9501 StartY=15.5501 StartZ=0 EndX=52.0613 EndY=15.5501 EndZ=0
    g238: LineSegment StartX=52.0613 StartY=15.5501 StartZ=0 EndX=52.1566 EndY=15.6335 EndZ=0
    g239: LineSegment StartX=52.1566 StartY=15.6335 StartZ=0 EndX=53.0776 EndY=15.6335 EndZ=0
    g240: LineSegment StartX=53.0776 StartY=15.6335 StartZ=0 EndX=53.2557 EndY=15.8082 EndZ=0
    g241: LineSegment StartX=53.2557 StartY=15.8082 StartZ=0 EndX=53.2557 EndY=16.103 EndZ=0
    g242: LineSegment StartX=53.2557 StartY=16.103 StartZ=0 EndX=53.1958 EndY=16.103 EndZ=0
    g243: LineSegment StartX=53.1958 StartY=16.103 StartZ=0 EndX=53.1958 EndY=16.3046 EndZ=0
    g244: LineSegment StartX=53.1958 StartY=16.3046 StartZ=0 EndX=53.1301 EndY=16.3017 EndZ=0
    g245: LineSegment StartX=53.1301 StartY=16.3017 StartZ=0 EndX=53.1301 EndY=16.4404 EndZ=0
    g246: LineSegment StartX=53.1301 StartY=16.4404 StartZ=0 EndX=53.0594 EndY=16.4404 EndZ=0
    g247: LineSegment StartX=53.0594 StartY=16.4404 StartZ=0 EndX=53.0558 EndY=16.5171 EndZ=0
    g248: LineSegment StartX=53.0558 StartY=16.5171 StartZ=0 EndX=52.9773 EndY=16.5171 EndZ=0
    g249: LineSegment StartX=52.9773 StartY=16.5171 StartZ=0 EndX=52.9773 EndY=16.6455 EndZ=0
    g250: LineSegment StartX=52.9773 StartY=16.6455 StartZ=0 EndX=52.9219 EndY=16.6452 EndZ=0
    g251: LineSegment StartX=52.9219 StartY=16.6452 StartZ=0 EndX=52.9219 EndY=16.7146 EndZ=0
    g252: LineSegment StartX=52.9219 StartY=16.7146 StartZ=0 EndX=52.8549 EndY=16.7146 EndZ=0
    g253: LineSegment StartX=52.8549 StartY=16.7146 StartZ=0 EndX=52.8535 EndY=16.7863 EndZ=0
    g254: LineSegment StartX=52.8535 StartY=16.7863 StartZ=0 EndX=52.7868 EndY=16.7863 EndZ=0
    g255: LineSegment StartX=52.7868 StartY=16.7863 StartZ=0 EndX=52.7868 EndY=16.9211 EndZ=0
    g256: LineSegment StartX=52.7868 StartY=16.9211 StartZ=0 EndX=52.715 EndY=16.9211 EndZ=0
    g257: LineSegment StartX=52.715 StartY=16.9211 StartZ=0 EndX=52.715 EndY=16.98 EndZ=0
    g258: LineSegment StartX=52.715 StartY=16.98 StartZ=0 EndX=52.6457 EndY=16.98 EndZ=0
    g259: LineSegment StartX=52.6457 StartY=16.98 StartZ=0 EndX=52.6457 EndY=17.0366 EndZ=0
    g260: LineSegment StartX=52.6457 StartY=17.0366 StartZ=0 EndX=52.5763 EndY=17.0366 EndZ=0
    g261: LineSegment StartX=52.5763 StartY=17.0366 StartZ=0 EndX=52.5763 EndY=17.128 EndZ=0
    g262: LineSegment StartX=52.5763 StartY=17.128 StartZ=0 EndX=52.5147 EndY=17.128 EndZ=0
    g263: LineSegment StartX=52.5147 StartY=17.128 StartZ=0 EndX=52.5147 EndY=17.2695 EndZ=0
    g264: LineSegment StartX=52.5147 StartY=17.2695 StartZ=0 EndX=52.4502 EndY=17.2647 EndZ=0
    g265: LineSegment StartX=52.4502 StartY=17.2647 StartZ=0 EndX=52.4454 EndY=17.336 EndZ=0
    g266: LineSegment StartX=52.4454 StartY=17.336 StartZ=0 EndX=52.3797 EndY=17.3384 EndZ=0
    g267: LineSegment StartX=52.3797 StartY=17.3384 StartZ=0 EndX=52.3829 EndY=17.4058 EndZ=0
    g268: LineSegment StartX=52.3829 StartY=17.4058 StartZ=0 EndX=52.318 EndY=17.4026 EndZ=0
    g269: LineSegment StartX=52.318 StartY=17.4026 StartZ=0 EndX=52.318 EndY=17.4715 EndZ=0
    g270: LineSegment StartX=52.318 StartY=17.4715 StartZ=0 EndX=52.2451 EndY=17.4715 EndZ=0
    g271: LineSegment StartX=52.2451 StartY=17.4715 StartZ=0 EndX=52.2451 EndY=17.5364 EndZ=0
    g272: LineSegment StartX=52.2451 StartY=17.5364 StartZ=0 EndX=52.1833 EndY=17.5388 EndZ=0
    g273: LineSegment StartX=52.1833 StartY=17.5388 StartZ=0 EndX=52.1833 EndY=17.6077 EndZ=0
    g274: LineSegment StartX=52.1833 StartY=17.6077 StartZ=0 EndX=52.1144 EndY=17.6077 EndZ=0
    g275: LineSegment StartX=52.1144 StartY=17.6077 StartZ=0 EndX=52.1144 EndY=17.6741 EndZ=0
    g276: LineSegment StartX=52.1144 StartY=17.6741 StartZ=0 EndX=52.0495 EndY=17.6741 EndZ=0
    g277: LineSegment StartX=52.0495 StartY=17.6741 StartZ=0 EndX=52.0495 EndY=17.7495 EndZ=0
    g278: LineSegment StartX=52.0495 StartY=17.7495 StartZ=0 EndX=51.9017 EndY=17.7495 EndZ=0
    g279: LineSegment StartX=51.9017 StartY=17.7495 StartZ=0 EndX=51.9017 EndY=17.8092 EndZ=0
    g280: LineSegment StartX=51.9017 StartY=17.8092 StartZ=0 EndX=51.8351 EndY=17.8092 EndZ=0
    g281: LineSegment StartX=51.8351 StartY=17.8092 StartZ=0 EndX=51.8351 EndY=17.8911 EndZ=0
    g282: LineSegment StartX=51.8351 StartY=17.8911 StartZ=0 EndX=51.7639 EndY=17.8911 EndZ=0
    g283: LineSegment StartX=51.7639 StartY=17.8911 StartZ=0 EndX=51.7639 EndY=17.9626 EndZ=0
    g284: LineSegment StartX=51.7639 StartY=17.9626 StartZ=0 EndX=51.6325 EndY=17.9626 EndZ=0
    g285: LineSegment StartX=51.6325 StartY=17.9626 StartZ=0 EndX=51.6325 EndY=18.0284 EndZ=0
    g286: LineSegment StartX=51.6325 StartY=18.0284 StartZ=0 EndX=51.485 EndY=18.0284 EndZ=0
    g287: LineSegment StartX=51.485 StartY=18.0284 StartZ=0 EndX=51.485 EndY=18.0711 EndZ=0
    g288: LineSegment StartX=51.485 StartY=18.0711 StartZ=0 EndX=51.4163 EndY=18.0711 EndZ=0
    g289: LineSegment StartX=51.4163 StartY=18.0711 StartZ=0 EndX=51.4163 EndY=18.1587 EndZ=0
    g290: LineSegment StartX=51.4163 StartY=18.1587 StartZ=0 EndX=51.2878 EndY=18.1587 EndZ=0
    g291: LineSegment StartX=51.2878 StartY=18.1587 StartZ=0 EndX=51.2878 EndY=18.2275 EndZ=0
    g292: LineSegment StartX=51.2878 StartY=18.2275 StartZ=0 EndX=51.2232 EndY=18.2275 EndZ=0
    g293: LineSegment StartX=51.2232 StartY=18.2275 StartZ=0 EndX=51.2267 EndY=18.2921 EndZ=0
    g294: LineSegment StartX=51.2267 StartY=18.2921 StartZ=0 EndX=51.1526 EndY=18.2921 EndZ=0
    g295: LineSegment StartX=51.1526 StartY=18.2921 StartZ=0 EndX=51.1526 EndY=18.3662 EndZ=0
    g296: LineSegment StartX=51.1526 StartY=18.3662 StartZ=0 EndX=51.0845 EndY=18.3602 EndZ=0
    g297: LineSegment StartX=51.0845 StartY=18.3602 StartZ=0 EndX=51.0845 EndY=18.4424 EndZ=0
    g298: LineSegment StartX=51.0845 StartY=18.4424 StartZ=0 EndX=51.0222 EndY=18.4424 EndZ=0
    g299: LineSegment StartX=51.0222 StartY=18.4424 StartZ=0 EndX=51.0222 EndY=18.5138 EndZ=0
    g300: LineSegment StartX=51.0222 StartY=18.5138 StartZ=0 EndX=50.8169 EndY=18.5138 EndZ=0
    g301: LineSegment StartX=50.8169 StartY=18.5138 StartZ=0 EndX=50.7878 EndY=18.6026 EndZ=0
    g302: LineSegment StartX=50.7878 StartY=18.6026 StartZ=0 EndX=50.7494 EndY=18.6113 EndZ=0
    g303: LineSegment StartX=50.7494 StartY=18.6113 StartZ=0 EndX=50.7397 EndY=18.6731 EndZ=0
    g304: LineSegment StartX=50.7397 StartY=18.6731 StartZ=0 EndX=50.5414 EndY=18.6536 EndZ=0
    g305: LineSegment StartX=50.5414 StartY=18.6536 StartZ=0 EndX=50.5381 EndY=18.7381 EndZ=0
    g306: LineSegment StartX=50.5381 StartY=18.7381 StartZ=0 EndX=50.4114 EndY=18.7218 EndZ=0
    g307: LineSegment StartX=50.4114 StartY=18.7218 StartZ=0 EndX=50.3951 EndY=18.7934 EndZ=0
    g308: LineSegment StartX=50.3951 StartY=18.7934 StartZ=0 EndX=50.3334 EndY=18.7934 EndZ=0
    g309: LineSegment StartX=50.3334 StartY=18.7934 StartZ=0 EndX=50.3366 EndY=18.8389 EndZ=0
    g310: LineSegment StartX=50.3366 StartY=18.8389 StartZ=0 EndX=50.2066 EndY=18.8389 EndZ=0
    g311: LineSegment StartX=50.2066 StartY=18.8389 StartZ=0 EndX=50.2099 EndY=18.9201 EndZ=0
    g312: LineSegment StartX=50.2099 StartY=18.9201 StartZ=0 EndX=50.1254 EndY=18.9266 EndZ=0
    g313: LineSegment StartX=50.1254 StartY=18.9266 StartZ=0 EndX=50.1156 EndY=19.0046 EndZ=0
    g314: LineSegment StartX=50.1156 StartY=19.0046 StartZ=0 EndX=49.9986 EndY=18.9949 EndZ=0
    g315: LineSegment StartX=49.9986 StartY=18.9949 StartZ=0 EndX=49.9921 EndY=19.0859 EndZ=0
    g316: LineSegment StartX=49.9921 StartY=19.0859 StartZ=0 EndX=49.9368 EndY=19.0501 EndZ=0
    g317: LineSegment StartX=49.9368 StartY=19.0501 StartZ=0 EndX=49.9206 EndY=19.1509 EndZ=0
    g318: LineSegment StartX=49.9206 StartY=19.1509 StartZ=0 EndX=49.7971 EndY=19.1281 EndZ=0
    g319: LineSegment StartX=49.7971 StartY=19.1281 StartZ=0 EndX=49.8068 EndY=19.2029 EndZ=0
    g320: LineSegment StartX=49.8068 StartY=19.2029 StartZ=0 EndX=49.7288 EndY=19.1899 EndZ=0
    g321: LineSegment StartX=49.7288 StartY=19.1899 StartZ=0 EndX=49.7191 EndY=19.2582 EndZ=0
    g322: LineSegment StartX=49.7191 StartY=19.2582 StartZ=0 EndX=49.6606 EndY=19.2647 EndZ=0
    g323: LineSegment StartX=49.6606 StartY=19.2647 StartZ=0 EndX=49.6541 EndY=19.3329 EndZ=0
    g324: LineSegment StartX=49.6541 StartY=19.3329 StartZ=0 EndX=49.6021 EndY=19.3329 EndZ=0
    g325: LineSegment StartX=49.6021 StartY=19.3329 StartZ=0 EndX=49.5988 EndY=19.4077 EndZ=0
    g326: LineSegment StartX=49.5988 StartY=19.4077 StartZ=0 EndX=49.4623 EndY=19.3947 EndZ=0
    g327: LineSegment StartX=49.4623 StartY=19.3947 StartZ=0 EndX=49.4623 EndY=19.4727 EndZ=0
    g328: LineSegment StartX=49.4623 StartY=19.4727 StartZ=0 EndX=49.2543 EndY=19.4532 EndZ=0
    g329: LineSegment StartX=49.2543 StartY=19.4532 StartZ=0 EndX=49.2543 EndY=19.5279 EndZ=0
    g330: LineSegment StartX=49.2543 StartY=19.5279 StartZ=0 EndX=49.199 EndY=19.5279 EndZ=0
    g331: LineSegment StartX=49.199 StartY=19.5279 StartZ=0 EndX=49.199 EndY=19.6189 EndZ=0
    g332: LineSegment StartX=49.199 StartY=19.6189 StartZ=0 EndX=49.0658 EndY=19.6059 EndZ=0
    g333: LineSegment StartX=49.0658 StartY=19.6059 StartZ=0 EndX=49.0495 EndY=19.6612 EndZ=0
    g334: LineSegment StartX=49.0495 StartY=19.6612 StartZ=0 EndX=48.991 EndY=19.6547 EndZ=0
    g335: LineSegment StartX=48.991 StartY=19.6547 StartZ=0 EndX=48.9845 EndY=19.7359 EndZ=0
    g336: LineSegment StartX=48.9845 StartY=19.7359 StartZ=0 EndX=48.8577 EndY=19.7262 EndZ=0
    g337: LineSegment StartX=48.8577 StartY=19.7262 StartZ=0 EndX=48.8577 EndY=19.8149 EndZ=0
    g338: LineSegment StartX=48.8577 StartY=19.8149 StartZ=0 EndX=48.7743 EndY=19.8069 EndZ=0
    g339: LineSegment StartX=48.7743 StartY=19.8069 StartZ=0 EndX=48.7743 EndY=19.8894 EndZ=0
    g340: LineSegment StartX=48.7743 StartY=19.8894 StartZ=0 EndX=48.5854 EndY=19.8894 EndZ=0
    g341: LineSegment StartX=48.5854 StartY=19.8894 StartZ=0 EndX=48.5854 EndY=19.9533 EndZ=0
    g342: LineSegment StartX=48.5854 StartY=19.9533 StartZ=0 EndX=48.4417 EndY=19.9533 EndZ=0
    g343: LineSegment StartX=48.4417 StartY=19.9533 StartZ=0 EndX=48.4417 EndY=20.0118 EndZ=0
    g344: LineSegment StartX=48.4417 StartY=20.0118 StartZ=0 EndX=48.3751 EndY=20.0118 EndZ=0
    g345: LineSegment StartX=48.3751 StartY=20.0118 StartZ=0 EndX=48.3751 EndY=20.089 EndZ=0
    g346: LineSegment StartX=48.3751 StartY=20.089 StartZ=0 EndX=48.3033 EndY=20.089 EndZ=0
    g347: LineSegment StartX=48.3033 StartY=20.089 StartZ=0 EndX=48.3033 EndY=20.1524 EndZ=0
    g348: LineSegment StartX=48.3033 StartY=20.1524 StartZ=0 EndX=48.0916 EndY=20.1524 EndZ=0
    g349: LineSegment StartX=48.0916 StartY=20.1524 StartZ=0 EndX=48.0916 EndY=20.2331 EndZ=0
    g350: LineSegment StartX=48.0916 StartY=20.2331 StartZ=0 EndX=47.8912 EndY=20.2331 EndZ=0
    g351: LineSegment StartX=47.8912 StartY=20.2331 StartZ=0 EndX=47.8912 EndY=20.2962 EndZ=0
    g352: LineSegment StartX=47.8912 StartY=20.2962 StartZ=0 EndX=47.6864 EndY=20.2962 EndZ=0
    g353: LineSegment StartX=47.6864 StartY=20.2962 StartZ=0 EndX=47.6864 EndY=20.3681 EndZ=0
    g354: LineSegment StartX=47.6864 StartY=20.3681 StartZ=0 EndX=47.2898 EndY=20.3681 EndZ=0
    g355: LineSegment StartX=47.2898 StartY=20.3681 StartZ=0 EndX=47.2898 EndY=20.4313 EndZ=0
    g356: LineSegment StartX=47.2898 StartY=20.4313 StartZ=0 EndX=47.0094 EndY=20.4313 EndZ=0
    g357: LineSegment StartX=47.0094 StartY=20.4313 StartZ=0 EndX=47.0094 EndY=20.5033 EndZ=0
    g358: LineSegment StartX=47.0094 StartY=20.5033 StartZ=0 EndX=46.7265 EndY=20.5033 EndZ=0
    g359: LineSegment StartX=46.7265 StartY=20.5033 StartZ=0 EndX=46.7265 EndY=20.5623 EndZ=0
    g360: LineSegment StartX=46.7265 StartY=20.5623 StartZ=0 EndX=46.3195 EndY=20.5623 EndZ=0
    g361: LineSegment StartX=46.3195 StartY=20.5623 StartZ=0 EndX=46.2304 EndY=20.478 EndZ=0
    g362: LineSegment StartX=46.2304 StartY=20.478 StartZ=0 EndX=45.8403 EndY=20.478 EndZ=0
    g363: LineSegment StartX=45.8403 StartY=20.478 StartZ=0 EndX=45.7581 EndY=20.3987 EndZ=0
    g364: LineSegment StartX=45.7581 StartY=20.3987 StartZ=0 EndX=45.6847 EndY=20.3987 EndZ=0
    g365: LineSegment StartX=45.6847 StartY=20.3987 StartZ=0 EndX=45.6847 EndY=20.4757 EndZ=0
    g366: LineSegment StartX=45.6847 StartY=20.4757 StartZ=0 EndX=45.2353 EndY=20.4757 EndZ=0
    g367: LineSegment StartX=45.2353 StartY=20.4757 StartZ=0 EndX=45.1511 EndY=20.3964 EndZ=0
    g368: LineSegment StartX=45.1511 StartY=20.3964 StartZ=0 EndX=45.039 EndY=20.3905 EndZ=0
    g369: LineSegment StartX=45.1271 StartY=20.498 StartZ=0 EndX=45.039 EndY=20.3905 EndZ=0
    g370: LineSegment StartX=45.1271 StartY=20.498 StartZ=0 EndX=45.1672 EndY=20.498 EndZ=0
    g371: LineSegment StartX=45.1672 StartY=20.498 StartZ=0 EndX=45.2586 EndY=20.5605 EndZ=0
    g372: LineSegment StartX=45.2586 StartY=20.5605 StartZ=0 EndX=45.3242 EndY=20.5605 EndZ=0
    g373: LineSegment StartX=45.3242 StartY=20.5605 StartZ=0 EndX=45.4009 EndY=20.6461 EndZ=0
    g374: LineSegment StartX=45.4009 StartY=20.6461 StartZ=0 EndX=45.5221 EndY=20.6461 EndZ=0
    g375: LineSegment StartX=45.5221 StartY=20.6461 StartZ=0 EndX=45.6149 EndY=20.705 EndZ=0
    g376: LineSegment StartX=45.6149 StartY=20.705 StartZ=0 EndX=45.8042 EndY=20.705 EndZ=0
    g377: LineSegment StartX=45.8042 StartY=20.705 StartZ=0 EndX=45.9915 EndY=20.8898 EndZ=0
    g378: LineSegment StartX=45.9915 StartY=20.8898 StartZ=0 EndX=45.9915 EndY=20.959 EndZ=0
    g379: LineSegment StartX=45.9915 StartY=20.959 StartZ=0 EndX=46.0581 EndY=21.0202 EndZ=0
    g380: LineSegment StartX=46.0581 StartY=21.0202 StartZ=0 EndX=46.0527 EndY=21.0894 EndZ=0
    g381: LineSegment StartX=46.0527 StartY=21.0894 StartZ=0 EndX=46.2124 EndY=21.2464 EndZ=0
    g382: LineSegment StartX=46.2124 StartY=21.2464 StartZ=0 EndX=46.2763 EndY=21.2277 EndZ=0
    g383: LineSegment StartX=46.2763 StartY=21.2277 StartZ=0 EndX=46.5051 EndY=21.4486 EndZ=0
    g384: LineSegment StartX=46.5051 StartY=21.4486 StartZ=0 EndX=46.585 EndY=21.4539 EndZ=0
    g385: LineSegment StartX=46.585 StartY=21.4539 StartZ=0 EndX=46.6994 EndY=21.603 EndZ=0
    g386: LineSegment StartX=46.6994 StartY=21.603 StartZ=0 EndX=46.8245 EndY=21.5843 EndZ=0
    g387: LineSegment StartX=46.8245 StartY=21.5843 StartZ=0 EndX=46.9016 EndY=21.6855 EndZ=0
    g388: LineSegment StartX=46.9016 StartY=21.6855 StartZ=0 EndX=46.9655 EndY=21.6562 EndZ=0
    g389: LineSegment StartX=46.9655 StartY=21.6562 StartZ=0 EndX=47.205 EndY=21.8754 EndZ=0
    g390: LineSegment StartX=47.205 StartY=21.8754 StartZ=0 EndX=47.205 EndY=22.0711 EndZ=0
    g391: LineSegment StartX=47.205 StartY=22.0711 StartZ=0 EndX=47.2634 EndY=22.0711 EndZ=0
    g392: LineSegment StartX=47.2634 StartY=22.0711 StartZ=0 EndX=47.6208 EndY=22.4458 EndZ=0
    g393: LineSegment StartX=47.6208 StartY=22.4458 StartZ=0 EndX=47.6208 EndY=22.5177 EndZ=0
    g394: LineSegment StartX=47.6208 StartY=22.5177 StartZ=0 EndX=47.8212 EndY=22.7182 EndZ=0
    g395: LineSegment StartX=47.8212 StartY=22.7182 StartZ=0 EndX=47.8343 EndY=22.7944 EndZ=0
    g396: LineSegment StartX=47.8343 StartY=22.7944 StartZ=0 EndX=48.0478 EndY=22.997 EndZ=0
    g397: LineSegment StartX=48.0478 StartY=22.997 StartZ=0 EndX=48.0478 EndY=23.1365 EndZ=0
    g398: LineSegment StartX=48.0478 StartY=23.1365 StartZ=0 EndX=48.0998 EndY=23.2173 EndZ=0
    g399: LineSegment StartX=48.0998 StartY=23.2173 StartZ=0 EndX=48.0998 EndY=23.2802 EndZ=0
    ... +484 more geometry lines
  constraints (1492):
    c: Coincident(g3,g2)
    c: Vertical(g4)
    c: Vertical(g6)
    c: Coincident(g8,g7)
    c: Vertical(g8)
    c: Coincident(g8,g9)
    c: Coincident(g9,g10)
    c: Vertical(g10)
    c: Coincident(g10,g11)
    c: Coincident(g11,g12)
    c: Vertical(g12)
    c: Coincident(g13,g12)
    c: Horizontal(g13)
    c: Vertical(g14)
    c: Coincident(g16,g15)
    c: Vertical(g16)
    c: Horizontal(g17)
    c: Coincident(g18,g17)
    c: Vertical(g18)
    c: Horizontal(g19)
    c: Coincident(g20,g19)
    c: Vertical(g20)
    c: Horizontal(g21)
    c: Vertical(g22)
    c: Horizontal(g23)
    c: Coincident(g24,g23)
    c: Vertical(g24)
    c: Horizontal(g25)
    c: Coincident(g27,g26)
    c: Horizontal(g27)
    c: Vertical(g28)
    c: Coincident(g30,g29)
    c: Vertical(g30)
    c: Coincident(g31,g32)
    c: Vertical(g32)
    c: Coincident(g32,g33)
    c: Horizontal(g33)
    c: Coincident(g34,g33)
    c: Vertical(g34)
    c: Coincident(g35,g34)
    c: Horizontal(g35)
    c: Coincident(g36,g35)
    c: Vertical(g36)
    c: Coincident(g37,g36)
    c: Horizontal(g37)
    c: Vertical(g38)
    c: Horizontal(g39)
    c: Vertical(g40)
    c: Horizontal(g41)
    c: Coincident(g42,g41)
    c: Vertical(g42)
    c: Horizontal(g43)
    c: Coincident(g44,g43)
    c: Vertical(g44)
    c: Coincident(g45,g44)
    c: Horizontal(g45)
    c: Coincident(g46,g45)
    c: Vertical(g46)
    c: Coincident(g47,g46)
    c: Horizontal(g47)
    c: Coincident(g48,g47)
    c: Vertical(g48)
    c: Horizontal(g49)
    c: Vertical(g50)
    c: Coincident(g51,g50)
    c: Horizontal(g51)
    c: Vertical(g52)
    c: Coincident(g53,g52)
    c: Horizontal(g53)
    c: Coincident(g54,g53)
    c: Vertical(g54)
    c: Coincident(g55,g54)
    c: Horizontal(g55)
    c: Coincident(g56,g55)
    c: Vertical(g56)
    c: Coincident(g57,g56)
    c: Horizontal(g57)
    c: Coincident(g58,g57)
    c: Vertical(g58)
    c: Coincident(g60,g59)
    c: Vertical(g60)
    c: Coincident(g61,g60)
    c: Horizontal(g61)
    c: Vertical(g62)
    c: Horizontal(g63)
    c: Coincident(g64,g63)
    c: Vertical(g64)
    c: Horizontal(g65)
    c: Vertical(g66)
    c: Coincident(g68,g67)
    c: Vertical(g68)
    c: Horizontal(g69)
    c: Coincident(g70,g69)
    c: Vertical(g70)
    c: Horizontal(g71)
    c: Coincident(g72,g71)
    c: Vertical(g72)
    c: Horizontal(g73)
    c: Coincident(g74,g73)
    c: Vertical(g74)
    c: Horizontal(g75)
    c: Coincident(g76,g75)
    c: Vertical(g76)
    c: Horizontal(g77)
    c: Vertical(g78)
    c: Coincident(g79,g78)
    c: Coincident(g80,g79)
    c: Vertical(g80)
    c: Coincident(g81,g80)
    c: Coincident(g82,g81)
    c: Horizontal(g83)
    c: Coincident(g85,g84)
    c: Horizontal(g85)
    c: Coincident(g86,g85)
    c: Coincident(g89,g88)
    c: Horizontal(g89)
    c: Coincident(g90,g89)
    c: Coincident(g91,g90)
    c: Horizontal(g91)
    c: Coincident(g92,g91)
    c: Horizontal(g93)
    c: Coincident(g94,g93)
    c: Horizontal(g95)
    c: Coincident(g96,g95)
    c: Coincident(g97,g98)
    c: Coincident(g98,g99)
    c: Vertical(g99)
    c: Coincident(g99,g100)
    c: Coincident(g100,g101)
    c: Coincident(g101,g102)
    c: Coincident(g102,g103)
    c: Coincident(g103,g104)
    c: Coincident(g104,g105)
    c: Vertical(g105)
    c: Coincident(g105,g106)
    c: Coincident(g106,g107)
    c: Coincident(g107,g108)
    c: Horizontal(g108)
    c: Coincident(g108,g109)
    c: Coincident(g109,g110)
    c: Vertical(g110)
    c: Coincident(g110,g111)
    c: Coincident(g111,g112)
    c: Coincident(g112,g113)
    c: Coincident(g113,g114)
    c: Coincident(g114,g115)
    c: Coincident(g115,g116)
    c: Vertical(g116)
    c: Coincident(g116,g117)
    c: Coincident(g117,g118)
    c: Coincident(g118,g119)
    c: Coincident(g119,g120)
    c: Coincident(g120,g121)
    c: Horizontal(g121)
    c: Coincident(g121,g122)
    c: Coincident(g122,g123)
    c: Coincident(g123,g124)
    c: Coincident(g124,g125)
    c: Vertical(g125)
    c: Coincident(g125,g126)
    c: Coincident(g126,g127)
    c: Horizontal(g127)
    c: Coincident(g127,g128)
    c: Vertical(g128)
    c: Coincident(g128,g129)
    c: Coincident(g129,g130)
    c: Vertical(g130)
    c: Coincident(g130,g131)
    c: Horizontal(g131)
    c: Coincident(g131,g132)
    c: Vertical(g132)
    c: Coincident(g132,g133)
    c: Coincident(g133,g134)
    c: Coincident(g134,g135)
    c: Coincident(g135,g136)
    c: Coincident(g136,g137)
    c: Coincident(g137,g138)
    c: Vertical(g138)
    c: Coincident(g138,g139)
    c: Coincident(g139,g140)
    c: Vertical(g140)
    c: Coincident(g140,g141)
    c: Horizontal(g141)
    c: Coincident(g141,g142)
    c: Coincident(g142,g143)
    c: Coincident(g143,g144)
    c: Coincident(g144,g145)
    c: Coincident(g145,g146)
    c: Vertical(g146)
    c: Coincident(g146,g147)
    c: Coincident(g147,g148)
    c: Vertical(g148)
    c: Coincident(g148,g149)
    c: Horizontal(g149)
    c: Coincident(g149,g150)
    c: Vertical(g150)
    c: Coincident(g150,g151)
    c: Horizontal(g151)
    c: Coincident(g151,g152)
    c: Vertical(g152)
    c: Coincident(g152,g153)
    c: Horizontal(g153)
    c: Coincident(g153,g154)
    c: Vertical(g154)
    c: Coincident(g154,g155)
    c: Horizontal(g155)
    c: Coincident(g155,g156)
    c: Vertical(g156)
    c: Coincident(g156,g157)
    c: Horizontal(g157)
    c: Coincident(g157,g158)
    c: Vertical(g158)
    c: Coincident(g158,g159)
    c: Coincident(g159,g160)
    c: Coincident(g160,g161)
    c: Horizontal(g161)
    c: Coincident(g161,g162)
    c: Vertical(g162)
    c: Coincident(g162,g163)
    c: Horizontal(g163)
    c: Coincident(g163,g164)
    c: Coincident(g164,g165)
    c: Horizontal(g165)
    c: Coincident(g165,g166)
    c: Vertical(g166)
    c: Coincident(g166,g167)
    c: Horizontal(g167)
    c: Coincident(g167,g168)
    c: Coincident(g168,g169)
    c: Coincident(g169,g170)
    c: Vertical(g170)
    c: Coincident(g170,g171)
    c: Coincident(g171,g172)
    c: Vertical(g172)
    c: Coincident(g172,g173)
    c: Horizontal(g173)
    c: Coincident(g173,g174)
    c: Vertical(g174)
    c: Coincident(g174,g175)
    c: Horizontal(g175)
    c: Coincident(g175,g176)
    c: Vertical(g176)
    c: Coincident(g176,g177)
    c: Coincident(g177,g178)
    c: Vertical(g178)
    c: Coincident(g178,g179)
    c: Horizontal(g179)
    c: Coincident(g179,g180)
    c: Vertical(g180)
    c: Coincident(g180,g181)
    c: Horizontal(g181)
    c: Coincident(g181,g182)
    c: Vertical(g182)
    c: Coincident(g182,g183)
    c: Horizontal(g183)
    c: Coincident(g183,g184)
    c: Vertical(g184)
    c: Coincident(g184,g185)
    c: Horizontal(g185)
    c: Coincident(g185,g186)
    c: Coincident(g186,g187)
    c: Coincident(g187,g188)
    c: Coincident(g188,g189)
    c: Vertical(g189)
    c: Coincident(g189,g190)
    c: Coincident(g190,g191)
    c: Coincident(g191,g192)
    c: Coincident(g192,g193)
    c: Coincident(g193,g194)
    c: Coincident(g194,g195)
    c: Vertical(g195)
    c: Coincident(g195,g196)
    c: Coincident(g196,g197)
    c: Vertical(g197)
    c: Coincident(g197,g198)
    c: Coincident(g198,g199)
    c: Vertical(g199)
    c: Coincident(g199,g200)
    c: Coincident(g200,g201)
    c: Vertical(g201)
    c: Coincident(g201,g202)
    c: Coincident(g202,g203)
    c: Vertical(g203)
    c: Coincident(g203,g204)
    c: Coincident(g204,g205)
    c: Vertical(g205)
    c: Coincident(g205,g206)
    c: Coincident(g206,g207)
    c: Coincident(g207,g208)
    c: Coincident(g208,g209)
    c: Vertical(g209)
    c: Coincident(g209,g210)
    c: Coincident(g210,g211)
    c: Coincident(g211,g212)
    c: Coincident(g212,g213)
    c: Coincident(g213,g214)
    c: Coincident(g214,g215)
    c: Vertical(g215)
    c: Coincident(g215,g216)
    c: Coincident(g216,g217)
    c: Horizontal(g217)
    c: Coincident(g217,g218)
    c: Vertical(g218)
    c: Coincident(g218,g219)
    c: Horizontal(g219)
    c: Coincident(g219,g220)
    c: Coincident(g220,g221)
    c: Horizontal(g221)
    c: Coincident(g221,g222)
    c: Coincident(g222,g223)
    c: Horizontal(g223)
    c: Coincident(g223,g224)
    c: Coincident(g224,g225)
    c: Horizontal(g225)
    c: Coincident(g225,g226)
    c: Vertical(g226)
    c: Coincident(g226,g227)
    c: Horizontal(g227)
    c: Coincident(g227,g228)
    c: Vertical(g228)
    c: Coincident(g228,g229)
    c: Horizontal(g229)
    c: Coincident(g229,g230)
    c: Coincident(g230,g231)
    c: Coincident(g231,g232)
    c: Coincident(g232,g233)
    c: Horizontal(g233)
    c: Coincident(g233,g234)
    c: Coincident(g234,g235)
    c: Horizontal(g235)
    c: Coincident(g235,g236)
    c: Coincident(g236,g237)
    c: Horizontal(g237)
    c: Coincident(g237,g238)
    c: Coincident(g238,g239)
    c: Horizontal(g239)
    c: Coincident(g239,g240)
    c: Coincident(g240,g241)
    c: Vertical(g241)
    c: Coincident(g241,g242)
    c: Horizontal(g242)
    c: Coincident(g242,g243)
    c: Vertical(g243)
    c: Coincident(g243,g244)
    c: Coincident(g244,g245)
    c: Vertical(g245)
    c: Coincident(g245,g246)
    c: Horizontal(g246)
    c: Coincident(g246,g247)
    c: Coincident(g247,g248)
    c: Horizontal(g248)
    c: Coincident(g248,g249)
    c: Vertical(g249)
    c: Coincident(g249,g250)
    c: Coincident(g250,g251)
    c: Coincident(g251,g252)
    c: Horizontal(g252)
    c: Coincident(g252,g253)
    c: Coincident(g253,g254)
    c: Horizontal(g254)
    c: Coincident(g254,g255)
    c: Vertical(g255)
    c: Coincident(g255,g256)
    c: Coincident(g256,g257)
    c: Coincident(g257,g258)
    c: Coincident(g258,g259)
    c: Coincident(g259,g260)
    c: Coincident(g260,g261)
    c: Vertical(g257)
    c: Horizontal(g258)
    c: Horizontal(g256)
    c: Vertical(g259)
    c: Horizontal(g260)
    c: Vertical(g261)
    c: Coincident(g261,g262)
    c: Horizontal(g262)
    c: Coincident(g262,g263)
    c: Vertical(g263)
    c: Coincident(g263,g264)
    c: Coincident(g264,g265)
    c: Coincident(g265,g266)
    c: Coincident(g266,g267)
    c: Coincident(g267,g268)
    c: Coincident(g268,g269)
    c: Vertical(g269)
    c: Coincident(g269,g270)
    c: Horizontal(g270)
    c: Coincident(g270,g271)
    c: Vertical(g271)
    c: Coincident(g271,g272)
    c: Coincident(g272,g273)
    c: Vertical(g273)
    c: Coincident(g273,g274)
    c: Horizontal(g274)
    c: Coincident(g274,g275)
    c: Vertical(g275)
    c: Coincident(g275,g276)
    c: Horizontal(g276)
    c: Coincident(g276,g277)
    c: Coincident(g277,g278)
    c: Horizontal(g278)
    c: Coincident(g278,g279)
    c: Coincident(g279,g280)
    c: Coincident(g280,g281)
    c: Vertical(g281)
    c: Coincident(g281,g282)
    c: Coincident(g282,g283)
    c: Coincident(g283,g284)
    c: Horizontal(g284)
    c: Coincident(g284,g285)
    c: Coincident(g285,g286)
    c: Coincident(g286,g287)
    c: Coincident(g287,g288)
    c: Coincident(g288,g289)
    c: Coincident(g289,g290)
    c: Coincident(g290,g291)
    c: Vertical(g291)
    c: Coincident(g291,g292)
    c: Horizontal(g292)
    c: Coincident(g292,g293)
    c: Coincident(g293,g294)
    c: Horizontal(g294)
    c: Coincident(g294,g295)
    c: Vertical(g295)
    c: Coincident(g295,g296)
    c: Coincident(g296,g297)
    c: Vertical(g297)
    c: Coincident(g297,g298)
    c: Horizontal(g298)
    c: Coincident(g298,g299)
    c: Vertical(g299)
    c: Coincident(g299,g300)
    c: Horizontal(g300)
    c: Coincident(g300,g301)
    c: Coincident(g301,g302)
    c: Coincident(g302,g303)
    c: Coincident(g303,g304)
    c: Coincident(g304,g305)
    c: Coincident(g305,g306)
    c: Coincident(g306,g307)
    c: Coincident(g307,g308)
    c: Horizontal(g308)
    c: Coincident(g308,g309)
    c: Coincident(g309,g310)
    c: Horizontal(g310)
    c: Coincident(g310,g311)
    c: Coincident(g311,g312)
    c: Coincident(g312,g313)
    c: Coincident(g313,g314)
    c: Coincident(g314,g315)
    c: Coincident(g315,g316)
    c: Coincident(g316,g317)
    c: Coincident(g317,g318)
    c: Coincident(g318,g319)
    c: Coincident(g319,g320)
    c: Coincident(g320,g321)
    c: Coincident(g321,g322)
    c: Coincident(g322,g323)
    c: Coincident(g323,g324)
    c: Horizontal(g324)
    c: Coincident(g324,g325)
    c: Coincident(g325,g326)
    c: Coincident(g326,g327)
    c: Vertical(g327)
    c: Coincident(g327,g328)
    c: Coincident(g328,g329)
    c: Coincident(g329,g330)
    c: Coincident(g330,g331)
    c: Vertical(g331)
    c: Coincident(g331,g332)
    c: Coincident(g332,g333)
    c: Coincident(g333,g334)
    c: Coincident(g334,g335)
    c: Coincident(g335,g336)
    c: Coincident(g336,g337)
    c: Vertical(g337)
    c: Coincident(g337,g338)
    c: Coincident(g338,g339)
    c: Coincident(g339,g340)
    c: Coincident(g340,g341)
    c: Coincident(g341,g342)
    c: Coincident(g342,g343)
    c: Coincident(g343,g344)
    c: Coincident(g344,g345)
    c: Coincident(g345,g346)
    c: Coincident(g346,g347)
    c: Coincident(g347,g348)
    c: Coincident(g348,g349)
    c: Coincident(g349,g350)
    c: Coincident(g350,g351)
    c: Coincident(g351,g352)
    c: Coincident(g352,g353)
    c: Coincident(g353,g354)
    c: Coincident(g354,g355)
    c: Coincident(g355,g356)
    c: Coincident(g356,g357)
    c: Vertical(g357)
    c: Coincident(g357,g358)
    c: Horizontal(g358)
    c: Coincident(g358,g359)
    c: Coincident(g359,g360)
    c: Coincident(g360,g361)
    c: Coincident(g361,g362)
    c: Horizontal(g362)
    c: Coincident(g362,g363)
    c: Coincident(g363,g364)
    c: Coincident(g364,g365)
    c: Coincident(g365,g366)
    c: Coincident(g366,g367)
    c: Horizontal(g290)
    c: Vertical(g287)
    c: Vertical(g285)
    c: Vertical(g283)
    c: Vertical(g279)
    c: Vertical(g277)
    c: Horizontal(g286)
    c: Horizontal(g288)
    c: Vertical(g289)
    c: Horizontal(g280)
    c: Horizontal(g282)
    c: Vertical(g329)
    c: Horizontal(g330)
    c: Horizontal(g340)
    c: Horizontal(g342)
    c: Horizontal(g344)
    c: Horizontal(g346)
    c: Horizontal(g348)
    c: Horizontal(g350)
    c: Vertical(g339)
    c: Vertical(g341)
    c: Vertical(g343)
    c: Vertical(g345)
    c: Vertical(g347)
    c: Vertical(g349)
    c: Vertical(g351)
    c: Vertical(g353)
    c: Vertical(g355)
    c: Horizontal(g352)
    c: Horizontal(g354)
    c: Horizontal(g356)
    c: Vertical(g359)
    c: Horizontal(g360)
    c: Horizontal(g364)
    c: Vertical(g365)
    c: Horizontal(g366)
    c: Coincident(g368,g367)
    c: Coincident(g369,g368)
    c: Coincident(g369,g370)
    c: Coincident(g370,g371)
    c: Coincident(g371,g372)
    c: Horizontal(g372)
    c: Coincident(g372,g373)
    c: Coincident(g373,g374)
    c: Coincident(g374,g375)
    c: Coincident(g375,g376)
    c: Coincident(g376,g377)
    c: Coincident(g377,g378)
    c: Vertical(g378)
    c: Coincident(g378,g379)
    c: Coincident(g379,g380)
    c: Coincident(g380,g381)
    c: Coincident(g381,g382)
    c: Coincident(g382,g383)
    c: Coincident(g383,g384)
    c: Coincident(g384,g385)
    c: Coincident(g385,g386)
    c: Coincident(g386,g387)
    c: Coincident(g387,g388)
    c: Coincident(g388,g389)
    c: Coincident(g389,g390)
    c: Coincident(g390,g391)
    c: Horizontal(g391)
    c: Coincident(g391,g392)
    c: Coincident(g392,g393)
    c: Coincident(g393,g394)
    c: Coincident(g394,g395)
    c: Coincident(g395,g396)
    c: Coincident(g396,g397)
    c: Coincident(g397,g398)
    c: Coincident(g398,g399)
    c: Coincident(g399,g400)
    c: Coincident(g400,g401)
    c: Coincident(g401,g402)
    c: Coincident(g402,g403)
    c: Coincident(g403,g404)
    c: Coincident(g404,g405)
    c: Coincident(g405,g406)
    c: Coincident(g406,g407)
    c: Coincident(g407,g408)
    c: Coincident(g408,g409)
    c: Vertical(g409)
    c: Coincident(g409,g410)
    c: Coincident(g410,g411)
    c: Vertical(g411)
    c: Coincident(g411,g412)
    c: Horizontal(g412)
    c: Coincident(g412,g413)
    c: Coincident(g413,g414)
    c: Horizontal(g414)
    c: Coincident(g414,g415)
    c: Coincident(g415,g416)
    c: Coincident(g416,g417)
    c: Coincident(g417,g418)
    c: Coincident(g418,g419)
    c: Coincident(g419,g420)
    c: Coincident(g420,g421)
    c: Coincident(g421,g422)
    c: Coincident(g422,g423)
    c: Coincident(g423,g424)
    c: Coincident(g424,g425)
    c: Coincident(g425,g426)
    c: Horizontal(g426)
    c: Coincident(g426,g427)
    c: Coincident(g427,g428)
    c: Horizontal(g428)
    c: Coincident(g428,g429)
    c: Coincident(g429,g430)
    c: Coincident(g430,g431)
    c: Coincident(g431,g432)
    c: Horizontal(g432)
    c: Coincident(g432,g433)
    c: Coincident(g433,g434)
    c: Horizontal(g434)
    c: Coincident(g434,g435)
    c: Coincident(g435,g436)
    c: Coincident(g436,g437)
    c: Coincident(g437,g438)
    c: Coincident(g439,g440)
    c: Coincident(g440,g441)
    c: Coincident(g441,g442)
    c: Coincident(g442,g443)
    c: Coincident(g443,g444)
    c: Coincident(g444,g445)
    c: Coincident(g445,g446)
    c: Coincident(g446,g447)
    c: Coincident(g447,g448)
    c: Coincident(g448,g449)
    c: Coincident(g449,g450)
    c: Coincident(g450,g451)
    c: Coincident(g451,g452)
    c: Coincident(g452,g453)
    c: Coincident(g453,g454)
    c: Coincident(g454,g455)
    c: Coincident(g455,g456)
    c: Coincident(g456,g457)
    c: Coincident(g457,g458)
    c: Coincident(g458,g459)
    c: Coincident(g459,g460)
    c: Coincident(g460,g461)
    c: Coincident(g461,g462)
    c: Coincident(g462,g463)
    c: Coincident(g463,g464)
    c: Coincident(g464,g465)
    c: Coincident(g465,g466)
    c: Coincident(g466,g467)
    c: Coincident(g467,g468)
    c: Coincident(g468,g469)
    c: Coincident(g469,g470)
    c: Coincident(g470,g471)
    c: Coincident(g471,g472)
    c: Horizontal(g472)
    c: Coincident(g472,g473)
    c: Coincident(g473,g474)
    c: Coincident(g474,g475)
    c: Coincident(g475,g476)
    c: Coincident(g476,g477)
    c: Coincident(g477,g478)
    c: Coincident(g478,g479)
    c: Coincident(g479,g480)
    c: Coincident(g480,g481)
    c: Coincident(g481,g482)
    c: Coincident(g482,g483)
    c: Coincident(g483,g484)
    c: Coincident(g484,g485)
    c: Coincident(g485,g486)
    c: Coincident(g486,g487)
    c: Coincident(g487,g488)
    c: Vertical(g488)
    c: Coincident(g488,g489)
    c: Coincident(g489,g490)
    c: Vertical(g490)
    c: Coincident(g490,g491)
    c: Coincident(g491,g492)
    c: Coincident(g492,g493)
    c: Coincident(g493,g494)
    c: Coincident(g494,g495)
    c: Coincident(g495,g496)
    c: Coincident(g496,g497)
    c: Coincident(g497,g498)
    c: Coincident(g498,g499)
    c: Coincident(g499,g500)
    c: Coincident(g500,g501)
    c: Coincident(g501,g502)
    c: Coincident(g502,g503)
    c: Coincident(g503,g504)
    c: Horizontal(g370)
    c: Horizontal(g374)
    c: Horizontal(g376)
    c: Vertical(g390)
    c: Vertical(g397)
    c: Vertical(g399)
    c: Vertical(g401)
    c: Vertical(g403)
    c: Vertical(g407)
    c: Horizontal(g410)
    c: Vertical(g413)
    c: Vertical(g415)
    c: Horizontal(g416)
    c: Vertical(g417)
    c: Horizontal(g418)
    c: Vertical(g419)
    c: Vertical(g421)
    c: Vertical(g423)
    c: Vertical(g425)
    c: Vertical(g427)
    c: Vertical(g429)
    c: Horizontal(g420)
    c: Horizontal(g422)
    c: Horizontal(g424)
    c: Vertical(g431)
    c: Vertical(g433)
    c: Vertical(g435)
    c: Horizontal(g436)
    c: Horizontal(g438)
    c: Vertical(g437)
    c: Coincident(g439,g505)
    c: Horizontal(g505)
    c: Coincident(g505,g506)
    c: Coincident(g506,g438)
    c: Vertical(g506)
    c: Horizontal(g464)
    c: Horizontal(g462)
    c: Horizontal(g460)
    c: Horizontal(g458)
    c: Horizontal(g456)
    c: Horizontal(g454)
    c: Horizontal(g452)
    c: Horizontal(g450)
    c: Horizontal(g448)
    c: Horizontal(g446)
    c: Horizontal(g444)
    c: Horizontal(g442)
    c: Horizontal(g440)
    c: Horizontal(g468)
    c: Horizontal(g470)
    c: Horizontal(g474)
    c: Horizontal(g476)
    c: Horizontal(g478)
    c: Vertical(g465)
    c: Horizontal(g466)
    c: Vertical(g475)
    c: Vertical(g477)
    c: Horizontal(g491)
    c: Horizontal(g496)
    c: Horizontal(g494)
    c: Horizontal(g498)
    c: Vertical(g499)
    c: Vertical(g497)
    c: Vertical(g495)
    c: Vertical(g493)
    c: Horizontal(g500)
    c: Horizontal(g502)
    c: Horizontal(g504)
    c: Vertical(g501)
    c: Vertical(g503)
    c: Coincident(g504,g507)
    c: Vertical(g507)
    c: Coincident(g507,g508)
    c: Coincident(g508,g509)
    c: Coincident(g509,g510)
    c: Coincident(g510,g511)
    c: Vertical(g511)
    c: Coincident(g511,g512)
    c: Horizontal(g512)
    c: Coincident(g512,g513)
    c: Vertical(g513)
    c: Coincident(g513,g514)
    c: Coincident(g514,g515)
    c: Vertical(g515)
    c: Coincident(g515,g516)
    c: Horizontal(g516)
    c: Coincident(g516,g517)
    c: Coincident(g517,g518)
    c: Horizontal(g518)
    c: Coincident(g518,g519)
    c: Coincident(g519,g520)
    c: Coincident(g521,g522)
    c: Coincident(g522,g523)
    c: Coincident(g523,g524)
    c: Coincident(g524,g525)
    c: Coincident(g525,g526)
    c: Coincident(g526,g527)
    c: Coincident(g527,g528)
    c: Coincident(g528,g529)
    c: Coincident(g529,g530)
    c: Coincident(g531,g532)
    c: Coincident(g532,g533)
    c: Coincident(g533,g534)
    c: Coincident(g534,g535)
    c: Coincident(g535,g536)
    c: Coincident(g536,g537)
    c: Coincident(g537,g538)
    c: Coincident(g538,g539)
    c: Coincident(g539,g540)
    c: Coincident(g540,g541)
    c: Coincident(g541,g542)
    c: Coincident(g542,g543)
    c: Coincident(g543,g544)
    c: Coincident(g544,g545)
    c: Coincident(g545,g546)
    c: Coincident(g546,g547)
    c: Coincident(g547,g548)
    c: Coincident(g548,g549)
    c: Coincident(g549,g550)
    c: Horizontal(g550)
    c: Coincident(g550,g551)
    c: Coincident(g551,g552)
    c: Coincident(g552,g553)
    c: Coincident(g553,g554)
    c: Horizontal(g554)
    c: Coincident(g554,g555)
    c: Coincident(g555,g556)
    c: Coincident(g556,g557)
    c: Coincident(g557,g558)
    c: Horizontal(g558)
    c: Coincident(g558,g559)
    c: Coincident(g559,g560)
    c: Coincident(g560,g561)
    c: Coincident(g562,g563)
    c: Horizontal(g563)
    c: Coincident(g563,g564)
    c: Coincident(g564,g565)
    c: Coincident(g565,g566)
    c: Coincident(g566,g567)
    c: Horizontal(g567)
    c: Coincident(g567,g568)
    c: Coincident(g568,g569)
    c: Coincident(g569,g570)
    c: Coincident(g570,g571)
    c: Coincident(g571,g572)
    c: Coincident(g572,g573)
    c: Coincident(g573,g574)
    c: Coincident(g574,g575)
    c: Coincident(g575,g576)
    c: Coincident(g576,g577)
    c: Coincident(g577,g578)
    c: Coincident(g578,g579)
    c: Coincident(g579,g580)
    c: Vertical(g580)
    c: Coincident(g580,g581)
    c: Coincident(g581,g582)
    c: Coincident(g582,g583)
    c: Coincident(g583,g584)
    c: Coincident(g584,g585)
    c: Horizontal(g585)
    c: Coincident(g585,g586)
    c: Coincident(g586,g587)
    c: Coincident(g587,g588)
    c: Vertical(g588)
    c: Coincident(g588,g589)
    c: Coincident(g589,g590)
    c: Coincident(g590,g591)
    c: Coincident(g592,g593)
    c: Horizontal(g593)
    c: Coincident(g593,g594)
    c: Coincident(g594,g595)
    c: Coincident(g595,g596)
    c: Vertical(g596)
    c: Coincident(g596,g597)
    c: Horizontal(g597)
    c: Coincident(g597,g598)
    c: Vertical(g598)
    c: Coincident(g598,g599)
    c: Coincident(g599,g600)
    c: Coincident(g600,g601)
    c: Horizontal(g601)
    c: Coincident(g601,g602)
    c: Coincident(g602,g603)
    c: Coincident(g603,g604)
    c: Coincident(g604,g605)
    c: Coincident(g605,g606)
    c: Coincident(g606,g607)
    c: Coincident(g607,g608)
    c: Coincident(g608,g609)
    c: Horizontal(g609)
    c: Coincident(g609,g610)
    c: Coincident(g610,g611)
    c: Coincident(g611,g612)
    c: Coincident(g612,g613)
    c: Vertical(g613)
    c: Coincident(g613,g614)
    c: Coincident(g614,g615)
    c: Vertical(g615)
    c: Coincident(g615,g616)
    c: Coincident(g616,g617)
    c: Vertical(g617)
    c: Coincident(g618,g619)
    c: Vertical(g619)
    c: Coincident(g619,g620)
    c: Coincident(g620,g621)
    c: Coincident(g621,g622)
    c: Coincident(g622,g623)
    c: Coincident(g623,g624)
    c: Coincident(g624,g625)
    c: Coincident(g625,g626)
    c: Coincident(g626,g627)
    c: Vertical(g627)
    c: Coincident(g627,g628)
    c: Coincident(g628,g629)
    c: Coincident(g629,g630)
    c: Coincident(g630,g631)
    c: Coincident(g631,g632)
    c: Coincident(g632,g633)
    c: Vertical(g633)
    c: Coincident(g633,g634)
    c: Coincident(g634,g635)
    c: Vertical(g635)
    c: Coincident(g635,g636)
    c: Coincident(g636,g637)
    c: Coincident(g637,g638)
    c: Coincident(g638,g639)
    c: Coincident(g639,g640)
    c: Horizontal(g640)
    c: Coincident(g640,g641)
    c: Coincident(g641,g642)
    c: Vertical(g642)
    c: Coincident(g642,g643)
    c: Coincident(g643,g644)
    c: Vertical(g644)
    c: Coincident(g644,g645)
    c: Coincident(g645,g646)
    c: Coincident(g646,g647)
    c: Coincident(g647,g648)
    c: Coincident(g648,g649)
    c: Coincident(g649,g650)
    c: Coincident(g650,g651)
    c: Coincident(g651,g652)
    c: Vertical(g652)
    c: Coincident(g652,g653)
    c: Coincident(g653,g654)
    c: Coincident(g654,g655)
    c: Coincident(g655,g656)
    c: Coincident(g656,g657)
    c: Coincident(g657,g658)
    c: Vertical(g658)
    c: Coincident(g658,g659)
    c: Coincident(g659,g660)
    c: Vertical(g660)
    c: Coincident(g660,g661)
    c: Coincident(g661,g662)
    c: Coincident(g662,g663)
    c: Coincident(g663,g664)
    c: Coincident(g664,g665)
    c: Coincident(g665,g666)
    c: Coincident(g666,g667)
    c: Coincident(g667,g668)
    c: Coincident(g668,g669)
    c: Coincident(g669,g670)
    c: Coincident(g670,g671)
    c: Coincident(g671,g672)
    c: Coincident(g672,g673)
    c: Horizontal(g673)
    c: Coincident(g673,g674)
    c: Coincident(g674,g675)
    c: Coincident(g675,g676)
    c: Coincident(g676,g677)
    c: Coincident(g677,g678)
    c: Vertical(g678)
    c: Coincident(g678,g679)
    c: Coincident(g680,g681)
    c: Vertical(g681)
    c: Coincident(g681,g682)
    c: Horizontal(g682)
    c: Coincident(g682,g683)
    c: Coincident(g683,g684)
    c: Coincident(g684,g685)
    c: Coincident(g685,g686)
    c: Coincident(g686,g687)
    c: Vertical(g687)
    c: Coincident(g687,g688)
    c: Coincident(g688,g689)
    c: Coincident(g689,g690)
    c: Coincident(g690,g691)
    c: Coincident(g691,g692)
    c: Coincident(g692,g693)
    c: Coincident(g693,g694)
    c: Horizontal(g694)
    c: Coincident(g694,g695)
    c: Horizontal(g508)
    c: Vertical(g509)
    c: Horizontal(g510)
    c: Vertical(g519)
    c: Vertical(g517)
    c: Horizontal(g520)
    c: Coincident(g520,g696)
    c: Coincident(g696,g697)
    c: Horizontal(g697)
    c: Coincident(g697,g698)
    c: Coincident(g698,g521)
    c: Vertical(g698)
    c: Vertical(g522)
    c: Vertical(g524)
    c: Vertical(g526)
    c: Horizontal(g523)
    c: Horizontal(g525)
    c: Horizontal(g527)
    c: Horizontal(g529)
    c: Horizontal(g532)
    c: Horizontal(g521)
    c: Vertical(g528)
    c: Vertical(g530)
    c: Coincident(g530,g699)
    c: Coincident(g699,g700)
    c: Coincident(g700,g701)
    c: Coincident(g701,g531)
    c: Vertical(g700)
    c: Vertical(g531)
    c: Vertical(g533)
    c: Vertical(g535)
    c: Vertical(g537)
    c: Vertical(g539)
    c: Vertical(g541)
    c: Horizontal(g534)
    c: Horizontal(g536)
    c: Horizontal(g538)
    c: Horizontal(g540)
    c: Horizontal(g542)
    c: Horizontal(g544)
    c: Horizontal(g546)
    c: Horizontal(g699)
    c: Horizontal(g701)
    c: Vertical(g543)
    c: Vertical(g545)
    c: Vertical(g547)
    c: Vertical(g549)
    c: Horizontal(g548)
    c: Vertical(g555)
    c: Vertical(g553)
    c: Vertical(g551)
    c: Horizontal(g552)
    c: Horizontal(g556)
    c: Horizontal(g560)
    c: Vertical(g557)
    c: Vertical(g559)
    c: Vertical(g561)
    c: Coincident(g702,g562)
    c: Coincident(g702,g561)
    c: Horizontal(g565)
    c: Horizontal(g569)
    c: Horizontal(g571)
    c: Horizontal(g573)
    c: Horizontal(g575)
    c: Horizontal(g702)
    c: Vertical(g566)
    c: Vertical(g568)
    c: Vertical(g570)
    c: Vertical(g572)
    c: Vertical(g574)
    c: Vertical(g576)
    c: Vertical(g578)
    c: Vertical(g582)
    c: Vertical(g584)
    c: Horizontal(g577)
    c: Horizontal(g579)
    c: Horizontal(g581)
    c: Horizontal(g583)
    c: Horizontal(g587)
    c: Horizontal(g589)
    c: Horizontal(g591)
    c: Coincident(g591,g592)
    c: Vertical(g590)
    c: Vertical(g592)
    c: Vertical(g594)
    c: Vertical(g602)
    c: Vertical(g604)
    c: Horizontal(g595)
    c: Horizontal(g599)
    c: Horizontal(g605)
    c: Horizontal(g607)
    c: Vertical(g608)
    c: Vertical(g611)
    c: Horizontal(g612)
    c: Horizontal(g614)
    c: Horizontal(g620)
    c: Horizontal(g622)
    c: Vertical(g621)
    c: Vertical(g623)
    c: Coincident(g618,g703)
    c: Vertical(g703)
    c: Coincident(g703,g704)
    c: Horizontal(g704)
    c: Coincident(g704,g617)
    c: Horizontal(g624)
    c: Vertical(g625)
    c: Horizontal(g643)
    c: Horizontal(g645)
    c: Horizontal(g647)
    c: Horizontal(g649)
    c: Horizontal(g651)
    c: Horizontal(g653)
    c: Horizontal(g655)
    c: Horizontal(g657)
    c: Horizontal(g659)
    c: Vertical(g656)
    c: Vertical(g654)
    c: Vertical(g650)
    c: Vertical(g648)
    c: Vertical(g646)
    c: Vertical(g637)
    c: Vertical(g639)
    c: Horizontal(g661)
    c: Horizontal(g663)
    c: Horizontal(g665)
    c: Horizontal(g667)
    c: Horizontal(g669)
    c: Horizontal(g671)
    c: Horizontal(g675)
    c: Vertical(g662)
    c: Vertical(g664)
    c: Vertical(g666)
    c: Vertical(g668)
    c: Vertical(g670)
    c: Vertical(g672)
    c: Vertical(g674)
    c: Vertical(g676)
    c: Horizontal(g677)
    c: Horizontal(g679)
    c: Coincident(g679,g705)
    c: Vertical(g705)
    c: Coincident(g705,g706)
    c: Horizontal(g706)
    c: Coincident(g706,g707)
    c: Coincident(g680,g707)
    c: Horizontal(g680)
    c: Vertical(g707)
    c: Vertical(g691)
    c: Vertical(g693)
    c: Vertical(g689)
    c: Vertical(g685)
    c: Vertical(g683)
    c: Horizontal(g686)
    c: Horizontal(g688)
    c: Horizontal(g690)
    c: Horizontal(g692)
    c: Horizontal(g684)
    c: Vertical(g695)
    c: Coincident(g695,g708)
    c: Coincident(g708,g709)
    c: Coincident(g709,g710)
    c: Coincident(g710,g711)
    c: Coincident(g711,g712)
    c: Coincident(g712,g713)
    c: Horizontal(g713)
    c: Coincident(g713,g714)
    c: Coincident(g714,g715)
    c: Coincident(g715,g716)
    c: Coincident(g716,g717)
    c: Coincident(g718,g719)
    c: Horizontal(g720)
    c: Coincident(g721,g722)
    c: Coincident(g722,g723)
    c: Coincident(g723,g724)
    c: Horizontal(g724)
    c: Coincident(g724,g725)
    c: Horizontal(g726)
    c: Coincident(g726,g727)
    c: Coincident(g727,g728)
    c: Horizontal(g728)
    c: Coincident(g728,g729)
    c: Coincident(g729,g730)
    c: Coincident(g730,g731)
    c: Coincident(g731,g732)
    c: Coincident(g732,g733)
    c: Coincident(g733,g734)
    c: Coincident(g734,g735)
    c: Coincident(g735,g736)
    c: Coincident(g736,g737)
    c: Coincident(g737,g738)
    c: Coincident(g738,g739)
    c: Coincident(g739,g740)
    c: Coincident(g740,g741)
    c: Coincident(g741,g742)
    c: Coincident(g742,g743)
    c: Coincident(g743,g744)
    c: Coincident(g744,g745)
    c: Coincident(g745,g746)
    c: Coincident(g746,g747)
    c: Coincident(g747,g748)
    c: Coincident(g748,g749)
    c: Coincident(g749,g750)
    c: Coincident(g750,g751)
    c: Coincident(g751,g752)
    c: Coincident(g752,g753)
    c: Coincident(g753,g754)
    c: Coincident(g754,g755)
    c: Coincident(g755,g756)
    c: Coincident(g756,g757)
    c: Coincident(g757,g758)
    c: Coincident(g760,g761)
    c: Coincident(g761,g762)
    c: Coincident(g762,g763)
    c: Coincident(g763,g764)
    c: Coincident(g765,g766)
    c: Coincident(g766,g767)
    c: Coincident(g767,g768)
    c: Coincident(g769,g770)
    c: Coincident(g770,g771)
    c: Coincident(g772,g773)
    c: Coincident(g773,g774)
    c: Coincident(g774,g775)
    c: Coincident(g775,g776)
    c: Coincident(g776,g777)
    c: Coincident(g777,g778)
    c: Coincident(g778,g779)
    c: Coincident(g779,g780)
    c: Coincident(g780,g781)
    c: Coincident(g781,g782)
    c: Coincident(g782,g783)
    c: Coincident(g783,g784)
    c: Coincident(g784,g785)
    c: Coincident(g785,g786)
    c: Horizontal(g787)
    c: Coincident(g787,g788)
    c: Coincident(g788,g789)
    c: Coincident(g789,g790)
    c: Coincident(g790,g791)
    c: Horizontal(g791)
    c: Coincident(g791,g792)
    c: Coincident(g792,g793)
    c: Horizontal(g793)
    c: Coincident(g793,g794)
    c: Coincident(g794,g795)
    c: Coincident(g795,g796)
    c: Vertical(g796)
    c: Coincident(g796,g797)
    c: Horizontal(g797)
    c: Coincident(g797,g798)
    c: Coincident(g798,g799)
    c: Horizontal(g799)
    c: Coincident(g799,g800)
    c: Coincident(g800,g801)
    c: Coincident(g801,g802)
    c: Coincident(g802,g803)
    c: Horizontal(g803)
    c: Vertical(g804)
    c: Coincident(g804,g805)
    c: Coincident(g805,g806)
    c: Coincident(g806,g807)
    c: Coincident(g807,g808)
    c: Coincident(g808,g809)
    c: Coincident(g809,g810)
    c: Vertical(g810)
    c: Coincident(g810,g811)
    c: Coincident(g811,g812)
    c: Coincident(g812,g813)
    c: Coincident(g813,g814)
    c: Coincident(g814,g815)
    c: Horizontal(g815)
    c: Coincident(g815,g816)
    c: Coincident(g816,g817)
    c: Coincident(g817,g818)
    c: Coincident(g818,g819)
    c: Coincident(g819,g820)
    c: Coincident(g820,g821)
    c: Horizontal(g821)
    c: Coincident(g821,g822)
    c: Vertical(g822)
    c: Coincident(g822,g823)
    c: Coincident(g823,g824)
    c: Coincident(g824,g825)
    c: Horizontal(g825)
    c: Coincident(g825,g826)
    c: Coincident(g826,g827)
    c: Coincident(g827,g828)
    c: Coincident(g828,g829)
    c: Horizontal(g829)
    c: Coincident(g829,g830)
    c: Coincident(g830,g831)
    c: Coincident(g831,g832)
    c: Coincident(g832,g833)
    c: Horizontal(g834)
    c: Coincident(g834,g835)
    c: Coincident(g835,g836)
    c: Horizontal(g836)
    c: Coincident(g836,g837)
    c: Coincident(g837,g838)
    c: Horizontal(g838)
    c: Coincident(g838,g839)
    c: Coincident(g839,g840)
    c: Coincident(g840,g841)
    c: Coincident(g841,g842)
    c: Coincident(g842,g843)
    c: Coincident(g843,g844)
    c: Coincident(g844,g845)
    c: Coincident(g845,g846)
    c: Coincident(g846,g847)
    c: Coincident(g847,g848)
    c: Horizontal(g848)
    c: Coincident(g848,g849)
    c: Coincident(g849,g850)
    c: Coincident(g850,g851)
    c: Coincident(g851,g852)
    c: Coincident(g852,g853)
    c: Coincident(g853,g854)
    c: Coincident(g854,g855)
    c: Coincident(g855,g856)
    c: Coincident(g856,g857)
    c: Coincident(g857,g858)
    c: Horizontal(g858)
    c: Coincident(g858,g859)
    c: Coincident(g859,g860)
    c: Coincident(g860,g861)
    c: Coincident(g861,g862)
    c: Coincident(g862,g863)
    c: Coincident(g863,g864)
    c: Coincident(g786,g865)
    c: Coincident(g865,g866)
    c: Coincident(g866,g787)
    c: Vertical(g866)
    c: Horizontal(g709)
    c: Horizontal(g711)
    c: Horizontal(g715)
    c: Horizontal(g717)
    c: Horizontal(g719)
    c: Horizontal(g722)
    c: Coincident(g718,g867)
    c: Horizontal(g867)
    c: Coincident(g867,g868)
    c: Coincident(g868,g717)
    c: Coincident(g721,g869)
    c: Coincident(g869,g870)
    c: Coincident(g720,g870)
    c: Coincident(g871,g720)
    c: Coincident(g871,g719)
    c: Vertical(g871)
    c: Vertical(g870)
    c: Vertical(g723)
    c: Horizontal(g869)
    c: Coincident(g872,g726)
    c: Coincident(g873,g872)
    c: Coincident(g725,g873)
    c: Horizontal(g873)
    c: Horizontal(g736)
    c: Horizontal(g734)
    c: Horizontal(g732)
    c: Horizontal(g730)
    c: Horizontal(g738)
    c: Horizontal(g740)
    c: Horizontal(g742)
    c: Horizontal(g744)
    c: Horizontal(g746)
    c: Horizontal(g748)
    c: Horizontal(g750)
    c: Horizontal(g752)
    c: Horizontal(g754)
    c: Coincident(g758,g759)
    c: Horizontal(g756)
    c: Horizontal(g758)
    c: Coincident(g874,g759)
    c: Horizontal(g874)
    c: Coincident(g875,g760)
    c: Coincident(g875,g874)
    c: Horizontal(g760)
    c: Vertical(g762)
    c: Coincident(g765,g764)
    c: Vertical(g764)
    c: Vertical(g766)
    c: Vertical(g768)
    c: Coincident(g769,g768)
    c: Vertical(g770)
    c: Coincident(g876,g771)
    c: Coincident(g877,g772)
    c: Coincident(g877,g876)
    c: Vertical(g772)
    c: Vertical(g774)
    c: Vertical(g776)
    c: Vertical(g778)
    c: Vertical(g780)
    c: Vertical(g782)
    c: Vertical(g876)
    c: Horizontal(g773)
    c: Horizontal(g775)
    c: Horizontal(g777)
    c: Horizontal(g779)
    c: Horizontal(g781)
    c: Horizontal(g783)
    c: Horizontal(g785)
    c: Horizontal(g865)
    c: Vertical(g784)
    c: Vertical(g786)
    c: Vertical(g788)
    c: Vertical(g790)
    c: Horizontal(g789)
    c: Vertical(g792)
    c: Vertical(g794)
    c: Horizontal(g795)
    c: Vertical(g798)
    c: Vertical(g800)
    c: Vertical(g802)
    c: Horizontal(g801)
    c: Coincident(g804,g803)
    c: Horizontal(g805)
    c: Horizontal(g807)
    c: Horizontal(g809)
    c: Vertical(g806)
    c: Vertical(g808)
    c: Vertical(g812)
    c: Vertical(g816)
    c: Vertical(g814)
    c: Vertical(g818)
    c: Vertical(g820)
    c: Vertical(g824)
    c: Vertical(g826)
    c: Vertical(g828)
    c: Vertical(g830)
    c: Vertical(g832)
    c: Horizontal(g827)
    c: Horizontal(g823)
    c: Horizontal(g819)
    c: Horizontal(g817)
    c: Horizontal(g831)
    c: Horizontal(g833)
    c: Coincident(g878,g833)
    c: Coincident(g878,g834)
    c: Vertical(g837)
    c: Horizontal(g840)
    c: Horizontal(g842)
    c: Horizontal(g846)
    c: Horizontal(g850)
    c: Horizontal(g852)
    c: Horizontal(g854)
    c: Horizontal(g856)
    c: Horizontal(g860)
    c: Horizontal(g862)
    c: Horizontal(g864)
    c: Horizontal(g844)
    c: Coincident(g864,g879)
    c: Coincident(g879,g880)
    c: Coincident(g880,g881)
    c: Coincident(g881,g882)
    c: Horizontal(g882)
    c: Coincident(g883,g1)
    c: Coincident(g883,g0)
    c: Vertical(g883)
    c: Coincident(g0,g882)
    c: Coincident(g1,g2)
    c: Coincident(g3,g4)
    c: Coincident(g4,g5)
    c: Coincident(g5,g6)
    c: Coincident(g6,g7)
    c: Coincident(g13,g14)
    c: Coincident(g14,g15)
    c: Coincident(g16,g17)
    c: Coincident(g18,g19)
    c: Coincident(g22,g23)
    c: Coincident(g24,g25)
    c: Coincident(g27,g28)
    c: Vertical(g26)
    c: Coincident(g28,g29)
    c: Coincident(g30,g31)
    c: Horizontal(g29)
    c: Coincident(g37,g38)
    c: Coincident(g38,g39)
    c: Coincident(g39,g40)
    c: Coincident(g40,g41)
    c: Coincident(g42,g43)
    c: Coincident(g20,g21)
    c: Coincident(g21,g22)
    c: Coincident(g25,g26)
    c: Coincident(g48,g49)
    c: Coincident(g49,g50)
    c: Coincident(g58,g59)
    c: Horizontal(g59)
    c: Coincident(g61,g62)
    c: Coincident(g64,g65)
    c: Coincident(g65,g66)
    c: Coincident(g66,g67)
    c: Coincident(g68,g69)
    c: Coincident(g70,g71)
    c: Coincident(g72,g73)
    c: Coincident(g74,g75)
    c: Coincident(g86,g87)
    c: Coincident(g87,g88)
    c: Coincident(g92,g93)
    c: Coincident(g94,g95)
    c: Coincident(g96,g97)
    c: Coincident(g51,g52)
    c: Coincident(g62,g63)
    c: Coincident(g76,g77)
    c: Coincident(g77,g78)
    c: Coincident(g82,g83)
    c: Coincident(g83,g84)
FEATURE [Part::Extrusion] Extrude037  label="logoCut"
  Base = -> Sketch055
  Dir = (0,1,0)
  DirMode = 0
  FaceMakerClass = Part::FaceMakerBullseye
  LengthFwd = 10
  LengthRev = 0
  Placement = pos=(-39,-248,-155) rot=(0,0,1;0rad)
  Solid = true
  Symmetric = false
FEATURE [Part::Cut] Cut056  label="level4to3"
  Base = -> Fillet004
  Tool = -> Extrude037
FEATURE [Sketcher::SketchObject] Sketch056
  FullyConstrained = true
  sketch-geometry (4):
    g0: ArcOfCircle CenterX=0 CenterY=-150 CenterZ=0 NormalX=0 NormalY=0 NormalZ=1 AngleXU=0 Radius=93.5 StartAngle=4.49682 EndAngle=4.92796
    g1: LineSegment StartX=-20 StartY=-241.336 StartZ=0 EndX=-20 EndY=-237.336 EndZ=0
    g2: LineSegment StartX=-20 StartY=-237.336 StartZ=0 EndX=20 EndY=-237.336 EndZ=0
    g3: LineSegment StartX=20 StartY=-237.336 StartZ=0 EndX=20 EndY=-241.336 EndZ=0
  constraints (13):
    c: PointOnObject(g0,g-2)
    c: DistanceY(g0) = -150
    c: DistanceX(g0,g0) = 20
    c: DistanceX(g0,g0) = 20
    c: Diameter(g0) = 187
    c: Coincident(g1,g0)
    c: Horizontal(g2)
    c: Coincident(g3,g2)
    c: Coincident(g3,g0)
    c: Vertical(g3)
    c: Vertical(g1)
    c: Coincident(g1,g2)
    c: DistanceY(g0,g2) = 4
FEATURE [Part::Extrusion] Extrude038  label="logoAttach"
  Base = -> Sketch056
  Dir = (0,0,1)
  DirMode = 2
  FaceMakerClass = Part::FaceMakerBullseye
  LengthFwd = 28
  LengthRev = 0
  Placement = pos=(0,0,-160) rot=(0,0,1;0rad)
  Solid = true
  Symmetric = false
FEATURE [Part::Cylinder] Cylinder157
  Angle = 360
  AttacherType = Attacher::AttachEngine3D
  FirstAngle = 0
  Height = 10
  Placement = pos=(0,-238,-147.25) rot=(1,0,0;1.5708rad)
  Radius = 2
  SecondAngle = 0
FEATURE [Part::MultiFuse] Fusion105  label="logoAttach001"
  Placement = pos=(0,0,10) rot=(0,0,1;0rad)
  Shapes = -> [Extrude038,Cylinder157]
FEATURE [Part::Cylinder] Cylinder160
  Angle = 360
  AttacherType = Attacher::AttachEngine3D
  FirstAngle = 0
  Height = 10
  Placement = pos=(0,-150,75) rot=(0,0,1;0rad)
  Radius = 98
  SecondAngle = 0
FEATURE [Part::Cylinder] Cylinder161
  Angle = 360
  AttacherType = Attacher::AttachEngine3D
  FirstAngle = 0
  Height = 5
  Placement = pos=(0,-150,70) rot=(0,0,1;0rad)
  Radius = 86
  SecondAngle = 0
FEATURE [Part::Cylinder] Cylinder162
  Angle = 360
  AttacherType = Attacher::AttachEngine3D
  FirstAngle = 0
  Height = 300
  Placement = pos=(0,0,90) rot=(1,0,0;1.5708rad)
  Radius = 2.8
  SecondAngle = 0
FEATURE [Part::Cylinder] Cylinder163
  Angle = 360
  AttacherType = Attacher::AttachEngine3D
  FirstAngle = 0
  Height = 300
  Placement = pos=(-150,-150,90) rot=(0.57735,0.57735,0.57735;2.0944rad)
  Radius = 2.8
  SecondAngle = 0
FEATURE [Part::Cylinder] Cylinder164  label="srsCut002"
  Angle = 360
  AttacherType = Attacher::AttachEngine3D
  FirstAngle = 0
  Height = 100
  Placement = pos=(0,-150,0) rot=(0,0,1;0rad)
  Radius = 80
  SecondAngle = 0
FEATURE [Part::Cylinder] Cylinder165
  Angle = 360
  AttacherType = Attacher::AttachEngine3D
  FirstAngle = 0
  Height = 300
  Placement = pos=(0,0,90) rot=(1,0,0;1.5708rad)
  Radius = 2.8
  SecondAngle = 0
FEATURE [Part::Cylinder] Cylinder166
  Angle = 360
  AttacherType = Attacher::AttachEngine3D
  FirstAngle = 0
  Height = 300
  Placement = pos=(-150,-150,90) rot=(0.57735,0.57735,0.57735;2.0944rad)
  Radius = 2.8
  SecondAngle = 0
FEATURE [Part::Cylinder] Cylinder167
  Angle = 360
  AttacherType = Attacher::AttachEngine3D
  FirstAngle = 0
  Height = 300
  Placement = pos=(106.066,-43.934,90) rot=(0.862856,-0.357407,-0.357407;1.71777rad)
  Radius = 2.8
  SecondAngle = 0
FEATURE [Part::Cylinder] Cylinder168
  Angle = 360
  AttacherType = Attacher::AttachEngine3D
  FirstAngle = 0
  Height = 300
  Placement = pos=(-106.066,-43.934,90) rot=(0.862856,0.357407,0.357407;1.71777rad)
  Radius = 2.8
  SecondAngle = 0
FEATURE [Part::Cylinder] Cylinder169
  Angle = 360
  AttacherType = Attacher::AttachEngine3D
  FirstAngle = 0
  Height = 300
  Placement = pos=(0,0,90) rot=(1,0,0;1.5708rad)
  Radius = 2.13
  SecondAngle = 0
FEATURE [Part::Cylinder] Cylinder170
  Angle = 360
  AttacherType = Attacher::AttachEngine3D
  FirstAngle = 0
  Height = 300
  Placement = pos=(-150,-150,90) rot=(0.57735,0.57735,0.57735;2.0944rad)
  Radius = 2.13
  SecondAngle = 0
FEATURE [Part::MultiFuse] Fusion110  label="m4Cuts018"
  Shapes = -> [Cylinder163,Cylinder162]
FEATURE [Part::MultiFuse] Fusion112  label="srsCut003"
  Shapes = -> [Cylinder164,Fusion110]
FEATURE [Part::MultiFuse] Fusion113  label="m4Cuts019"
  Placement = pos=(0,0,-82) rot=(0,0,1;0rad)
  Shapes = -> [Cylinder166,Cylinder165]
FEATURE [Part::MultiFuse] Fusion114  label="m4Cuts020"
  Placement = pos=(0,0,-82) rot=(0,0,1;0rad)
  Shapes = -> [Cylinder167,Cylinder168]
FEATURE [Part::MultiFuse] Fusion115  label="m4Cuts021"
  Shapes = -> [Fusion113,Fusion114]
FEATURE [Part::MultiFuse] Fusion117  label="m4Cuts022"
  Placement = pos=(0,0,-321) rot=(0,0,1;0rad)
  Shapes = -> [Cylinder170,Cylinder169]
FEATURE [Sketcher::SketchObject] Sketch075
  FullyConstrained = true
  Placement = pos=(0,0,65) rot=(0,0,1;0rad)
  sketch-geometry (1):
    g0: Circle CenterX=0 CenterY=-150 CenterZ=0 NormalX=0 NormalY=0 NormalZ=1 AngleXU=0 Radius=98
  constraints (3):
    c: PointOnObject(g0,g-2)
    c: DistanceY(g0) = -150
    c: Radius(g0) = 98
FEATURE [Sketcher::SketchObject] Sketch076
  FullyConstrained = true
  Placement = pos=(0,0,80) rot=(0,0,1;0rad)
  sketch-geometry (1):
    g0: Circle CenterX=0 CenterY=-150 CenterZ=0 NormalX=0 NormalY=0 NormalZ=1 AngleXU=0 Radius=80
  constraints (3):
    c: PointOnObject(g0,g-2)
    c: DistanceY(g0) = -150
    c: Radius(g0) = 80
FEATURE [Part::Loft] Loft017  label="Loft029"
  Closed = false
  MaxDegree = 5
  Placement = pos=(0,0,-15) rot=(0,0,1;0rad)
  Ruled = false
  Sections = -> [Sketch076,Sketch075]
  Solid = true
FEATURE [Sketcher::SketchObject] Sketch077
  FullyConstrained = true
  Placement = pos=(0,0,65) rot=(0,0,1;0rad)
  sketch-geometry (1):
    g0: Circle CenterX=0 CenterY=-150 CenterZ=0 NormalX=0 NormalY=0 NormalZ=1 AngleXU=0 Radius=98
  constraints (3):
    c: PointOnObject(g0,g-2)
    c: DistanceY(g0) = -150
    c: Radius(g0) = 98
FEATURE [Sketcher::SketchObject] Sketch078
  FullyConstrained = true
  Placement = pos=(0,0,80) rot=(0,0,1;0rad)
  sketch-geometry (1):
    g0: Circle CenterX=0 CenterY=-150 CenterZ=0 NormalX=0 NormalY=0 NormalZ=1 AngleXU=0 Radius=80
  constraints (3):
    c: PointOnObject(g0,g-2)
    c: DistanceY(g0) = -150
    c: Radius(g0) = 80
FEATURE [Part::Loft] Loft018  label="Loft030"
  Closed = false
  MaxDegree = 5
  Placement = pos=(0,0,-20) rot=(0,0,1;0rad)
  Ruled = false
  Sections = -> [Sketch078,Sketch077]
  Solid = true
FEATURE [Part::Cut] Cut062  label="Loft025"
  Base = -> Loft017
  Tool = -> Loft018
FEATURE [Sketcher::SketchObject] Sketch079
  FullyConstrained = true
  Placement = pos=(0,0,65) rot=(0,0,1;0rad)
  sketch-geometry (1):
    g0: Circle CenterX=0 CenterY=-150 CenterZ=0 NormalX=0 NormalY=0 NormalZ=1 AngleXU=0 Radius=98
  constraints (3):
    c: PointOnObject(g0,g-2)
    c: DistanceY(g0) = -150
    c: Radius(g0) = 98
FEATURE [Sketcher::SketchObject] Sketch080
  FullyConstrained = true
  Placement = pos=(0,0,80) rot=(0,0,1;0rad)
  sketch-geometry (1):
    g0: Circle CenterX=0 CenterY=-150 CenterZ=0 NormalX=0 NormalY=0 NormalZ=1 AngleXU=0 Radius=80
  constraints (3):
    c: PointOnObject(g0,g-2)
    c: DistanceY(g0) = -150
    c: Radius(g0) = 80
FEATURE [Part::Loft] Loft019  label="Loft031"
  Closed = false
  MaxDegree = 5
  Placement = pos=(0,0,-15) rot=(0,0,1;0rad)
  Ruled = false
  Sections = -> [Sketch080,Sketch079]
  Solid = true
FEATURE [Sketcher::SketchObject] Sketch081
  FullyConstrained = true
  Placement = pos=(0,0,65) rot=(0,0,1;0rad)
  sketch-geometry (1):
    g0: Circle CenterX=0 CenterY=-150 CenterZ=0 NormalX=0 NormalY=0 NormalZ=1 AngleXU=0 Radius=98
  constraints (3):
    c: PointOnObject(g0,g-2)
    c: DistanceY(g0) = -150
    c: Radius(g0) = 98
FEATURE [Sketcher::SketchObject] Sketch082
  FullyConstrained = true
  Placement = pos=(0,0,80) rot=(0,0,1;0rad)
  sketch-geometry (1):
    g0: Circle CenterX=0 CenterY=-150 CenterZ=0 NormalX=0 NormalY=0 NormalZ=1 AngleXU=0 Radius=80
  constraints (3):
    c: PointOnObject(g0,g-2)
    c: DistanceY(g0) = -150
    c: Radius(g0) = 80
FEATURE [Part::Loft] Loft020  label="Loft032"
  Closed = false
  MaxDegree = 5
  Placement = pos=(0,0,-20) rot=(0,0,1;0rad)
  Ruled = false
  Sections = -> [Sketch082,Sketch081]
  Solid = true
FEATURE [Part::Cut] Cut063  label="Loft026"
  Base = -> Loft019
  Placement = pos=(0,0,-15) rot=(0,0,1;0rad)
  Tool = -> Loft020
FEATURE [Sketcher::SketchObject] Sketch083
  FullyConstrained = true
  Placement = pos=(0,0,65) rot=(0,0,1;0rad)
  sketch-geometry (1):
    g0: Circle CenterX=0 CenterY=-150 CenterZ=0 NormalX=0 NormalY=0 NormalZ=1 AngleXU=0 Radius=98
  constraints (3):
    c: PointOnObject(g0,g-2)
    c: DistanceY(g0) = -150
    c: Radius(g0) = 98
FEATURE [Sketcher::SketchObject] Sketch084
  FullyConstrained = true
  Placement = pos=(0,0,80) rot=(0,0,1;0rad)
  sketch-geometry (1):
    g0: Circle CenterX=0 CenterY=-150 CenterZ=0 NormalX=0 NormalY=0 NormalZ=1 AngleXU=0 Radius=80
  constraints (3):
    c: PointOnObject(g0,g-2)
    c: DistanceY(g0) = -150
    c: Radius(g0) = 80
FEATURE [Part::Loft] Loft021  label="Loft033"
  Closed = false
  MaxDegree = 5
  Placement = pos=(0,0,-15) rot=(0,0,1;0rad)
  Ruled = false
  Sections = -> [Sketch084,Sketch083]
  Solid = true
FEATURE [Sketcher::SketchObject] Sketch085
  FullyConstrained = true
  Placement = pos=(0,0,65) rot=(0,0,1;0rad)
  sketch-geometry (1):
    g0: Circle CenterX=0 CenterY=-150 CenterZ=0 NormalX=0 NormalY=0 NormalZ=1 AngleXU=0 Radius=98
  constraints (3):
    c: PointOnObject(g0,g-2)
    c: DistanceY(g0) = -150
    c: Radius(g0) = 98
FEATURE [Sketcher::SketchObject] Sketch086
  FullyConstrained = true
  Placement = pos=(0,0,80) rot=(0,0,1;0rad)
  sketch-geometry (1):
    g0: Circle CenterX=0 CenterY=-150 CenterZ=0 NormalX=0 NormalY=0 NormalZ=1 AngleXU=0 Radius=80
  constraints (3):
    c: PointOnObject(g0,g-2)
    c: DistanceY(g0) = -150
    c: Radius(g0) = 80
FEATURE [Part::Loft] Loft022  label="Loft034"
  Closed = false
  MaxDegree = 5
  Placement = pos=(0,0,-20) rot=(0,0,1;0rad)
  Ruled = false
  Sections = -> [Sketch086,Sketch085]
  Solid = true
FEATURE [Part::Cut] Cut064  label="Loft027"
  Base = -> Loft021
  Placement = pos=(0,0,-30) rot=(0,0,1;0rad)
  Tool = -> Loft022
FEATURE [Sketcher::SketchObject] Sketch087
  FullyConstrained = true
  Placement = pos=(0,0,65) rot=(0,0,1;0rad)
  sketch-geometry (1):
    g0: Circle CenterX=0 CenterY=-150 CenterZ=0 NormalX=0 NormalY=0 NormalZ=1 AngleXU=0 Radius=98
  constraints (3):
    c: PointOnObject(g0,g-2)
    c: DistanceY(g0) = -150
    c: Radius(g0) = 98
FEATURE [Sketcher::SketchObject] Sketch088
  FullyConstrained = true
  Placement = pos=(0,0,80) rot=(0,0,1;0rad)
  sketch-geometry (1):
    g0: Circle CenterX=0 CenterY=-150 CenterZ=0 NormalX=0 NormalY=0 NormalZ=1 AngleXU=0 Radius=80
  constraints (3):
    c: PointOnObject(g0,g-2)
    c: DistanceY(g0) = -150
    c: Radius(g0) = 80
FEATURE [Part::Loft] Loft023  label="Loft035"
  Closed = false
  MaxDegree = 5
  Placement = pos=(0,0,-15) rot=(0,0,1;0rad)
  Ruled = false
  Sections = -> [Sketch088,Sketch087]
  Solid = true
FEATURE [Sketcher::SketchObject] Sketch089
  FullyConstrained = true
  Placement = pos=(0,0,65) rot=(0,0,1;0rad)
  sketch-geometry (1):
    g0: Circle CenterX=0 CenterY=-150 CenterZ=0 NormalX=0 NormalY=0 NormalZ=1 AngleXU=0 Radius=98
  constraints (3):
    c: PointOnObject(g0,g-2)
    c: DistanceY(g0) = -150
    c: Radius(g0) = 98
FEATURE [Sketcher::SketchObject] Sketch090
  FullyConstrained = true
  Placement = pos=(0,0,80) rot=(0,0,1;0rad)
  sketch-geometry (1):
    g0: Circle CenterX=0 CenterY=-150 CenterZ=0 NormalX=0 NormalY=0 NormalZ=1 AngleXU=0 Radius=80
  constraints (3):
    c: PointOnObject(g0,g-2)
    c: DistanceY(g0) = -150
    c: Radius(g0) = 80
FEATURE [Part::Loft] Loft024  label="Loft036"
  Closed = false
  MaxDegree = 5
  Placement = pos=(0,0,-20) rot=(0,0,1;0rad)
  Ruled = false
  Sections = -> [Sketch090,Sketch089]
  Solid = true
FEATURE [Part::Cut] Cut065  label="Loft028"
  Base = -> Loft023
  Placement = pos=(0,0,15) rot=(0,0,1;0rad)
  Tool = -> Loft024
FEATURE [Part::Cut] Cut066  label="top021"
  Base = -> Cut065
  Tool = -> Cylinder160
FEATURE [Part::MultiFuse] Fusion108  label="top022"
  Shapes = -> [Cut066,Cylinder161]
FEATURE [Part::MultiFuse] Fusion109  label="solarRadiationShield002"
  Shapes = -> [Fusion108,Cut062,Cut063,Cut064]
FEATURE [Sketcher::SketchObject] Sketch091
  FullyConstrained = true
  sketch-geometry (16):
    g0: ArcOfCircle CenterX=0 CenterY=-150 CenterZ=0 NormalX=0 NormalY=0 NormalZ=1 AngleXU=0 Radius=93 StartAngle=2.86943 EndAngle=3.41376
    g1: ArcOfCircle CenterX=0 CenterY=-150 CenterZ=0 NormalX=0 NormalY=0 NormalZ=1 AngleXU=0 Radius=93 StartAngle=1.29863 EndAngle=1.84296
    g2: ArcOfCircle CenterX=0 CenterY=-150 CenterZ=0 NormalX=0 NormalY=0 NormalZ=1 AngleXU=0 Radius=93 StartAngle=6.01102 EndAngle=6.55535
    g3: ArcOfCircle CenterX=0 CenterY=-150 CenterZ=0 NormalX=0 NormalY=0 NormalZ=1 AngleXU=0 Radius=93 StartAngle=4.44022 EndAngle=4.98455
    g4: ArcOfCircle CenterX=0 CenterY=-150 CenterZ=0 NormalX=0 NormalY=0 NormalZ=1 AngleXU=0 Radius=86 StartAngle=1.27584 EndAngle=1.86575
    g5: ArcOfCircle CenterX=0 CenterY=-150 CenterZ=0 NormalX=0 NormalY=0 NormalZ=1 AngleXU=0 Radius=86 StartAngle=5.98823 EndAngle=6.57814
    g6: ArcOfCircle CenterX=0 CenterY=-150 CenterZ=0 NormalX=0 NormalY=0 NormalZ=1 AngleXU=0 Radius=86 StartAngle=2.84664 EndAngle=3.43655
    g7: ArcOfCircle CenterX=0 CenterY=-150 CenterZ=0 NormalX=0 NormalY=0 NormalZ=1 AngleXU=0 Radius=86 StartAngle=4.41743 EndAngle=5.00734
    g8: LineSegment StartX=25 StartY=-60.4232 StartZ=0 EndX=25 EndY=-67.7139 EndZ=0
    g9: LineSegment StartX=-25 StartY=-60.4232 StartZ=0 EndX=-25 EndY=-67.7139 EndZ=0
    g10: LineSegment StartX=-89.5768 StartY=-125 StartZ=0 EndX=-82.2861 EndY=-125 EndZ=0
    g11: LineSegment StartX=-89.5768 StartY=-175 StartZ=0 EndX=-82.2861 EndY=-175 EndZ=0
    g12: LineSegment StartX=-25 StartY=-239.577 StartZ=0 EndX=-25 EndY=-232.286 EndZ=0
    g13: LineSegment StartX=25 StartY=-239.577 StartZ=0 EndX=25 EndY=-232.286 EndZ=0
    g14: LineSegment StartX=89.5768 StartY=-175 StartZ=0 EndX=82.2861 EndY=-175 EndZ=0
    g15: LineSegment StartX=89.5768 StartY=-125 StartZ=0 EndX=82.2861 EndY=-125 EndZ=0
  constraints (49):
    c: PointOnObject(g0,g-2)
    c: Coincident(g1,g0)
    c: Coincident(g2,g0)
    c: Coincident(g3,g0)
    c: DistanceY(g0) = -150
    c: Coincident(g4,g0)
    c: Coincident(g5,g0)
    c: Coincident(g6,g0)
    c: Coincident(g7,g0)
    c: DistanceX(g4,g0) = 25
    c: DistanceX(g1,g4) = 0
    c: DistanceX(g0,g4) = 25
    c: DistanceX(g4,g1) = 0
    c: DistanceY(g0,g5) = 25
    c: DistanceY(g5,g2) = 0
    c: DistanceY(g2,g0) = 25
    c: DistanceY(g2,g5) = 0
    c: DistanceY(g6,g0) = 25
    c: DistanceY(g0,g6) = 0
    c: DistanceY(g0,g6) = 25
    c: DistanceY(g6,g0) = 0
    c: Equal(g1,g2)
    c: Equal(g1,g3)
    c: Equal(g1,g0)
    c: Radius(g1) = 93
    c: Equal(g6,g4)
    c: Equal(g6,g5)
    c: Equal(g6,g7)
    c: Radius(g6) = 86
    c: DistanceX(g0,g7) = 25
    c: DistanceX(g7,g3) = 0
    c: DistanceX(g3) = -25
    c: DistanceX(g3,g7) = 0
    c: Coincident(g8,g1)
    c: Coincident(g8,g4)
    c: Coincident(g9,g1)
    c: Coincident(g9,g4)
    c: Coincident(g10,g0)
    c: Coincident(g10,g6)
    c: Coincident(g11,g0)
    c: Coincident(g11,g6)
    c: Coincident(g12,g3)
    c: Coincident(g12,g7)
    c: Coincident(g13,g3)
    c: Coincident(g13,g7)
    c: Coincident(g14,g2)
    c: Coincident(g14,g5)
    c: Coincident(g15,g2)
    c: Coincident(g15,g5)
FEATURE [Part::Extrusion] Extrude040  label="srsHolds003"
  Base = -> Sketch091
  Dir = (0,0,1)
  DirMode = 2
  FaceMakerClass = Part::FaceMakerBullseye
  LengthFwd = 95.5
  LengthRev = 0
  Solid = true
  Symmetric = false
FEATURE [Part::MultiFuse] Fusion111  label="srs006"
  Shapes = -> [Fusion109,Extrude040]
FEATURE [Part::Cut] Cut067  label="srs004"
  Base = -> Fusion111
  Tool = -> Fusion112
FEATURE [Part::Cut] Cut068  label="srs005"
  Base = -> Cut067
  Tool = -> Fusion115
FEATURE [Sketcher::SketchObject] Sketch092  label="top023"
  FullyConstrained = true
  sketch-geometry (2):
    g0: Circle CenterX=0 CenterY=-150 CenterZ=0 NormalX=0 NormalY=0 NormalZ=1 AngleXU=0 Radius=98
    g1: Circle CenterX=0 CenterY=-150 CenterZ=0 NormalX=0 NormalY=0 NormalZ=1 AngleXU=0 Radius=76
  constraints (5):
    c: PointOnObject(g0,g-2)
    c: Diameter(g0) = 196
    c: DistanceY(g0) = -150
    c: Coincident(g1,g0)
    c: Radius(g1) = 76
FEATURE [Part::Extrusion] Extrude041  label="TupeConnectLevel008"
  Base = -> Sketch092
  Dir = (0,0,1)
  DirMode = 2
  FaceMakerClass = Part::FaceMakerBullseye
  LengthFwd = 5
  LengthRev = 0
  Placement = pos=(0,0,-65) rot=(0,0,1;0rad)
  Solid = true
  Symmetric = false
FEATURE [Sketcher::SketchObject] Sketch093
  FullyConstrained = true
  sketch-geometry (4):
    g0: Circle CenterX=0 CenterY=-68 CenterZ=0 NormalX=0 NormalY=0 NormalZ=1 AngleXU=0 Radius=2.8
    g1: Circle CenterX=82 CenterY=-150 CenterZ=0 NormalX=0 NormalY=0 NormalZ=1 AngleXU=0 Radius=2.8
    g2: Circle CenterX=0 CenterY=-232 CenterZ=0 NormalX=0 NormalY=0 NormalZ=1 AngleXU=0 Radius=2.8
    g3: Circle CenterX=-82 CenterY=-150 CenterZ=0 NormalX=0 NormalY=0 NormalZ=1 AngleXU=0 Radius=2.8
  constraints (12):
    c: PointOnObject(g0,g-2)
    c: DistanceY(g1) = -150
    c: DistanceY(g1,g3) = 0
    c: DistanceX(g2) = 0
    c: DistanceX(g1) = 82
    c: Equal(g1,g0)
    c: Equal(g1,g3)
    c: Equal(g1,g2)
    c: Diameter(g1) = 5.6
    c: DistanceX(g3) = -82
    c: DistanceY(g3,g0) = 82
    c: DistanceY(g2,g3) = 82
FEATURE [Part::Extrusion] Extrude042  label="m4HeatSetVerCuts007"
  Base = -> Sketch093
  Dir = (0,0,1)
  DirMode = 2
  FaceMakerClass = Part::FaceMakerBullseye
  LengthFwd = 20
  LengthRev = 0
  Placement = pos=(0,0,-193) rot=(0,0,1;0rad)
  Solid = true
  Symmetric = false
FEATURE [Part::FeaturePython] Tube011  # WARN: FeaturePython — macro-defined, semantics opaque (R4)
  AttacherType = Attacher::AttachEngine3D
  Height = 3
  InnerRadius = 95
  OuterRadius = 98
  Placement = pos=(0,-150,-188) rot=(0,0,1;0rad)
FEATURE [Part::FeaturePython] Tube012  # WARN: FeaturePython — macro-defined, semantics opaque (R4)
  AttacherType = Attacher::AttachEngine3D
  Height = 65
  InnerRadius = 94
  OuterRadius = 98
  Placement = pos=(0,-150,-125) rot=(0,0,1;0rad)
FEATURE [Part::MultiFuse] Fusion116  label="tube5to008"
  Placement = pos=(0,0,-125) rot=(0,0,1;0rad)
  Shapes = -> [Extrude041,Tube012]
FEATURE [Part::Cut] Cut069  label="tube4to009"
  Base = -> Fusion116
  Tool = -> Fusion117
FEATURE [Part::Cut] Cut070  label="tube4to5s004"
  Base = -> Cut069
  Tool = -> Extrude042
FEATURE [Part::Fillet] Fillet011  label="level5s006"
  Base = -> Cut070
  Edges = 3 edges r=3: [Edge3,Edge7,Edge32]
FEATURE [Part::Cut] Cut071  label="cutAddOn003"
  Base = -> Tube011
  Placement = pos=(0,0,205.25) rot=(0,0,1;0rad)
  Tool = -> Fillet011
FEATURE [Part::MultiFuse] Fusion118  label="srs007"
  Shapes = -> [Cut071,Cut068]
FEATURE [Sketcher::SketchObject] Sketch094
  FullyConstrained = true
  Placement = pos=(0,0,65) rot=(0,0,1;0rad)
  sketch-geometry (1):
    g0: Circle CenterX=0 CenterY=-150 CenterZ=0 NormalX=0 NormalY=0 NormalZ=1 AngleXU=0 Radius=100
  constraints (3):
    c: PointOnObject(g0,g-2)
    c: DistanceY(g0) = -150
    c: Radius(g0) = 100
FEATURE [Sketcher::SketchObject] Sketch095
  FullyConstrained = true
  Placement = pos=(0,0,80) rot=(0,0,1;0rad)
  sketch-geometry (1):
    g0: Circle CenterX=0 CenterY=-150 CenterZ=0 NormalX=0 NormalY=0 NormalZ=1 AngleXU=0 Radius=92
  constraints (3):
    c: PointOnObject(g0,g-2)
    c: DistanceY(g0) = -150
    c: Radius(g0) = 92
FEATURE [Part::Loft] Loft025  label="Loft037"
  Closed = false
  MaxDegree = 5
  Placement = pos=(0,0,-193.5) rot=(0,0,1;0rad)
  Ruled = false
  Sections = -> [Sketch095,Sketch094]
  Solid = true
FEATURE [Sketcher::SketchObject] Sketch096
  FullyConstrained = true
  Placement = pos=(0,0,65) rot=(0,0,1;0rad)
  sketch-geometry (1):
    g0: Circle CenterX=0 CenterY=-150 CenterZ=0 NormalX=0 NormalY=0 NormalZ=1 AngleXU=0 Radius=100
  constraints (3):
    c: PointOnObject(g0,g-2)
    c: DistanceY(g0) = -150
    c: Radius(g0) = 100
FEATURE [Sketcher::SketchObject] Sketch097
  FullyConstrained = true
  Placement = pos=(0,0,80) rot=(0,0,1;0rad)
  sketch-geometry (1):
    g0: Circle CenterX=0 CenterY=-150 CenterZ=0 NormalX=0 NormalY=0 NormalZ=1 AngleXU=0 Radius=92
  constraints (3):
    c: PointOnObject(g0,g-2)
    c: DistanceY(g0) = -150
    c: Radius(g0) = 92
FEATURE [Part::Loft] Loft026  label="Loft038"
  Closed = false
  MaxDegree = 5
  Placement = pos=(0,0,-191.5) rot=(0,0,1;0rad)
  Ruled = false
  Sections = -> [Sketch097,Sketch096]
  Solid = true
FEATURE [Part::Cut] Cut072
  Base = -> Loft026
  Tool = -> Loft025
FEATURE [Sketcher::SketchObject] Sketch098
  FullyConstrained = true
  Placement = pos=(0,0,65) rot=(0,0,1;0rad)
  sketch-geometry (1):
    g0: Circle CenterX=0 CenterY=-150 CenterZ=0 NormalX=0 NormalY=0 NormalZ=1 AngleXU=0 Radius=100
  constraints (3):
    c: PointOnObject(g0,g-2)
    c: DistanceY(g0) = -150
    c: Radius(g0) = 100
FEATURE [Sketcher::SketchObject] Sketch099
  FullyConstrained = true
  Placement = pos=(0,0,80) rot=(0,0,1;0rad)
  sketch-geometry (1):
    g0: Circle CenterX=0 CenterY=-150 CenterZ=0 NormalX=0 NormalY=0 NormalZ=1 AngleXU=0 Radius=92
  constraints (3):
    c: PointOnObject(g0,g-2)
    c: DistanceY(g0) = -150
    c: Radius(g0) = 92
FEATURE [Part::Loft] Loft027  label="Loft039"
  Closed = false
  MaxDegree = 5
  Placement = pos=(0,0,-193.5) rot=(0,0,1;0rad)
  Ruled = false
  Sections = -> [Sketch099,Sketch098]
  Solid = true
FEATURE [Sketcher::SketchObject] Sketch100
  FullyConstrained = true
  Placement = pos=(0,0,65) rot=(0,0,1;0rad)
  sketch-geometry (1):
    g0: Circle CenterX=0 CenterY=-150 CenterZ=0 NormalX=0 NormalY=0 NormalZ=1 AngleXU=0 Radius=100
  constraints (3):
    c: PointOnObject(g0,g-2)
    c: DistanceY(g0) = -150
    c: Radius(g0) = 100
FEATURE [Sketcher::SketchObject] Sketch101
  FullyConstrained = true
  Placement = pos=(0,0,80) rot=(0,0,1;0rad)
  sketch-geometry (1):
    g0: Circle CenterX=0 CenterY=-150 CenterZ=0 NormalX=0 NormalY=0 NormalZ=1 AngleXU=0 Radius=92
  constraints (3):
    c: PointOnObject(g0,g-2)
    c: DistanceY(g0) = -150
    c: Radius(g0) = 92
FEATURE [Part::Loft] Loft028  label="Loft040"
  Closed = false
  MaxDegree = 5
  Placement = pos=(0,0,-191.5) rot=(0,0,1;0rad)
  Ruled = false
  Sections = -> [Sketch101,Sketch100]
  Solid = true
FEATURE [Part::Cut] Cut073
  Base = -> Loft028
  Placement = pos=(0,0,8) rot=(0,0,1;0rad)
  Tool = -> Loft027
FEATURE [Sketcher::SketchObject] Sketch102
  FullyConstrained = true
  Placement = pos=(0,0,65) rot=(0,0,1;0rad)
  sketch-geometry (1):
    g0: Circle CenterX=0 CenterY=-150 CenterZ=0 NormalX=0 NormalY=0 NormalZ=1 AngleXU=0 Radius=100
  constraints (3):
    c: PointOnObject(g0,g-2)
    c: DistanceY(g0) = -150
    c: Radius(g0) = 100
FEATURE [Sketcher::SketchObject] Sketch103
  FullyConstrained = true
  Placement = pos=(0,0,80) rot=(0,0,1;0rad)
  sketch-geometry (1):
    g0: Circle CenterX=0 CenterY=-150 CenterZ=0 NormalX=0 NormalY=0 NormalZ=1 AngleXU=0 Radius=92
  constraints (3):
    c: PointOnObject(g0,g-2)
    c: DistanceY(g0) = -150
    c: Radius(g0) = 92
FEATURE [Part::Loft] Loft029  label="Loft041"
  Closed = false
  MaxDegree = 5
  Placement = pos=(0,0,-193.5) rot=(0,0,1;0rad)
  Ruled = false
  Sections = -> [Sketch103,Sketch102]
  Solid = true
FEATURE [Sketcher::SketchObject] Sketch104
  FullyConstrained = true
  Placement = pos=(0,0,65) rot=(0,0,1;0rad)
  sketch-geometry (1):
    g0: Circle CenterX=0 CenterY=-150 CenterZ=0 NormalX=0 NormalY=0 NormalZ=1 AngleXU=0 Radius=100
  constraints (3):
    c: PointOnObject(g0,g-2)
    c: DistanceY(g0) = -150
    c: Radius(g0) = 100
FEATURE [Sketcher::SketchObject] Sketch105
  FullyConstrained = true
  Placement = pos=(0,0,80) rot=(0,0,1;0rad)
  sketch-geometry (1):
    g0: Circle CenterX=0 CenterY=-150 CenterZ=0 NormalX=0 NormalY=0 NormalZ=1 AngleXU=0 Radius=92
  constraints (3):
    c: PointOnObject(g0,g-2)
    c: DistanceY(g0) = -150
    c: Radius(g0) = 92
FEATURE [Part::Loft] Loft030  label="Loft042"
  Closed = false
  MaxDegree = 5
  Placement = pos=(0,0,-191.5) rot=(0,0,1;0rad)
  Ruled = false
  Sections = -> [Sketch105,Sketch104]
  Solid = true
FEATURE [Part::Cut] Cut074
  Base = -> Loft030
  Placement = pos=(0,0,16) rot=(0,0,1;0rad)
  Tool = -> Loft029
FEATURE [Sketcher::SketchObject] Sketch106
  FullyConstrained = true
  Placement = pos=(0,0,65) rot=(0,0,1;0rad)
  sketch-geometry (1):
    g0: Circle CenterX=0 CenterY=-150 CenterZ=0 NormalX=0 NormalY=0 NormalZ=1 AngleXU=0 Radius=100
  constraints (3):
    c: PointOnObject(g0,g-2)
    c: DistanceY(g0) = -150
    c: Radius(g0) = 100
FEATURE [Sketcher::SketchObject] Sketch107
  FullyConstrained = true
  Placement = pos=(0,0,80) rot=(0,0,1;0rad)
  sketch-geometry (1):
    g0: Circle CenterX=0 CenterY=-150 CenterZ=0 NormalX=0 NormalY=0 NormalZ=1 AngleXU=0 Radius=92
  constraints (3):
    c: PointOnObject(g0,g-2)
    c: DistanceY(g0) = -150
    c: Radius(g0) = 92
FEATURE [Part::Loft] Loft031  label="Loft043"
  Closed = false
  MaxDegree = 5
  Placement = pos=(0,0,-193.5) rot=(0,0,1;0rad)
  Ruled = false
  Sections = -> [Sketch107,Sketch106]
  Solid = true
FEATURE [Sketcher::SketchObject] Sketch108
  FullyConstrained = true
  Placement = pos=(0,0,65) rot=(0,0,1;0rad)
  sketch-geometry (1):
    g0: Circle CenterX=0 CenterY=-150 CenterZ=0 NormalX=0 NormalY=0 NormalZ=1 AngleXU=0 Radius=100
  constraints (3):
    c: PointOnObject(g0,g-2)
    c: DistanceY(g0) = -150
    c: Radius(g0) = 100
FEATURE [Sketcher::SketchObject] Sketch109
  FullyConstrained = true
  Placement = pos=(0,0,80) rot=(0,0,1;0rad)
  sketch-geometry (1):
    g0: Circle CenterX=0 CenterY=-150 CenterZ=0 NormalX=0 NormalY=0 NormalZ=1 AngleXU=0 Radius=92
  constraints (3):
    c: PointOnObject(g0,g-2)
    c: DistanceY(g0) = -150
    c: Radius(g0) = 92
FEATURE [Part::Loft] Loft032  label="Loft044"
  Closed = false
  MaxDegree = 5
  Placement = pos=(0,0,-191.5) rot=(0,0,1;0rad)
  Ruled = false
  Sections = -> [Sketch109,Sketch108]
  Solid = true
FEATURE [Part::Cut] Cut075
  Base = -> Loft032
  Placement = pos=(0,0,24) rot=(0,0,1;0rad)
  Tool = -> Loft031
FEATURE [Sketcher::SketchObject] Sketch110
  FullyConstrained = true
  Placement = pos=(0,0,65) rot=(0,0,1;0rad)
  sketch-geometry (1):
    g0: Circle CenterX=0 CenterY=-150 CenterZ=0 NormalX=0 NormalY=0 NormalZ=1 AngleXU=0 Radius=100
  constraints (3):
    c: PointOnObject(g0,g-2)
    c: DistanceY(g0) = -150
    c: Radius(g0) = 100
FEATURE [Sketcher::SketchObject] Sketch111
  FullyConstrained = true
  Placement = pos=(0,0,80) rot=(0,0,1;0rad)
  sketch-geometry (1):
    g0: Circle CenterX=0 CenterY=-150 CenterZ=0 NormalX=0 NormalY=0 NormalZ=1 AngleXU=0 Radius=92
  constraints (3):
    c: PointOnObject(g0,g-2)
    c: DistanceY(g0) = -150
    c: Radius(g0) = 92
FEATURE [Part::Loft] Loft033  label="Loft045"
  Closed = false
  MaxDegree = 5
  Placement = pos=(0,0,-193.5) rot=(0,0,1;0rad)
  Ruled = false
  Sections = -> [Sketch111,Sketch110]
  Solid = true
FEATURE [Sketcher::SketchObject] Sketch112
  FullyConstrained = true
  Placement = pos=(0,0,65) rot=(0,0,1;0rad)
  sketch-geometry (1):
    g0: Circle CenterX=0 CenterY=-150 CenterZ=0 NormalX=0 NormalY=0 NormalZ=1 AngleXU=0 Radius=100
  constraints (3):
    c: PointOnObject(g0,g-2)
    c: DistanceY(g0) = -150
    c: Radius(g0) = 100
FEATURE [Sketcher::SketchObject] Sketch113
  FullyConstrained = true
  Placement = pos=(0,0,80) rot=(0,0,1;0rad)
  sketch-geometry (1):
    g0: Circle CenterX=0 CenterY=-150 CenterZ=0 NormalX=0 NormalY=0 NormalZ=1 AngleXU=0 Radius=92
  constraints (3):
    c: PointOnObject(g0,g-2)
    c: DistanceY(g0) = -150
    c: Radius(g0) = 92
FEATURE [Part::Loft] Loft034  label="Loft046"
  Closed = false
  MaxDegree = 5
  Placement = pos=(0,0,-191.5) rot=(0,0,1;0rad)
  Ruled = false
  Sections = -> [Sketch113,Sketch112]
  Solid = true
FEATURE [Part::Cut] Cut076
  Base = -> Loft034
  Placement = pos=(0,0,32) rot=(0,0,1;0rad)
  Tool = -> Loft033
FEATURE [Sketcher::SketchObject] Sketch114
  FullyConstrained = true
  Placement = pos=(0,0,65) rot=(0,0,1;0rad)
  sketch-geometry (1):
    g0: Circle CenterX=0 CenterY=-150 CenterZ=0 NormalX=0 NormalY=0 NormalZ=1 AngleXU=0 Radius=100
  constraints (3):
    c: PointOnObject(g0,g-2)
    c: DistanceY(g0) = -150
    c: Radius(g0) = 100
FEATURE [Sketcher::SketchObject] Sketch115
  FullyConstrained = true
  Placement = pos=(0,0,80) rot=(0,0,1;0rad)
  sketch-geometry (1):
    g0: Circle CenterX=0 CenterY=-150 CenterZ=0 NormalX=0 NormalY=0 NormalZ=1 AngleXU=0 Radius=92
  constraints (3):
    c: PointOnObject(g0,g-2)
    c: DistanceY(g0) = -150
    c: Radius(g0) = 92
FEATURE [Part::Loft] Loft035  label="Loft047"
  Closed = false
  MaxDegree = 5
  Placement = pos=(0,0,-193.5) rot=(0,0,1;0rad)
  Ruled = false
  Sections = -> [Sketch115,Sketch114]
  Solid = true
FEATURE [Sketcher::SketchObject] Sketch116
  FullyConstrained = true
  Placement = pos=(0,0,65) rot=(0,0,1;0rad)
  sketch-geometry (1):
    g0: Circle CenterX=0 CenterY=-150 CenterZ=0 NormalX=0 NormalY=0 NormalZ=1 AngleXU=0 Radius=100
  constraints (3):
    c: PointOnObject(g0,g-2)
    c: DistanceY(g0) = -150
    c: Radius(g0) = 100
FEATURE [Sketcher::SketchObject] Sketch117
  FullyConstrained = true
  Placement = pos=(0,0,80) rot=(0,0,1;0rad)
  sketch-geometry (1):
    g0: Circle CenterX=0 CenterY=-150 CenterZ=0 NormalX=0 NormalY=0 NormalZ=1 AngleXU=0 Radius=92
  constraints (3):
    c: PointOnObject(g0,g-2)
    c: DistanceY(g0) = -150
    c: Radius(g0) = 92
FEATURE [Part::Loft] Loft036  label="Loft048"
  Closed = false
  MaxDegree = 5
  Placement = pos=(0,0,-191.5) rot=(0,0,1;0rad)
  Ruled = false
  Sections = -> [Sketch117,Sketch116]
  Solid = true
FEATURE [Part::Cut] Cut077
  Base = -> Loft036
  Placement = pos=(0,0,40) rot=(0,0,1;0rad)
  Tool = -> Loft035
FEATURE [Part::MultiFuse] Fusion119  label="fanCuts"
  Shapes = -> [Cut072,Cut073,Cut074,Cut075,Cut076,Cut077]
FEATURE [Sketcher::SketchObject] Sketch118
  FullyConstrained = true
  sketch-geometry (4):
    g0: LineSegment StartX=35 StartY=-45 StartZ=0 EndX=-35 EndY=-45 EndZ=0
    g1: LineSegment StartX=-35 StartY=-45 StartZ=0 EndX=-35 EndY=-265 EndZ=0
    g2: LineSegment StartX=-35 StartY=-265 StartZ=0 EndX=35 EndY=-265 EndZ=0
    g3: LineSegment StartX=35 StartY=-265 StartZ=0 EndX=35 EndY=-45 EndZ=0
  constraints (12):
    c: Coincident(g0,g1)
    c: Coincident(g1,g2)
    c: Coincident(g2,g3)
    c: Coincident(g3,g0)
    c: Horizontal(g0)
    c: Horizontal(g2)
    c: Vertical(g1)
    c: Vertical(g3)
    c: DistanceX(g2) = 35
    c: DistanceX(g1) = -35
    c: DistanceY(g1,g1) = 220
    c: DistanceY(g0) = -45
FEATURE [Part::Extrusion] Extrude043
  Base = -> Sketch118
  Dir = (0,0,1)
  DirMode = 2
  FaceMakerClass = Part::FaceMakerBullseye
  LengthFwd = 90
  LengthRev = 0
  Placement = pos=(0,0,-160) rot=(0,0,1;0rad)
  Solid = true
  Symmetric = false
FEATURE [Sketcher::SketchObject] Sketch119
  FullyConstrained = true
  Placement = pos=(0,0,65) rot=(0,0,1;0rad)
  sketch-geometry (1):
    g0: Circle CenterX=0 CenterY=-150 CenterZ=0 NormalX=0 NormalY=0 NormalZ=1 AngleXU=0 Radius=100
  constraints (3):
    c: PointOnObject(g0,g-2)
    c: DistanceY(g0) = -150
    c: Radius(g0) = 100
FEATURE [Sketcher::SketchObject] Sketch120
  FullyConstrained = true
  Placement = pos=(0,0,80) rot=(0,0,1;0rad)
  sketch-geometry (1):
    g0: Circle CenterX=0 CenterY=-150 CenterZ=0 NormalX=0 NormalY=0 NormalZ=1 AngleXU=0 Radius=92
  constraints (3):
    c: PointOnObject(g0,g-2)
    c: DistanceY(g0) = -150
    c: Radius(g0) = 92
FEATURE [Part::Loft] Loft037  label="Loft049"
  Closed = false
  MaxDegree = 5
  Placement = pos=(0,0,-193.5) rot=(0,0,1;0rad)
  Ruled = false
  Sections = -> [Sketch120,Sketch119]
  Solid = true
FEATURE [Sketcher::SketchObject] Sketch121
  FullyConstrained = true
  Placement = pos=(0,0,65) rot=(0,0,1;0rad)
  sketch-geometry (1):
    g0: Circle CenterX=0 CenterY=-150 CenterZ=0 NormalX=0 NormalY=0 NormalZ=1 AngleXU=0 Radius=100
  constraints (3):
    c: PointOnObject(g0,g-2)
    c: DistanceY(g0) = -150
    c: Radius(g0) = 100
FEATURE [Sketcher::SketchObject] Sketch122
  FullyConstrained = true
  Placement = pos=(0,0,80) rot=(0,0,1;0rad)
  sketch-geometry (1):
    g0: Circle CenterX=0 CenterY=-150 CenterZ=0 NormalX=0 NormalY=0 NormalZ=1 AngleXU=0 Radius=92
  constraints (3):
    c: PointOnObject(g0,g-2)
    c: DistanceY(g0) = -150
    c: Radius(g0) = 92
FEATURE [Part::Loft] Loft038  label="Loft050"
  Closed = false
  MaxDegree = 5
  Placement = pos=(0,0,-191.5) rot=(0,0,1;0rad)
  Ruled = false
  Sections = -> [Sketch122,Sketch121]
  Solid = true
FEATURE [Part::Cut] Cut078
  Base = -> Loft038
  Tool = -> Loft037
FEATURE [Sketcher::SketchObject] Sketch123
  FullyConstrained = true
  Placement = pos=(0,0,65) rot=(0,0,1;0rad)
  sketch-geometry (1):
    g0: Circle CenterX=0 CenterY=-150 CenterZ=0 NormalX=0 NormalY=0 NormalZ=1 AngleXU=0 Radius=100
  constraints (3):
    c: PointOnObject(g0,g-2)
    c: DistanceY(g0) = -150
    c: Radius(g0) = 100
FEATURE [Sketcher::SketchObject] Sketch124
  FullyConstrained = true
  Placement = pos=(0,0,80) rot=(0,0,1;0rad)
  sketch-geometry (1):
    g0: Circle CenterX=0 CenterY=-150 CenterZ=0 NormalX=0 NormalY=0 NormalZ=1 AngleXU=0 Radius=92
  constraints (3):
    c: PointOnObject(g0,g-2)
    c: DistanceY(g0) = -150
    c: Radius(g0) = 92
FEATURE [Part::Loft] Loft039  label="Loft051"
  Closed = false
  MaxDegree = 5
  Placement = pos=(0,0,-193.5) rot=(0,0,1;0rad)
  Ruled = false
  Sections = -> [Sketch124,Sketch123]
  Solid = true
FEATURE [Sketcher::SketchObject] Sketch125
  FullyConstrained = true
  Placement = pos=(0,0,65) rot=(0,0,1;0rad)
  sketch-geometry (1):
    g0: Circle CenterX=0 CenterY=-150 CenterZ=0 NormalX=0 NormalY=0 NormalZ=1 AngleXU=0 Radius=100
  constraints (3):
    c: PointOnObject(g0,g-2)
    c: DistanceY(g0) = -150
    c: Radius(g0) = 100
FEATURE [Sketcher::SketchObject] Sketch126
  FullyConstrained = true
  Placement = pos=(0,0,80) rot=(0,0,1;0rad)
  sketch-geometry (1):
    g0: Circle CenterX=0 CenterY=-150 CenterZ=0 NormalX=0 NormalY=0 NormalZ=1 AngleXU=0 Radius=92
  constraints (3):
    c: PointOnObject(g0,g-2)
    c: DistanceY(g0) = -150
    c: Radius(g0) = 92
FEATURE [Part::Loft] Loft040  label="Loft052"
  Closed = false
  MaxDegree = 5
  Placement = pos=(0,0,-191.5) rot=(0,0,1;0rad)
  Ruled = false
  Sections = -> [Sketch126,Sketch125]
  Solid = true
FEATURE [Part::Cut] Cut079
  Base = -> Loft040
  Placement = pos=(0,0,8) rot=(0,0,1;0rad)
  Tool = -> Loft039
FEATURE [Sketcher::SketchObject] Sketch127
  FullyConstrained = true
  Placement = pos=(0,0,65) rot=(0,0,1;0rad)
  sketch-geometry (1):
    g0: Circle CenterX=0 CenterY=-150 CenterZ=0 NormalX=0 NormalY=0 NormalZ=1 AngleXU=0 Radius=100
  constraints (3):
    c: PointOnObject(g0,g-2)
    c: DistanceY(g0) = -150
    c: Radius(g0) = 100
FEATURE [Sketcher::SketchObject] Sketch128
  FullyConstrained = true
  Placement = pos=(0,0,80) rot=(0,0,1;0rad)
  sketch-geometry (1):
    g0: Circle CenterX=0 CenterY=-150 CenterZ=0 NormalX=0 NormalY=0 NormalZ=1 AngleXU=0 Radius=92
  constraints (3):
    c: PointOnObject(g0,g-2)
    c: DistanceY(g0) = -150
    c: Radius(g0) = 92
FEATURE [Part::Loft] Loft041  label="Loft053"
  Closed = false
  MaxDegree = 5
  Placement = pos=(0,0,-193.5) rot=(0,0,1;0rad)
  Ruled = false
  Sections = -> [Sketch128,Sketch127]
  Solid = true
FEATURE [Sketcher::SketchObject] Sketch129
  FullyConstrained = true
  Placement = pos=(0,0,65) rot=(0,0,1;0rad)
  sketch-geometry (1):
    g0: Circle CenterX=0 CenterY=-150 CenterZ=0 NormalX=0 NormalY=0 NormalZ=1 AngleXU=0 Radius=100
  constraints (3):
    c: PointOnObject(g0,g-2)
    c: DistanceY(g0) = -150
    c: Radius(g0) = 100
FEATURE [Sketcher::SketchObject] Sketch130
  FullyConstrained = true
  Placement = pos=(0,0,80) rot=(0,0,1;0rad)
  sketch-geometry (1):
    g0: Circle CenterX=0 CenterY=-150 CenterZ=0 NormalX=0 NormalY=0 NormalZ=1 AngleXU=0 Radius=92
  constraints (3):
    c: PointOnObject(g0,g-2)
    c: DistanceY(g0) = -150
    c: Radius(g0) = 92
FEATURE [Part::Loft] Loft042  label="Loft054"
  Closed = false
  MaxDegree = 5
  Placement = pos=(0,0,-191.5) rot=(0,0,1;0rad)
  Ruled = false
  Sections = -> [Sketch130,Sketch129]
  Solid = true
FEATURE [Part::Cut] Cut080
  Base = -> Loft042
  Placement = pos=(0,0,16) rot=(0,0,1;0rad)
  Tool = -> Loft041
FEATURE [Sketcher::SketchObject] Sketch131
  FullyConstrained = true
  Placement = pos=(0,0,65) rot=(0,0,1;0rad)
  sketch-geometry (1):
    g0: Circle CenterX=0 CenterY=-150 CenterZ=0 NormalX=0 NormalY=0 NormalZ=1 AngleXU=0 Radius=100
  constraints (3):
    c: PointOnObject(g0,g-2)
    c: DistanceY(g0) = -150
    c: Radius(g0) = 100
FEATURE [Sketcher::SketchObject] Sketch132
  FullyConstrained = true
  Placement = pos=(0,0,80) rot=(0,0,1;0rad)
  sketch-geometry (1):
    g0: Circle CenterX=0 CenterY=-150 CenterZ=0 NormalX=0 NormalY=0 NormalZ=1 AngleXU=0 Radius=92
  constraints (3):
    c: PointOnObject(g0,g-2)
    c: DistanceY(g0) = -150
    c: Radius(g0) = 92
FEATURE [Part::Loft] Loft043  label="Loft055"
  Closed = false
  MaxDegree = 5
  Placement = pos=(0,0,-193.5) rot=(0,0,1;0rad)
  Ruled = false
  Sections = -> [Sketch132,Sketch131]
  Solid = true
FEATURE [Sketcher::SketchObject] Sketch133
  FullyConstrained = true
  Placement = pos=(0,0,65) rot=(0,0,1;0rad)
  sketch-geometry (1):
    g0: Circle CenterX=0 CenterY=-150 CenterZ=0 NormalX=0 NormalY=0 NormalZ=1 AngleXU=0 Radius=100
  constraints (3):
    c: PointOnObject(g0,g-2)
    c: DistanceY(g0) = -150
    c: Radius(g0) = 100
FEATURE [Sketcher::SketchObject] Sketch134
  FullyConstrained = true
  Placement = pos=(0,0,80) rot=(0,0,1;0rad)
  sketch-geometry (1):
    g0: Circle CenterX=0 CenterY=-150 CenterZ=0 NormalX=0 NormalY=0 NormalZ=1 AngleXU=0 Radius=92
  constraints (3):
    c: PointOnObject(g0,g-2)
    c: DistanceY(g0) = -150
    c: Radius(g0) = 92
FEATURE [Part::Loft] Loft044  label="Loft056"
  Closed = false
  MaxDegree = 5
  Placement = pos=(0,0,-191.5) rot=(0,0,1;0rad)
  Ruled = false
  Sections = -> [Sketch134,Sketch133]
  Solid = true
FEATURE [Part::Cut] Cut081
  Base = -> Loft044
  Placement = pos=(0,0,24) rot=(0,0,1;0rad)
  Tool = -> Loft043
FEATURE [Sketcher::SketchObject] Sketch135
  FullyConstrained = true
  Placement = pos=(0,0,65) rot=(0,0,1;0rad)
  sketch-geometry (1):
    g0: Circle CenterX=0 CenterY=-150 CenterZ=0 NormalX=0 NormalY=0 NormalZ=1 AngleXU=0 Radius=100
  constraints (3):
    c: PointOnObject(g0,g-2)
    c: DistanceY(g0) = -150
    c: Radius(g0) = 100
FEATURE [Sketcher::SketchObject] Sketch136
  FullyConstrained = true
  Placement = pos=(0,0,80) rot=(0,0,1;0rad)
  sketch-geometry (1):
    g0: Circle CenterX=0 CenterY=-150 CenterZ=0 NormalX=0 NormalY=0 NormalZ=1 AngleXU=0 Radius=92
  constraints (3):
    c: PointOnObject(g0,g-2)
    c: DistanceY(g0) = -150
    c: Radius(g0) = 92
FEATURE [Part::Loft] Loft045  label="Loft057"
  Closed = false
  MaxDegree = 5
  Placement = pos=(0,0,-193.5) rot=(0,0,1;0rad)
  Ruled = false
  Sections = -> [Sketch136,Sketch135]
  Solid = true
FEATURE [Sketcher::SketchObject] Sketch137
  FullyConstrained = true
  Placement = pos=(0,0,65) rot=(0,0,1;0rad)
  sketch-geometry (1):
    g0: Circle CenterX=0 CenterY=-150 CenterZ=0 NormalX=0 NormalY=0 NormalZ=1 AngleXU=0 Radius=100
  constraints (3):
    c: PointOnObject(g0,g-2)
    c: DistanceY(g0) = -150
    c: Radius(g0) = 100
FEATURE [Sketcher::SketchObject] Sketch138
  FullyConstrained = true
  Placement = pos=(0,0,80) rot=(0,0,1;0rad)
  sketch-geometry (1):
    g0: Circle CenterX=0 CenterY=-150 CenterZ=0 NormalX=0 NormalY=0 NormalZ=1 AngleXU=0 Radius=92
  constraints (3):
    c: PointOnObject(g0,g-2)
    c: DistanceY(g0) = -150
    c: Radius(g0) = 92
FEATURE [Part::Loft] Loft046  label="Loft058"
  Closed = false
  MaxDegree = 5
  Placement = pos=(0,0,-191.5) rot=(0,0,1;0rad)
  Ruled = false
  Sections = -> [Sketch138,Sketch137]
  Solid = true
FEATURE [Part::Cut] Cut082
  Base = -> Loft046
  Placement = pos=(0,0,32) rot=(0,0,1;0rad)
  Tool = -> Loft045
FEATURE [Sketcher::SketchObject] Sketch139
  FullyConstrained = true
  Placement = pos=(0,0,65) rot=(0,0,1;0rad)
  sketch-geometry (1):
    g0: Circle CenterX=0 CenterY=-150 CenterZ=0 NormalX=0 NormalY=0 NormalZ=1 AngleXU=0 Radius=100
  constraints (3):
    c: PointOnObject(g0,g-2)
    c: DistanceY(g0) = -150
    c: Radius(g0) = 100
FEATURE [Sketcher::SketchObject] Sketch140
  FullyConstrained = true
  Placement = pos=(0,0,80) rot=(0,0,1;0rad)
  sketch-geometry (1):
    g0: Circle CenterX=0 CenterY=-150 CenterZ=0 NormalX=0 NormalY=0 NormalZ=1 AngleXU=0 Radius=92
  constraints (3):
    c: PointOnObject(g0,g-2)
    c: DistanceY(g0) = -150
    c: Radius(g0) = 92
FEATURE [Part::Loft] Loft047  label="Loft059"
  Closed = false
  MaxDegree = 5
  Placement = pos=(0,0,-193.5) rot=(0,0,1;0rad)
  Ruled = false
  Sections = -> [Sketch140,Sketch139]
  Solid = true
FEATURE [Sketcher::SketchObject] Sketch141
  FullyConstrained = true
  Placement = pos=(0,0,65) rot=(0,0,1;0rad)
  sketch-geometry (1):
    g0: Circle CenterX=0 CenterY=-150 CenterZ=0 NormalX=0 NormalY=0 NormalZ=1 AngleXU=0 Radius=100
  constraints (3):
    c: PointOnObject(g0,g-2)
    c: DistanceY(g0) = -150
    c: Radius(g0) = 100
FEATURE [Sketcher::SketchObject] Sketch142
  FullyConstrained = true
  Placement = pos=(0,0,80) rot=(0,0,1;0rad)
  sketch-geometry (1):
    g0: Circle CenterX=0 CenterY=-150 CenterZ=0 NormalX=0 NormalY=0 NormalZ=1 AngleXU=0 Radius=92
  constraints (3):
    c: PointOnObject(g0,g-2)
    c: DistanceY(g0) = -150
    c: Radius(g0) = 92
FEATURE [Part::Loft] Loft048  label="Loft060"
  Closed = false
  MaxDegree = 5
  Placement = pos=(0,0,-191.5) rot=(0,0,1;0rad)
  Ruled = false
  Sections = -> [Sketch142,Sketch141]
  Solid = true
FEATURE [Part::Cut] Cut083
  Base = -> Loft048
  Placement = pos=(0,0,40) rot=(0,0,1;0rad)
  Tool = -> Loft047
FEATURE [Part::MultiFuse] Fusion120  label="fanCuts001"
  Placement = pos=(0,0,-32) rot=(0,0,1;0rad)
  Shapes = -> [Cut078,Cut079,Cut080,Cut081,Cut082,Cut083]
FEATURE [Part::MultiFuse] Fusion121
  Shapes = -> [Fusion120,Fusion119]
FEATURE [Part::Box] Box017  label="Cube010"
  AttacherType = Attacher::AttachEngine3D
  Height = 30
  Length = 42
  Placement = pos=(-21,-265,-152) rot=(0,0,1;0rad)
  Width = 100
FEATURE [Mesh::Feature] logoLightModule
  Placement = pos=(0.15,-236.25,-151) rot=(0,0,1;0rad)
FEATURE [Part::Cut] Cut084  label="fanCut"
  Base = -> Extrude043
  Tool = -> Box017
FEATURE [Part::MultiCommon] Common
  Shapes = -> [Fusion121,Cut084]
FEATURE [Part::Cut] Cut085  label="level3to4"
  Base = -> Cut056
  Tool = -> Common
FEATURE [Sketcher::SketchObject] Sketch143
  FullyConstrained = true
  sketch-geometry (2):
    g0: Circle CenterX=0 CenterY=-150 CenterZ=0 NormalX=0 NormalY=0 NormalZ=1 AngleXU=0 Radius=3.2
    g1: Circle CenterX=0 CenterY=-100 CenterZ=0 NormalX=0 NormalY=0 NormalZ=1 AngleXU=0 Radius=3.2
  constraints (6):
    c: PointOnObject(g0,g-2)
    c: PointOnObject(g1,g-2)
    c: DistanceY(g0) = -150
    c: DistanceY(g1) = -100
    c: Equal(g1,g0)
    c: Diameter(g1) = 6.4
FEATURE [Part::Extrusion] Extrude044
  Base = -> Sketch143
  Dir = (0,0,1)
  DirMode = 2
  FaceMakerClass = Part::FaceMakerBullseye
  LengthFwd = 50
  LengthRev = 0
  Placement = pos=(0,0,-290) rot=(0,0,1;0rad)
  Solid = true
  Symmetric = false
FEATURE [Part::Cut] Cut086  label="level5s007"
  Base = -> Fillet010
  Tool = -> Extrude044
FEATURE [Part::Fillet] Fillet012  label="level5s008"
  Base = -> Cut086
  Edges = 4 edges r=2.5: [Edge111,Edge114,Edge117,Edge120]
FEATURE [Part::Fillet] Fillet013  label="level4s002"
  Base = -> Cut039
  Edges = 10 edges r=2: [Edge45,Edge49,Edge52,Edge57,Edge60,Edge63,Edge69,Edge72,Edge77,Edge196]
FEATURE [Part::Box] Box018  label="tubeCut"
  AttacherType = Attacher::AttachEngine3D
  Height = 10
  Length = 108
  Placement = pos=(-54,-222,-65) rot=(0,0,1;0rad)
  Width = 145
FEATURE [Part::Cut] Cut087  label="level3to4s"
  Base = -> Cut085
  Tool = -> Box018
FEATURE [Part::Fillet] Fillet014
  Base = -> Cut045
  Edges = 1 edges r=2: [Edge22]
FEATURE [Part::Fillet] Fillet015  label="level3s001"
  Base = -> Fillet014
  Edges = 4 edges r=2: [Edge49,Edge55,Edge57,Edge58]
FEATURE [Part::Box] Box019  label="Cube011"
  AttacherType = Attacher::AttachEngine3D
  Height = 40
  Length = 40
  Placement = pos=(13.25,-219.25,-65) rot=(0,0,1;0rad)
  Width = 21
FEATURE [Part::Cut] Cut088  label="level3s002"
  Base = -> Fillet015
  Tool = -> Box019
FEATURE [Part::Fillet] Fillet016  label="level3s003"
  Base = -> Cut088
  Edges = 1 edges r=2: [Edge47]
FEATURE [Part::Fillet] Fillet017  label="level2s"
  Base = -> Cut034
  Edges = 32 edges r=1.5: [Edge42,Edge43,Edge44,Edge45,Edge46,Edge47,Edge48,Edge49,Edge53,Edge54,Edge55,Edge56,Edge57,Edge58,Edge59,Edge60,Edge61,Edge62,Edge63,Edge64,Edge66,Edge67,Edge68,Edge69,Edge74,Edge75,Edge76,Edge77,Edge78,Edge79,Edge80,Edge81]
FEATURE [Part::Fillet] Fillet018
  Base = -> Fusion069
  Edges = 7 edges r=2: [Edge91,Edge95,Edge103,Edge105,Edge106,Edge110,Edge111]
FEATURE [Part::Cylinder] Cylinder171
  Angle = 360
  AttacherType = Attacher::AttachEngine3D
  FirstAngle = 0
  Height = 10
  Placement = pos=(77.75,-150,90) rot=(0,1,0;1.5708rad)
  Radius = 2.8
  SecondAngle = 0
FEATURE [Part::Cut] Cut089  label="level1s"
  Base = -> Fillet018
  Tool = -> Cylinder171
